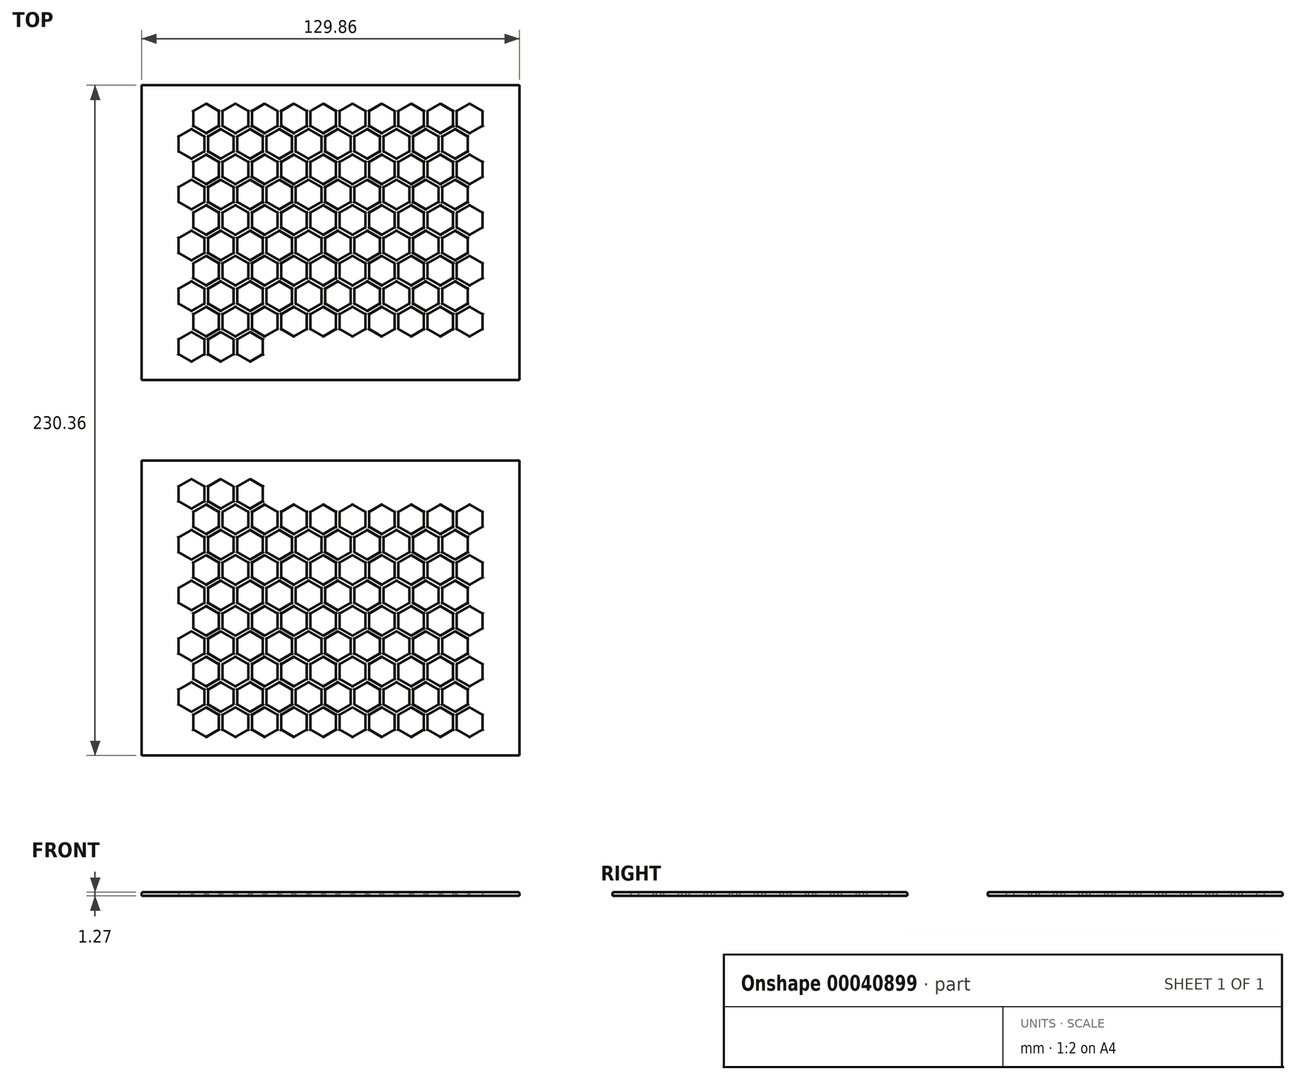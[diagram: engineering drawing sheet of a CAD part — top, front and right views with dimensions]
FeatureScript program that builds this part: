
annotation { "Feature Type Name" : "Feature", "Feature Type Description" : "" }
export const myFeature = defineFeature(function(context is Context, id is Id, definition is map)
    precondition{}
    {
        {
            var Q0;
            Q0=qCreatedBy(makeId("Top.planeOp"),FACE);
            var sketch = newSketch(context, id + "F0", { "sketchPlane" : qUnion([Q0])});
            skCircle(sketch, "E0.cCircle", {"center": v(-4.27, 25.27) * mm, "radius": 5.08 * mm, "construction": true});
            skLineSegment(sketch, "E0.0", {"start": v(-4.27, 20.19) * mm, "end": v(-8.67, 22.73) * mm});
            skLineSegment(sketch, "E0.1", {"start": v(-8.67, 22.73) * mm, "end": v(-8.67, 27.8) * mm});
            skLineSegment(sketch, "E0.2", {"start": v(-8.67, 27.8) * mm, "end": v(-4.27, 30.35) * mm});
            skLineSegment(sketch, "E0.3", {"start": v(-4.27, 30.35) * mm, "end": v(0.13, 27.8) * mm});
            skLineSegment(sketch, "E0.4", {"start": v(0.13, 27.8) * mm, "end": v(0.13, 22.73) * mm});
            skLineSegment(sketch, "E0.5", {"start": v(0.13, 22.73) * mm, "end": v(-4.27, 20.19) * mm});
            skLineSegment(sketch, "E1.1.0.0", {"start": v(5.8, 20.19) * mm, "end": v(1.4, 22.73) * mm});
            skLineSegment(sketch, "E1.1.0.1", {"start": v(1.4, 22.73) * mm, "end": v(1.4, 27.8) * mm});
            skLineSegment(sketch, "E1.1.0.2", {"start": v(1.4, 27.8) * mm, "end": v(5.8, 30.35) * mm});
            skLineSegment(sketch, "E1.1.0.3", {"start": v(5.8, 30.35) * mm, "end": v(10.2, 27.8) * mm});
            skLineSegment(sketch, "E1.1.0.4", {"start": v(10.2, 27.8) * mm, "end": v(10.2, 22.73) * mm});
            skLineSegment(sketch, "E1.1.0.5", {"start": v(10.2, 22.73) * mm, "end": v(5.8, 20.19) * mm});
            skCircle(sketch, "E1.1.0.6", {"center": v(5.8, 25.27) * mm, "radius": 5.08 * mm, "construction": true});
            skLineSegment(sketch, "E1.2.0.0", {"start": v(15.87, 20.19) * mm, "end": v(11.47, 22.73) * mm});
            skLineSegment(sketch, "E1.2.0.1", {"start": v(11.47, 22.73) * mm, "end": v(11.47, 27.8) * mm});
            skLineSegment(sketch, "E1.2.0.2", {"start": v(11.47, 27.8) * mm, "end": v(15.87, 30.35) * mm});
            skLineSegment(sketch, "E1.2.0.3", {"start": v(15.87, 30.35) * mm, "end": v(20.27, 27.8) * mm});
            skLineSegment(sketch, "E1.2.0.4", {"start": v(20.27, 27.8) * mm, "end": v(20.27, 22.73) * mm});
            skLineSegment(sketch, "E1.2.0.5", {"start": v(20.27, 22.73) * mm, "end": v(15.87, 20.19) * mm});
            skCircle(sketch, "E1.2.0.6", {"center": v(15.87, 25.27) * mm, "radius": 5.08 * mm, "construction": true});
            skLineSegment(sketch, "E1.direction1", {"start": v(-8.67, 22.73) * mm, "end": v(1.4, 22.73) * mm, "construction": true});
            skLineSegment(sketch, "E2.0.1.0", {"start": v(-3.63, 31.45) * mm, "end": v(6.44, 31.45) * mm, "construction": true});
            skLineSegment(sketch, "E2.0.1.1", {"start": v(75.65, 36.53) * mm, "end": v(75.65, 31.45) * mm});
            skLineSegment(sketch, "E2.0.1.2", {"start": v(45.44, 31.45) * mm, "end": v(41.04, 28.9) * mm});
            skLineSegment(sketch, "E2.0.1.3", {"start": v(36.64, 31.45) * mm, "end": v(36.64, 36.53) * mm});
            skCircle(sketch, "E2.0.1.4", {"center": v(61.18, 33.99) * mm, "radius": 5.08 * mm, "construction": true});
            skLineSegment(sketch, "E2.0.1.5", {"start": v(86.99, 31.45) * mm, "end": v(86.99, 36.53) * mm});
            skCircle(sketch, "E2.0.1.6", {"center": v(51.11, 33.99) * mm, "radius": 5.08 * mm, "construction": true});
            skLineSegment(sketch, "E2.0.1.7", {"start": v(5.17, 36.53) * mm, "end": v(5.17, 31.45) * mm});
            skLineSegment(sketch, "E2.0.1.8", {"start": v(46.71, 36.53) * mm, "end": v(51.11, 39.07) * mm});
            skLineSegment(sketch, "E2.0.1.9", {"start": v(61.18, 28.9) * mm, "end": v(56.78, 31.45) * mm});
            skLineSegment(sketch, "E2.0.1.10", {"start": v(26.58, 36.53) * mm, "end": v(30.98, 39.07) * mm});
            skLineSegment(sketch, "E2.0.1.11", {"start": v(55.51, 36.53) * mm, "end": v(55.51, 31.45) * mm});
            skLineSegment(sketch, "E2.0.1.12", {"start": v(81.32, 28.9) * mm, "end": v(76.92, 31.45) * mm});
            skCircle(sketch, "E2.0.1.13", {"center": v(71.25, 33.99) * mm, "radius": 5.08 * mm, "construction": true});
            skLineSegment(sketch, "E2.0.1.14", {"start": v(41.04, 28.9) * mm, "end": v(36.64, 31.45) * mm});
            skLineSegment(sketch, "E2.0.1.15", {"start": v(25.3, 31.45) * mm, "end": v(20.9, 28.9) * mm});
            skLineSegment(sketch, "E2.0.1.16", {"start": v(35.37, 36.53) * mm, "end": v(35.37, 31.45) * mm});
            skLineSegment(sketch, "E2.0.1.17", {"start": v(6.44, 36.53) * mm, "end": v(10.84, 39.07) * mm});
            skLineSegment(sketch, "E2.0.1.18", {"start": v(0.77, 28.9) * mm, "end": v(-3.63, 31.45) * mm});
            skLineSegment(sketch, "E2.0.1.19", {"start": v(41.04, 39.07) * mm, "end": v(45.44, 36.53) * mm});
            skCircle(sketch, "E2.0.1.20", {"center": v(20.9, 33.99) * mm, "radius": 5.08 * mm, "construction": true});
            skLineSegment(sketch, "E2.0.1.21", {"start": v(-3.63, 31.45) * mm, "end": v(-3.63, 36.53) * mm});
            skLineSegment(sketch, "E2.0.1.22", {"start": v(0.77, 39.07) * mm, "end": v(5.17, 36.53) * mm});
            skLineSegment(sketch, "E2.0.1.23", {"start": v(5.17, 31.45) * mm, "end": v(0.77, 28.9) * mm});
            skLineSegment(sketch, "E2.0.1.24", {"start": v(20.9, 39.07) * mm, "end": v(25.3, 36.53) * mm});
            skLineSegment(sketch, "E2.0.1.25", {"start": v(45.44, 36.53) * mm, "end": v(45.44, 31.45) * mm});
            skLineSegment(sketch, "E2.0.1.26", {"start": v(30.98, 28.9) * mm, "end": v(26.58, 31.45) * mm});
            skCircle(sketch, "E2.0.1.27", {"center": v(0.77, 33.99) * mm, "radius": 5.08 * mm, "construction": true});
            skLineSegment(sketch, "E2.0.1.28", {"start": v(71.25, 39.07) * mm, "end": v(75.65, 36.53) * mm});
            skLineSegment(sketch, "E2.0.1.29", {"start": v(65.58, 31.45) * mm, "end": v(61.18, 28.9) * mm});
            skLineSegment(sketch, "E2.0.1.30", {"start": v(56.78, 31.45) * mm, "end": v(56.78, 36.53) * mm});
            skLineSegment(sketch, "E2.0.1.31", {"start": v(36.64, 36.53) * mm, "end": v(41.04, 39.07) * mm});
            skLineSegment(sketch, "E2.0.1.32", {"start": v(66.85, 31.45) * mm, "end": v(66.85, 36.53) * mm});
            skLineSegment(sketch, "E2.0.1.33", {"start": v(-3.63, 36.53) * mm, "end": v(0.77, 39.07) * mm});
            skCircle(sketch, "E2.0.1.34", {"center": v(10.84, 33.99) * mm, "radius": 5.08 * mm, "construction": true});
            skLineSegment(sketch, "E2.0.1.35", {"start": v(16.5, 36.53) * mm, "end": v(20.9, 39.07) * mm});
            skLineSegment(sketch, "E2.0.1.36", {"start": v(85.72, 31.45) * mm, "end": v(81.32, 28.9) * mm});
            skLineSegment(sketch, "E2.0.1.37", {"start": v(10.84, 39.07) * mm, "end": v(15.24, 36.53) * mm});
            skLineSegment(sketch, "E2.0.1.38", {"start": v(65.58, 36.53) * mm, "end": v(65.58, 31.45) * mm});
            skLineSegment(sketch, "E2.0.1.39", {"start": v(81.32, 39.07) * mm, "end": v(85.72, 36.53) * mm});
            skLineSegment(sketch, "E2.0.1.40", {"start": v(10.84, 28.9) * mm, "end": v(6.44, 31.45) * mm});
            skLineSegment(sketch, "E2.0.1.41", {"start": v(26.58, 31.45) * mm, "end": v(26.58, 36.53) * mm});
            skLineSegment(sketch, "E2.0.1.42", {"start": v(51.11, 39.07) * mm, "end": v(55.51, 36.53) * mm});
            skCircle(sketch, "E2.0.1.43", {"center": v(41.04, 33.99) * mm, "radius": 5.08 * mm, "construction": true});
            skLineSegment(sketch, "E2.0.1.44", {"start": v(56.78, 36.53) * mm, "end": v(61.18, 39.07) * mm});
            skCircle(sketch, "E2.0.1.45", {"center": v(91.39, 33.99) * mm, "radius": 5.08 * mm, "construction": true});
            skLineSegment(sketch, "E2.0.1.46", {"start": v(6.44, 31.45) * mm, "end": v(6.44, 36.53) * mm});
            skLineSegment(sketch, "E2.0.1.47", {"start": v(35.37, 31.45) * mm, "end": v(30.98, 28.9) * mm});
            skLineSegment(sketch, "E2.0.1.48", {"start": v(16.5, 31.45) * mm, "end": v(16.5, 36.53) * mm});
            skLineSegment(sketch, "E2.0.1.49", {"start": v(91.39, 28.9) * mm, "end": v(86.99, 31.45) * mm});
            skCircle(sketch, "E2.0.1.50", {"center": v(30.98, 33.99) * mm, "radius": 5.08 * mm, "construction": true});
            skLineSegment(sketch, "E2.0.1.51", {"start": v(91.39, 39.07) * mm, "end": v(95.79, 36.53) * mm});
            skLineSegment(sketch, "E2.0.1.52", {"start": v(95.79, 31.45) * mm, "end": v(91.39, 28.9) * mm});
            skLineSegment(sketch, "E2.0.1.53", {"start": v(86.99, 36.53) * mm, "end": v(91.39, 39.07) * mm});
            skLineSegment(sketch, "E2.0.1.54", {"start": v(95.79, 36.53) * mm, "end": v(95.79, 31.45) * mm});
            skLineSegment(sketch, "E2.0.1.55", {"start": v(55.51, 31.45) * mm, "end": v(51.11, 28.9) * mm});
            skLineSegment(sketch, "E2.0.1.56", {"start": v(30.98, 39.07) * mm, "end": v(35.37, 36.53) * mm});
            skLineSegment(sketch, "E2.0.1.57", {"start": v(25.3, 36.53) * mm, "end": v(25.3, 31.45) * mm});
            skLineSegment(sketch, "E2.0.1.58", {"start": v(76.92, 31.45) * mm, "end": v(76.92, 36.53) * mm});
            skCircle(sketch, "E2.0.1.59", {"center": v(81.32, 33.99) * mm, "radius": 5.08 * mm, "construction": true});
            skLineSegment(sketch, "E2.0.1.60", {"start": v(85.72, 36.53) * mm, "end": v(85.72, 31.45) * mm});
            skLineSegment(sketch, "E2.0.1.61", {"start": v(71.25, 28.9) * mm, "end": v(66.85, 31.45) * mm});
            skLineSegment(sketch, "E2.0.1.62", {"start": v(61.18, 39.07) * mm, "end": v(65.58, 36.53) * mm});
            skLineSegment(sketch, "E2.0.1.63", {"start": v(66.85, 36.53) * mm, "end": v(71.25, 39.07) * mm});
            skLineSegment(sketch, "E2.0.1.64", {"start": v(15.24, 36.53) * mm, "end": v(15.24, 31.45) * mm});
            skLineSegment(sketch, "E2.0.1.65", {"start": v(15.24, 31.45) * mm, "end": v(10.84, 28.9) * mm});
            skLineSegment(sketch, "E2.0.1.66", {"start": v(51.11, 28.9) * mm, "end": v(46.71, 31.45) * mm});
            skLineSegment(sketch, "E2.0.1.67", {"start": v(46.71, 31.45) * mm, "end": v(46.71, 36.53) * mm});
            skLineSegment(sketch, "E2.0.1.68", {"start": v(76.92, 36.53) * mm, "end": v(81.32, 39.07) * mm});
            skLineSegment(sketch, "E2.0.1.69", {"start": v(20.9, 28.9) * mm, "end": v(16.5, 31.45) * mm});
            skLineSegment(sketch, "E2.0.1.70", {"start": v(75.65, 31.45) * mm, "end": v(71.25, 28.9) * mm});
            skLineSegment(sketch, "E2.direction1", {"start": v(-8.67, 22.73) * mm, "end": v(18.3, 22.73) * mm, "construction": true});
            skLineSegment(sketch, "E2.direction2", {"start": v(-8.67, 22.73) * mm, "end": v(-3.63, 31.45) * mm, "construction": true});
            skLineSegment(sketch, "E3", {"start": v(0.13, 27.8) * mm, "end": v(0.77, 28.9) * mm, "construction": true});
            skLineSegment(sketch, "E4", {"start": v(0.77, 28.9) * mm, "end": v(1.4, 27.8) * mm, "construction": true});
            skLineSegment(sketch, "E5", {"start": v(0.13, 27.8) * mm, "end": v(1.4, 27.8) * mm, "construction": true});
            skLineSegment(sketch, "E6.0.1.0", {"start": v(-3.63, 48.89) * mm, "end": v(6.44, 48.89) * mm, "construction": true});
            skCircle(sketch, "E6.0.1.1", {"center": v(20.9, 51.43) * mm, "radius": 5.08 * mm, "construction": true});
            skLineSegment(sketch, "E6.0.1.2", {"start": v(76.92, 53.97) * mm, "end": v(81.32, 56.5) * mm});
            skCircle(sketch, "E6.0.1.3", {"center": v(61.18, 51.43) * mm, "radius": 5.08 * mm, "construction": true});
            skLineSegment(sketch, "E6.0.1.4", {"start": v(80.68, 45.25) * mm, "end": v(80.68, 40.17) * mm});
            skLineSegment(sketch, "E6.0.1.5", {"start": v(-8.67, 40.17) * mm, "end": v(18.3, 40.17) * mm, "construction": true});
            skCircle(sketch, "E6.0.1.6", {"center": v(51.11, 51.43) * mm, "radius": 5.08 * mm, "construction": true});
            skCircle(sketch, "E6.0.1.7", {"center": v(0.77, 51.43) * mm, "radius": 5.08 * mm, "construction": true});
            skLineSegment(sketch, "E6.0.1.8", {"start": v(61.82, 40.17) * mm, "end": v(61.82, 45.25) * mm});
            skCircle(sketch, "E6.0.1.9", {"center": v(76.28, 42.7) * mm, "radius": 5.08 * mm, "construction": true});
            skLineSegment(sketch, "E6.0.1.10", {"start": v(56.15, 37.63) * mm, "end": v(51.75, 40.17) * mm});
            skLineSegment(sketch, "E6.0.1.11", {"start": v(15.87, 37.63) * mm, "end": v(11.47, 40.17) * mm});
            skLineSegment(sketch, "E6.0.1.12", {"start": v(71.25, 56.5) * mm, "end": v(75.65, 53.97) * mm});
            skLineSegment(sketch, "E6.0.1.13", {"start": v(20.27, 40.17) * mm, "end": v(15.87, 37.63) * mm});
            skLineSegment(sketch, "E6.0.1.14", {"start": v(56.78, 53.97) * mm, "end": v(61.18, 56.5) * mm});
            skLineSegment(sketch, "E6.0.1.15", {"start": v(95.79, 48.89) * mm, "end": v(91.39, 46.35) * mm});
            skLineSegment(sketch, "E6.0.1.16", {"start": v(30.34, 40.17) * mm, "end": v(25.94, 37.63) * mm});
            skLineSegment(sketch, "E6.0.1.17", {"start": v(60.55, 45.25) * mm, "end": v(60.55, 40.17) * mm});
            skLineSegment(sketch, "E6.0.1.18", {"start": v(91.39, 56.5) * mm, "end": v(95.79, 53.97) * mm});
            skLineSegment(sketch, "E6.0.1.19", {"start": v(-8.67, 40.17) * mm, "end": v(-3.63, 48.89) * mm, "construction": true});
            skLineSegment(sketch, "E6.0.1.20", {"start": v(41.04, 56.5) * mm, "end": v(45.44, 53.97) * mm});
            skLineSegment(sketch, "E6.0.1.21", {"start": v(36, 37.63) * mm, "end": v(31.61, 40.17) * mm});
            skLineSegment(sketch, "E6.0.1.22", {"start": v(81.32, 56.5) * mm, "end": v(85.72, 53.97) * mm});
            skLineSegment(sketch, "E6.0.1.23", {"start": v(66.22, 37.63) * mm, "end": v(61.82, 40.17) * mm});
            skLineSegment(sketch, "E6.0.1.24", {"start": v(40.4, 40.17) * mm, "end": v(36, 37.63) * mm});
            skLineSegment(sketch, "E6.0.1.25", {"start": v(10.84, 56.5) * mm, "end": v(15.24, 53.97) * mm});
            skLineSegment(sketch, "E6.0.1.26", {"start": v(55.51, 53.97) * mm, "end": v(55.51, 48.89) * mm});
            skLineSegment(sketch, "E6.0.1.27", {"start": v(61.18, 46.35) * mm, "end": v(56.78, 48.89) * mm});
            skLineSegment(sketch, "E6.0.1.28", {"start": v(60.55, 40.17) * mm, "end": v(56.15, 37.63) * mm});
            skLineSegment(sketch, "E6.0.1.29", {"start": v(10.2, 40.17) * mm, "end": v(5.8, 37.63) * mm});
            skLineSegment(sketch, "E6.0.1.30", {"start": v(0.13, 40.17) * mm, "end": v(-4.27, 37.63) * mm});
            skLineSegment(sketch, "E6.0.1.31", {"start": v(45.44, 53.97) * mm, "end": v(45.44, 48.89) * mm});
            skCircle(sketch, "E6.0.1.32", {"center": v(10.84, 51.43) * mm, "radius": 5.08 * mm, "construction": true});
            skLineSegment(sketch, "E6.0.1.33", {"start": v(65.58, 53.97) * mm, "end": v(65.58, 48.89) * mm});
            skLineSegment(sketch, "E6.0.1.34", {"start": v(-3.63, 48.89) * mm, "end": v(-3.63, 53.97) * mm});
            skCircle(sketch, "E6.0.1.35", {"center": v(71.25, 51.43) * mm, "radius": 5.08 * mm, "construction": true});
            skLineSegment(sketch, "E6.0.1.36", {"start": v(90.75, 45.25) * mm, "end": v(90.75, 40.17) * mm});
            skLineSegment(sketch, "E6.0.1.37", {"start": v(61.82, 45.25) * mm, "end": v(66.22, 47.79) * mm});
            skLineSegment(sketch, "E6.0.1.38", {"start": v(46.08, 37.63) * mm, "end": v(41.68, 40.17) * mm});
            skLineSegment(sketch, "E6.0.1.39", {"start": v(71.25, 46.35) * mm, "end": v(66.85, 48.89) * mm});
            skCircle(sketch, "E6.0.1.40", {"center": v(91.39, 51.43) * mm, "radius": 5.08 * mm, "construction": true});
            skLineSegment(sketch, "E6.0.1.41", {"start": v(65.58, 48.89) * mm, "end": v(61.18, 46.35) * mm});
            skLineSegment(sketch, "E6.0.1.42", {"start": v(20.9, 56.5) * mm, "end": v(25.3, 53.97) * mm});
            skLineSegment(sketch, "E6.0.1.43", {"start": v(56.15, 47.79) * mm, "end": v(60.55, 45.25) * mm});
            skLineSegment(sketch, "E6.0.1.44", {"start": v(-8.67, 45.25) * mm, "end": v(-4.27, 47.79) * mm});
            skCircle(sketch, "E6.0.1.45", {"center": v(25.94, 42.7) * mm, "radius": 5.08 * mm, "construction": true});
            skLineSegment(sketch, "E6.0.1.46", {"start": v(90.75, 40.17) * mm, "end": v(86.35, 37.63) * mm});
            skCircle(sketch, "E6.0.1.47", {"center": v(-4.27, 42.7) * mm, "radius": 5.08 * mm, "construction": true});
            skLineSegment(sketch, "E6.0.1.48", {"start": v(51.11, 56.5) * mm, "end": v(55.51, 53.97) * mm});
            skLineSegment(sketch, "E6.0.1.49", {"start": v(80.68, 40.17) * mm, "end": v(76.28, 37.63) * mm});
            skCircle(sketch, "E6.0.1.50", {"center": v(5.8, 42.7) * mm, "radius": 5.08 * mm, "construction": true});
            skLineSegment(sketch, "E6.0.1.51", {"start": v(0.77, 56.5) * mm, "end": v(5.17, 53.97) * mm});
            skLineSegment(sketch, "E6.0.1.52", {"start": v(66.22, 47.79) * mm, "end": v(70.62, 45.25) * mm});
            skLineSegment(sketch, "E6.0.1.53", {"start": v(61.18, 56.5) * mm, "end": v(65.58, 53.97) * mm});
            skLineSegment(sketch, "E6.0.1.54", {"start": v(56.78, 48.89) * mm, "end": v(56.78, 53.97) * mm});
            skLineSegment(sketch, "E6.0.1.55", {"start": v(81.95, 40.17) * mm, "end": v(81.95, 45.25) * mm});
            skCircle(sketch, "E6.0.1.56", {"center": v(56.15, 42.7) * mm, "radius": 5.08 * mm, "construction": true});
            skLineSegment(sketch, "E6.0.1.57", {"start": v(86.99, 53.97) * mm, "end": v(91.39, 56.5) * mm});
            skCircle(sketch, "E6.0.1.58", {"center": v(81.32, 51.43) * mm, "radius": 5.08 * mm, "construction": true});
            skLineSegment(sketch, "E6.0.1.59", {"start": v(-4.27, 37.63) * mm, "end": v(-8.67, 40.17) * mm});
            skLineSegment(sketch, "E6.0.1.60", {"start": v(25.94, 37.63) * mm, "end": v(21.54, 40.17) * mm});
            skCircle(sketch, "E6.0.1.61", {"center": v(86.35, 42.7) * mm, "radius": 5.08 * mm, "construction": true});
            skLineSegment(sketch, "E6.0.1.62", {"start": v(41.68, 45.25) * mm, "end": v(46.08, 47.79) * mm});
            skLineSegment(sketch, "E6.0.1.63", {"start": v(66.85, 53.97) * mm, "end": v(71.25, 56.5) * mm});
            skLineSegment(sketch, "E6.0.1.64", {"start": v(36.64, 53.97) * mm, "end": v(41.04, 56.5) * mm});
            skLineSegment(sketch, "E6.0.1.65", {"start": v(70.62, 40.17) * mm, "end": v(66.22, 37.63) * mm});
            skLineSegment(sketch, "E6.0.1.66", {"start": v(16.5, 48.89) * mm, "end": v(16.5, 53.97) * mm});
            skLineSegment(sketch, "E6.0.1.67", {"start": v(66.85, 48.89) * mm, "end": v(66.85, 53.97) * mm});
            skLineSegment(sketch, "E6.0.1.68", {"start": v(15.24, 53.97) * mm, "end": v(15.24, 48.89) * mm});
            skCircle(sketch, "E6.0.1.69", {"center": v(66.22, 42.7) * mm, "radius": 5.08 * mm, "construction": true});
            skLineSegment(sketch, "E6.0.1.70", {"start": v(50.48, 45.25) * mm, "end": v(50.48, 40.17) * mm});
            skLineSegment(sketch, "E6.0.1.71", {"start": v(-3.63, 53.97) * mm, "end": v(0.77, 56.5) * mm});
            skLineSegment(sketch, "E6.0.1.72", {"start": v(6.44, 53.97) * mm, "end": v(10.84, 56.5) * mm});
            skLineSegment(sketch, "E6.0.1.73", {"start": v(-8.67, 40.17) * mm, "end": v(-8.67, 45.25) * mm});
            skCircle(sketch, "E6.0.1.74", {"center": v(41.04, 51.43) * mm, "radius": 5.08 * mm, "construction": true});
            skLineSegment(sketch, "E6.0.1.75", {"start": v(46.71, 48.89) * mm, "end": v(46.71, 53.97) * mm});
            skLineSegment(sketch, "E6.0.1.76", {"start": v(16.5, 53.97) * mm, "end": v(20.9, 56.5) * mm});
            skLineSegment(sketch, "E6.0.1.77", {"start": v(5.8, 37.63) * mm, "end": v(1.4, 40.17) * mm});
            skLineSegment(sketch, "E6.0.1.78", {"start": v(30.98, 56.5) * mm, "end": v(35.37, 53.97) * mm});
            skCircle(sketch, "E6.0.1.79", {"center": v(46.08, 42.7) * mm, "radius": 5.08 * mm, "construction": true});
            skLineSegment(sketch, "E6.0.1.80", {"start": v(86.35, 37.63) * mm, "end": v(81.95, 40.17) * mm});
            skLineSegment(sketch, "E6.0.1.81", {"start": v(95.79, 53.97) * mm, "end": v(95.79, 48.89) * mm});
            skLineSegment(sketch, "E6.0.1.82", {"start": v(51.75, 40.17) * mm, "end": v(51.75, 45.25) * mm});
            skLineSegment(sketch, "E6.0.1.83", {"start": v(46.71, 53.97) * mm, "end": v(51.11, 56.5) * mm});
            skCircle(sketch, "E6.0.1.84", {"center": v(30.98, 51.43) * mm, "radius": 5.08 * mm, "construction": true});
            skLineSegment(sketch, "E6.0.1.85", {"start": v(26.58, 53.97) * mm, "end": v(30.98, 56.5) * mm});
            skLineSegment(sketch, "E6.0.1.86", {"start": v(50.48, 40.17) * mm, "end": v(46.08, 37.63) * mm});
            skLineSegment(sketch, "E6.0.1.87", {"start": v(76.28, 37.63) * mm, "end": v(71.89, 40.17) * mm});
            skLineSegment(sketch, "E6.0.1.88", {"start": v(5.17, 53.97) * mm, "end": v(5.17, 48.89) * mm});
            skLineSegment(sketch, "E6.0.1.89", {"start": v(51.11, 46.35) * mm, "end": v(46.71, 48.89) * mm});
            skLineSegment(sketch, "E6.0.1.90", {"start": v(86.35, 47.79) * mm, "end": v(90.75, 45.25) * mm});
            skLineSegment(sketch, "E6.0.1.91", {"start": v(71.89, 40.17) * mm, "end": v(71.89, 45.25) * mm});
            skLineSegment(sketch, "E6.0.1.92", {"start": v(81.32, 46.35) * mm, "end": v(76.92, 48.89) * mm});
            skCircle(sketch, "E6.0.1.93", {"center": v(36, 42.7) * mm, "radius": 5.08 * mm, "construction": true});
            skLineSegment(sketch, "E6.0.1.94", {"start": v(85.72, 53.97) * mm, "end": v(85.72, 48.89) * mm});
            skLineSegment(sketch, "E6.0.1.95", {"start": v(10.84, 46.35) * mm, "end": v(6.44, 48.89) * mm});
            skLineSegment(sketch, "E6.0.1.96", {"start": v(20.27, 45.25) * mm, "end": v(20.27, 40.17) * mm});
            skLineSegment(sketch, "E6.0.1.97", {"start": v(31.61, 40.17) * mm, "end": v(31.61, 45.25) * mm});
            skLineSegment(sketch, "E6.0.1.98", {"start": v(30.34, 45.25) * mm, "end": v(30.34, 40.17) * mm});
            skLineSegment(sketch, "E6.0.1.99", {"start": v(5.17, 48.89) * mm, "end": v(0.77, 46.35) * mm});
            skLineSegment(sketch, "E6.0.1.100", {"start": v(31.61, 45.25) * mm, "end": v(36, 47.79) * mm});
            skLineSegment(sketch, "E6.0.1.101", {"start": v(81.95, 45.25) * mm, "end": v(86.35, 47.79) * mm});
            skLineSegment(sketch, "E6.0.1.102", {"start": v(86.99, 48.89) * mm, "end": v(86.99, 53.97) * mm});
            skLineSegment(sketch, "E6.0.1.103", {"start": v(55.51, 48.89) * mm, "end": v(51.11, 46.35) * mm});
            skLineSegment(sketch, "E6.0.1.104", {"start": v(75.65, 48.89) * mm, "end": v(71.25, 46.35) * mm});
            skLineSegment(sketch, "E6.0.1.105", {"start": v(76.28, 47.79) * mm, "end": v(80.68, 45.25) * mm});
            skLineSegment(sketch, "E6.0.1.106", {"start": v(30.98, 46.35) * mm, "end": v(26.58, 48.89) * mm});
            skLineSegment(sketch, "E6.0.1.107", {"start": v(26.58, 48.89) * mm, "end": v(26.58, 53.97) * mm});
            skLineSegment(sketch, "E6.0.1.108", {"start": v(1.4, 45.25) * mm, "end": v(5.8, 47.79) * mm});
            skLineSegment(sketch, "E6.0.1.109", {"start": v(15.87, 47.79) * mm, "end": v(20.27, 45.25) * mm});
            skLineSegment(sketch, "E6.0.1.110", {"start": v(45.44, 48.89) * mm, "end": v(41.04, 46.35) * mm});
            skLineSegment(sketch, "E6.0.1.111", {"start": v(76.92, 48.89) * mm, "end": v(76.92, 53.97) * mm});
            skLineSegment(sketch, "E6.0.1.112", {"start": v(1.4, 40.17) * mm, "end": v(1.4, 45.25) * mm});
            skLineSegment(sketch, "E6.0.1.113", {"start": v(10.2, 45.25) * mm, "end": v(10.2, 40.17) * mm});
            skLineSegment(sketch, "E6.0.1.114", {"start": v(20.9, 46.35) * mm, "end": v(16.5, 48.89) * mm});
            skLineSegment(sketch, "E6.0.1.115", {"start": v(25.3, 53.97) * mm, "end": v(25.3, 48.89) * mm});
            skCircle(sketch, "E6.0.1.116", {"center": v(15.87, 42.7) * mm, "radius": 5.08 * mm, "construction": true});
            skLineSegment(sketch, "E6.0.1.117", {"start": v(0.13, 45.25) * mm, "end": v(0.13, 40.17) * mm});
            skLineSegment(sketch, "E6.0.1.118", {"start": v(36, 47.79) * mm, "end": v(40.4, 45.25) * mm});
            skLineSegment(sketch, "E6.0.1.119", {"start": v(-8.67, 40.17) * mm, "end": v(1.4, 40.17) * mm, "construction": true});
            skLineSegment(sketch, "E6.0.1.120", {"start": v(41.04, 46.35) * mm, "end": v(36.64, 48.89) * mm});
            skLineSegment(sketch, "E6.0.1.121", {"start": v(11.47, 45.25) * mm, "end": v(15.87, 47.79) * mm});
            skLineSegment(sketch, "E6.0.1.122", {"start": v(41.68, 40.17) * mm, "end": v(41.68, 45.25) * mm});
            skLineSegment(sketch, "E6.0.1.123", {"start": v(6.44, 48.89) * mm, "end": v(6.44, 53.97) * mm});
            skLineSegment(sketch, "E6.0.1.124", {"start": v(51.75, 45.25) * mm, "end": v(56.15, 47.79) * mm});
            skLineSegment(sketch, "E6.0.1.125", {"start": v(40.4, 45.25) * mm, "end": v(40.4, 40.17) * mm});
            skLineSegment(sketch, "E6.0.1.126", {"start": v(25.3, 48.89) * mm, "end": v(20.9, 46.35) * mm});
            skLineSegment(sketch, "E6.0.1.127", {"start": v(70.62, 45.25) * mm, "end": v(70.62, 40.17) * mm});
            skLineSegment(sketch, "E6.0.1.128", {"start": v(35.37, 48.89) * mm, "end": v(30.98, 46.35) * mm});
            skLineSegment(sketch, "E6.0.1.129", {"start": v(46.08, 47.79) * mm, "end": v(50.48, 45.25) * mm});
            skLineSegment(sketch, "E6.0.1.130", {"start": v(21.54, 40.17) * mm, "end": v(21.54, 45.25) * mm});
            skLineSegment(sketch, "E6.0.1.131", {"start": v(35.37, 53.97) * mm, "end": v(35.37, 48.89) * mm});
            skLineSegment(sketch, "E6.0.1.132", {"start": v(85.72, 48.89) * mm, "end": v(81.32, 46.35) * mm});
            skLineSegment(sketch, "E6.0.1.133", {"start": v(71.89, 45.25) * mm, "end": v(76.28, 47.79) * mm});
            skLineSegment(sketch, "E6.0.1.134", {"start": v(21.54, 45.25) * mm, "end": v(25.94, 47.79) * mm});
            skLineSegment(sketch, "E6.0.1.135", {"start": v(91.39, 46.35) * mm, "end": v(86.99, 48.89) * mm});
            skLineSegment(sketch, "E6.0.1.136", {"start": v(75.65, 53.97) * mm, "end": v(75.65, 48.89) * mm});
            skLineSegment(sketch, "E6.0.1.137", {"start": v(15.24, 48.89) * mm, "end": v(10.84, 46.35) * mm});
            skLineSegment(sketch, "E6.0.1.138", {"start": v(36.64, 48.89) * mm, "end": v(36.64, 53.97) * mm});
            skLineSegment(sketch, "E6.0.1.139", {"start": v(5.8, 47.79) * mm, "end": v(10.2, 45.25) * mm});
            skLineSegment(sketch, "E6.0.1.140", {"start": v(25.94, 47.79) * mm, "end": v(30.34, 45.25) * mm});
            skLineSegment(sketch, "E6.0.1.141", {"start": v(11.47, 40.17) * mm, "end": v(11.47, 45.25) * mm});
            skLineSegment(sketch, "E6.0.1.142", {"start": v(0.77, 46.35) * mm, "end": v(1.4, 45.25) * mm, "construction": true});
            skLineSegment(sketch, "E6.0.1.143", {"start": v(-4.27, 47.79) * mm, "end": v(0.13, 45.25) * mm});
            skLineSegment(sketch, "E6.0.1.144", {"start": v(0.77, 46.35) * mm, "end": v(-3.63, 48.89) * mm});
            skLineSegment(sketch, "E6.0.1.145", {"start": v(0.13, 45.25) * mm, "end": v(1.4, 45.25) * mm, "construction": true});
            skLineSegment(sketch, "E6.0.1.146", {"start": v(0.13, 45.25) * mm, "end": v(0.77, 46.35) * mm, "construction": true});
            skLineSegment(sketch, "E6.0.2.0", {"start": v(-3.63, 66.33) * mm, "end": v(6.44, 66.33) * mm, "construction": true});
            skCircle(sketch, "E6.0.2.1", {"center": v(20.9, 68.87) * mm, "radius": 5.08 * mm, "construction": true});
            skLineSegment(sketch, "E6.0.2.2", {"start": v(76.92, 71.4) * mm, "end": v(81.32, 73.95) * mm});
            skCircle(sketch, "E6.0.2.3", {"center": v(61.18, 68.87) * mm, "radius": 5.08 * mm, "construction": true});
            skLineSegment(sketch, "E6.0.2.4", {"start": v(80.68, 62.69) * mm, "end": v(80.68, 57.6) * mm});
            skLineSegment(sketch, "E6.0.2.5", {"start": v(-8.67, 57.6) * mm, "end": v(18.3, 57.6) * mm, "construction": true});
            skCircle(sketch, "E6.0.2.6", {"center": v(51.11, 68.87) * mm, "radius": 5.08 * mm, "construction": true});
            skCircle(sketch, "E6.0.2.7", {"center": v(0.77, 68.87) * mm, "radius": 5.08 * mm, "construction": true});
            skLineSegment(sketch, "E6.0.2.8", {"start": v(61.82, 57.6) * mm, "end": v(61.82, 62.69) * mm});
            skCircle(sketch, "E6.0.2.9", {"center": v(76.28, 60.15) * mm, "radius": 5.08 * mm, "construction": true});
            skLineSegment(sketch, "E6.0.2.10", {"start": v(56.15, 55.07) * mm, "end": v(51.75, 57.6) * mm});
            skLineSegment(sketch, "E6.0.2.11", {"start": v(15.87, 55.07) * mm, "end": v(11.47, 57.6) * mm});
            skLineSegment(sketch, "E6.0.2.12", {"start": v(71.25, 73.95) * mm, "end": v(75.65, 71.4) * mm});
            skLineSegment(sketch, "E6.0.2.13", {"start": v(20.27, 57.6) * mm, "end": v(15.87, 55.07) * mm});
            skLineSegment(sketch, "E6.0.2.14", {"start": v(56.78, 71.4) * mm, "end": v(61.18, 73.95) * mm});
            skLineSegment(sketch, "E6.0.2.15", {"start": v(95.79, 66.33) * mm, "end": v(91.39, 63.79) * mm});
            skLineSegment(sketch, "E6.0.2.16", {"start": v(30.34, 57.6) * mm, "end": v(25.94, 55.07) * mm});
            skLineSegment(sketch, "E6.0.2.17", {"start": v(60.55, 62.69) * mm, "end": v(60.55, 57.6) * mm});
            skLineSegment(sketch, "E6.0.2.18", {"start": v(91.39, 73.95) * mm, "end": v(95.79, 71.4) * mm});
            skLineSegment(sketch, "E6.0.2.19", {"start": v(-8.67, 57.6) * mm, "end": v(-3.63, 66.33) * mm, "construction": true});
            skLineSegment(sketch, "E6.0.2.20", {"start": v(41.04, 73.95) * mm, "end": v(45.44, 71.4) * mm});
            skLineSegment(sketch, "E6.0.2.21", {"start": v(36, 55.07) * mm, "end": v(31.61, 57.6) * mm});
            skLineSegment(sketch, "E6.0.2.22", {"start": v(81.32, 73.95) * mm, "end": v(85.72, 71.4) * mm});
            skLineSegment(sketch, "E6.0.2.23", {"start": v(66.22, 55.07) * mm, "end": v(61.82, 57.6) * mm});
            skLineSegment(sketch, "E6.0.2.24", {"start": v(40.4, 57.6) * mm, "end": v(36, 55.07) * mm});
            skLineSegment(sketch, "E6.0.2.25", {"start": v(10.84, 73.95) * mm, "end": v(15.24, 71.4) * mm});
            skLineSegment(sketch, "E6.0.2.26", {"start": v(55.51, 71.4) * mm, "end": v(55.51, 66.33) * mm});
            skLineSegment(sketch, "E6.0.2.27", {"start": v(61.18, 63.79) * mm, "end": v(56.78, 66.33) * mm});
            skLineSegment(sketch, "E6.0.2.28", {"start": v(60.55, 57.6) * mm, "end": v(56.15, 55.07) * mm});
            skLineSegment(sketch, "E6.0.2.29", {"start": v(10.2, 57.6) * mm, "end": v(5.8, 55.07) * mm});
            skLineSegment(sketch, "E6.0.2.30", {"start": v(0.13, 57.6) * mm, "end": v(-4.27, 55.07) * mm});
            skLineSegment(sketch, "E6.0.2.31", {"start": v(45.44, 71.4) * mm, "end": v(45.44, 66.33) * mm});
            skCircle(sketch, "E6.0.2.32", {"center": v(10.84, 68.87) * mm, "radius": 5.08 * mm, "construction": true});
            skLineSegment(sketch, "E6.0.2.33", {"start": v(65.58, 71.4) * mm, "end": v(65.58, 66.33) * mm});
            skLineSegment(sketch, "E6.0.2.34", {"start": v(-3.63, 66.33) * mm, "end": v(-3.63, 71.4) * mm});
            skCircle(sketch, "E6.0.2.35", {"center": v(71.25, 68.87) * mm, "radius": 5.08 * mm, "construction": true});
            skLineSegment(sketch, "E6.0.2.36", {"start": v(90.75, 62.69) * mm, "end": v(90.75, 57.6) * mm});
            skLineSegment(sketch, "E6.0.2.37", {"start": v(61.82, 62.69) * mm, "end": v(66.22, 65.23) * mm});
            skLineSegment(sketch, "E6.0.2.38", {"start": v(46.08, 55.07) * mm, "end": v(41.68, 57.6) * mm});
            skLineSegment(sketch, "E6.0.2.39", {"start": v(71.25, 63.79) * mm, "end": v(66.85, 66.33) * mm});
            skCircle(sketch, "E6.0.2.40", {"center": v(91.39, 68.87) * mm, "radius": 5.08 * mm, "construction": true});
            skLineSegment(sketch, "E6.0.2.41", {"start": v(65.58, 66.33) * mm, "end": v(61.18, 63.79) * mm});
            skLineSegment(sketch, "E6.0.2.42", {"start": v(20.9, 73.95) * mm, "end": v(25.3, 71.4) * mm});
            skLineSegment(sketch, "E6.0.2.43", {"start": v(56.15, 65.23) * mm, "end": v(60.55, 62.69) * mm});
            skLineSegment(sketch, "E6.0.2.44", {"start": v(-8.67, 62.69) * mm, "end": v(-4.27, 65.23) * mm});
            skCircle(sketch, "E6.0.2.45", {"center": v(25.94, 60.15) * mm, "radius": 5.08 * mm, "construction": true});
            skLineSegment(sketch, "E6.0.2.46", {"start": v(90.75, 57.6) * mm, "end": v(86.35, 55.07) * mm});
            skCircle(sketch, "E6.0.2.47", {"center": v(-4.27, 60.15) * mm, "radius": 5.08 * mm, "construction": true});
            skLineSegment(sketch, "E6.0.2.48", {"start": v(51.11, 73.95) * mm, "end": v(55.51, 71.4) * mm});
            skLineSegment(sketch, "E6.0.2.49", {"start": v(80.68, 57.6) * mm, "end": v(76.28, 55.07) * mm});
            skCircle(sketch, "E6.0.2.50", {"center": v(5.8, 60.15) * mm, "radius": 5.08 * mm, "construction": true});
            skLineSegment(sketch, "E6.0.2.51", {"start": v(0.77, 73.95) * mm, "end": v(5.17, 71.4) * mm});
            skLineSegment(sketch, "E6.0.2.52", {"start": v(66.22, 65.23) * mm, "end": v(70.62, 62.69) * mm});
            skLineSegment(sketch, "E6.0.2.53", {"start": v(61.18, 73.95) * mm, "end": v(65.58, 71.4) * mm});
            skLineSegment(sketch, "E6.0.2.54", {"start": v(56.78, 66.33) * mm, "end": v(56.78, 71.4) * mm});
            skLineSegment(sketch, "E6.0.2.55", {"start": v(81.95, 57.6) * mm, "end": v(81.95, 62.69) * mm});
            skCircle(sketch, "E6.0.2.56", {"center": v(56.15, 60.15) * mm, "radius": 5.08 * mm, "construction": true});
            skLineSegment(sketch, "E6.0.2.57", {"start": v(86.99, 71.4) * mm, "end": v(91.39, 73.95) * mm});
            skCircle(sketch, "E6.0.2.58", {"center": v(81.32, 68.87) * mm, "radius": 5.08 * mm, "construction": true});
            skLineSegment(sketch, "E6.0.2.59", {"start": v(-4.27, 55.07) * mm, "end": v(-8.67, 57.6) * mm});
            skLineSegment(sketch, "E6.0.2.60", {"start": v(25.94, 55.07) * mm, "end": v(21.54, 57.6) * mm});
            skCircle(sketch, "E6.0.2.61", {"center": v(86.35, 60.15) * mm, "radius": 5.08 * mm, "construction": true});
            skLineSegment(sketch, "E6.0.2.62", {"start": v(41.68, 62.69) * mm, "end": v(46.08, 65.23) * mm});
            skLineSegment(sketch, "E6.0.2.63", {"start": v(66.85, 71.4) * mm, "end": v(71.25, 73.95) * mm});
            skLineSegment(sketch, "E6.0.2.64", {"start": v(36.64, 71.4) * mm, "end": v(41.04, 73.95) * mm});
            skLineSegment(sketch, "E6.0.2.65", {"start": v(70.62, 57.6) * mm, "end": v(66.22, 55.07) * mm});
            skLineSegment(sketch, "E6.0.2.66", {"start": v(16.5, 66.33) * mm, "end": v(16.5, 71.4) * mm});
            skLineSegment(sketch, "E6.0.2.67", {"start": v(66.85, 66.33) * mm, "end": v(66.85, 71.4) * mm});
            skLineSegment(sketch, "E6.0.2.68", {"start": v(15.24, 71.4) * mm, "end": v(15.24, 66.33) * mm});
            skCircle(sketch, "E6.0.2.69", {"center": v(66.22, 60.15) * mm, "radius": 5.08 * mm, "construction": true});
            skLineSegment(sketch, "E6.0.2.70", {"start": v(50.48, 62.69) * mm, "end": v(50.48, 57.6) * mm});
            skLineSegment(sketch, "E6.0.2.71", {"start": v(-3.63, 71.4) * mm, "end": v(0.77, 73.95) * mm});
            skLineSegment(sketch, "E6.0.2.72", {"start": v(6.44, 71.4) * mm, "end": v(10.84, 73.95) * mm});
            skLineSegment(sketch, "E6.0.2.73", {"start": v(-8.67, 57.6) * mm, "end": v(-8.67, 62.69) * mm});
            skCircle(sketch, "E6.0.2.74", {"center": v(41.04, 68.87) * mm, "radius": 5.08 * mm, "construction": true});
            skLineSegment(sketch, "E6.0.2.75", {"start": v(46.71, 66.33) * mm, "end": v(46.71, 71.4) * mm});
            skLineSegment(sketch, "E6.0.2.76", {"start": v(16.5, 71.4) * mm, "end": v(20.9, 73.95) * mm});
            skLineSegment(sketch, "E6.0.2.77", {"start": v(5.8, 55.07) * mm, "end": v(1.4, 57.6) * mm});
            skLineSegment(sketch, "E6.0.2.78", {"start": v(30.98, 73.95) * mm, "end": v(35.37, 71.4) * mm});
            skCircle(sketch, "E6.0.2.79", {"center": v(46.08, 60.15) * mm, "radius": 5.08 * mm, "construction": true});
            skLineSegment(sketch, "E6.0.2.80", {"start": v(86.35, 55.07) * mm, "end": v(81.95, 57.6) * mm});
            skLineSegment(sketch, "E6.0.2.81", {"start": v(95.79, 71.4) * mm, "end": v(95.79, 66.33) * mm});
            skLineSegment(sketch, "E6.0.2.82", {"start": v(51.75, 57.6) * mm, "end": v(51.75, 62.69) * mm});
            skLineSegment(sketch, "E6.0.2.83", {"start": v(46.71, 71.4) * mm, "end": v(51.11, 73.95) * mm});
            skCircle(sketch, "E6.0.2.84", {"center": v(30.98, 68.87) * mm, "radius": 5.08 * mm, "construction": true});
            skLineSegment(sketch, "E6.0.2.85", {"start": v(26.58, 71.4) * mm, "end": v(30.98, 73.95) * mm});
            skLineSegment(sketch, "E6.0.2.86", {"start": v(50.48, 57.6) * mm, "end": v(46.08, 55.07) * mm});
            skLineSegment(sketch, "E6.0.2.87", {"start": v(76.28, 55.07) * mm, "end": v(71.89, 57.6) * mm});
            skLineSegment(sketch, "E6.0.2.88", {"start": v(5.17, 71.4) * mm, "end": v(5.17, 66.33) * mm});
            skLineSegment(sketch, "E6.0.2.89", {"start": v(51.11, 63.79) * mm, "end": v(46.71, 66.33) * mm});
            skLineSegment(sketch, "E6.0.2.90", {"start": v(86.35, 65.23) * mm, "end": v(90.75, 62.69) * mm});
            skLineSegment(sketch, "E6.0.2.91", {"start": v(71.89, 57.6) * mm, "end": v(71.89, 62.69) * mm});
            skLineSegment(sketch, "E6.0.2.92", {"start": v(81.32, 63.79) * mm, "end": v(76.92, 66.33) * mm});
            skCircle(sketch, "E6.0.2.93", {"center": v(36, 60.15) * mm, "radius": 5.08 * mm, "construction": true});
            skLineSegment(sketch, "E6.0.2.94", {"start": v(85.72, 71.4) * mm, "end": v(85.72, 66.33) * mm});
            skLineSegment(sketch, "E6.0.2.95", {"start": v(10.84, 63.79) * mm, "end": v(6.44, 66.33) * mm});
            skLineSegment(sketch, "E6.0.2.96", {"start": v(20.27, 62.69) * mm, "end": v(20.27, 57.6) * mm});
            skLineSegment(sketch, "E6.0.2.97", {"start": v(31.61, 57.6) * mm, "end": v(31.61, 62.69) * mm});
            skLineSegment(sketch, "E6.0.2.98", {"start": v(30.34, 62.69) * mm, "end": v(30.34, 57.6) * mm});
            skLineSegment(sketch, "E6.0.2.99", {"start": v(5.17, 66.33) * mm, "end": v(0.77, 63.79) * mm});
            skLineSegment(sketch, "E6.0.2.100", {"start": v(31.61, 62.69) * mm, "end": v(36, 65.23) * mm});
            skLineSegment(sketch, "E6.0.2.101", {"start": v(81.95, 62.69) * mm, "end": v(86.35, 65.23) * mm});
            skLineSegment(sketch, "E6.0.2.102", {"start": v(86.99, 66.33) * mm, "end": v(86.99, 71.4) * mm});
            skLineSegment(sketch, "E6.0.2.103", {"start": v(55.51, 66.33) * mm, "end": v(51.11, 63.79) * mm});
            skLineSegment(sketch, "E6.0.2.104", {"start": v(75.65, 66.33) * mm, "end": v(71.25, 63.79) * mm});
            skLineSegment(sketch, "E6.0.2.105", {"start": v(76.28, 65.23) * mm, "end": v(80.68, 62.69) * mm});
            skLineSegment(sketch, "E6.0.2.106", {"start": v(30.98, 63.79) * mm, "end": v(26.58, 66.33) * mm});
            skLineSegment(sketch, "E6.0.2.107", {"start": v(26.58, 66.33) * mm, "end": v(26.58, 71.4) * mm});
            skLineSegment(sketch, "E6.0.2.108", {"start": v(1.4, 62.69) * mm, "end": v(5.8, 65.23) * mm});
            skLineSegment(sketch, "E6.0.2.109", {"start": v(15.87, 65.23) * mm, "end": v(20.27, 62.69) * mm});
            skLineSegment(sketch, "E6.0.2.110", {"start": v(45.44, 66.33) * mm, "end": v(41.04, 63.79) * mm});
            skLineSegment(sketch, "E6.0.2.111", {"start": v(76.92, 66.33) * mm, "end": v(76.92, 71.4) * mm});
            skLineSegment(sketch, "E6.0.2.112", {"start": v(1.4, 57.6) * mm, "end": v(1.4, 62.69) * mm});
            skLineSegment(sketch, "E6.0.2.113", {"start": v(10.2, 62.69) * mm, "end": v(10.2, 57.6) * mm});
            skLineSegment(sketch, "E6.0.2.114", {"start": v(20.9, 63.79) * mm, "end": v(16.5, 66.33) * mm});
            skLineSegment(sketch, "E6.0.2.115", {"start": v(25.3, 71.4) * mm, "end": v(25.3, 66.33) * mm});
            skCircle(sketch, "E6.0.2.116", {"center": v(15.87, 60.15) * mm, "radius": 5.08 * mm, "construction": true});
            skLineSegment(sketch, "E6.0.2.117", {"start": v(0.13, 62.69) * mm, "end": v(0.13, 57.6) * mm});
            skLineSegment(sketch, "E6.0.2.118", {"start": v(36, 65.23) * mm, "end": v(40.4, 62.69) * mm});
            skLineSegment(sketch, "E6.0.2.119", {"start": v(-8.67, 57.6) * mm, "end": v(1.4, 57.6) * mm, "construction": true});
            skLineSegment(sketch, "E6.0.2.120", {"start": v(41.04, 63.79) * mm, "end": v(36.64, 66.33) * mm});
            skLineSegment(sketch, "E6.0.2.121", {"start": v(11.47, 62.69) * mm, "end": v(15.87, 65.23) * mm});
            skLineSegment(sketch, "E6.0.2.122", {"start": v(41.68, 57.6) * mm, "end": v(41.68, 62.69) * mm});
            skLineSegment(sketch, "E6.0.2.123", {"start": v(6.44, 66.33) * mm, "end": v(6.44, 71.4) * mm});
            skLineSegment(sketch, "E6.0.2.124", {"start": v(51.75, 62.69) * mm, "end": v(56.15, 65.23) * mm});
            skLineSegment(sketch, "E6.0.2.125", {"start": v(40.4, 62.69) * mm, "end": v(40.4, 57.6) * mm});
            skLineSegment(sketch, "E6.0.2.126", {"start": v(25.3, 66.33) * mm, "end": v(20.9, 63.79) * mm});
            skLineSegment(sketch, "E6.0.2.127", {"start": v(70.62, 62.69) * mm, "end": v(70.62, 57.6) * mm});
            skLineSegment(sketch, "E6.0.2.128", {"start": v(35.37, 66.33) * mm, "end": v(30.98, 63.79) * mm});
            skLineSegment(sketch, "E6.0.2.129", {"start": v(46.08, 65.23) * mm, "end": v(50.48, 62.69) * mm});
            skLineSegment(sketch, "E6.0.2.130", {"start": v(21.54, 57.6) * mm, "end": v(21.54, 62.69) * mm});
            skLineSegment(sketch, "E6.0.2.131", {"start": v(35.37, 71.4) * mm, "end": v(35.37, 66.33) * mm});
            skLineSegment(sketch, "E6.0.2.132", {"start": v(85.72, 66.33) * mm, "end": v(81.32, 63.79) * mm});
            skLineSegment(sketch, "E6.0.2.133", {"start": v(71.89, 62.69) * mm, "end": v(76.28, 65.23) * mm});
            skLineSegment(sketch, "E6.0.2.134", {"start": v(21.54, 62.69) * mm, "end": v(25.94, 65.23) * mm});
            skLineSegment(sketch, "E6.0.2.135", {"start": v(91.39, 63.79) * mm, "end": v(86.99, 66.33) * mm});
            skLineSegment(sketch, "E6.0.2.136", {"start": v(75.65, 71.4) * mm, "end": v(75.65, 66.33) * mm});
            skLineSegment(sketch, "E6.0.2.137", {"start": v(15.24, 66.33) * mm, "end": v(10.84, 63.79) * mm});
            skLineSegment(sketch, "E6.0.2.138", {"start": v(36.64, 66.33) * mm, "end": v(36.64, 71.4) * mm});
            skLineSegment(sketch, "E6.0.2.139", {"start": v(5.8, 65.23) * mm, "end": v(10.2, 62.69) * mm});
            skLineSegment(sketch, "E6.0.2.140", {"start": v(25.94, 65.23) * mm, "end": v(30.34, 62.69) * mm});
            skLineSegment(sketch, "E6.0.2.141", {"start": v(11.47, 57.6) * mm, "end": v(11.47, 62.69) * mm});
            skLineSegment(sketch, "E6.0.2.142", {"start": v(0.77, 63.79) * mm, "end": v(1.4, 62.69) * mm, "construction": true});
            skLineSegment(sketch, "E6.0.2.143", {"start": v(-4.27, 65.23) * mm, "end": v(0.13, 62.69) * mm});
            skLineSegment(sketch, "E6.0.2.144", {"start": v(0.77, 63.79) * mm, "end": v(-3.63, 66.33) * mm});
            skLineSegment(sketch, "E6.0.2.145", {"start": v(0.13, 62.69) * mm, "end": v(1.4, 62.69) * mm, "construction": true});
            skLineSegment(sketch, "E6.0.2.146", {"start": v(0.13, 62.69) * mm, "end": v(0.77, 63.79) * mm, "construction": true});
            skLineSegment(sketch, "E6.direction1", {"start": v(-3.63, 31.45) * mm, "end": v(21.77, 31.45) * mm, "construction": true});
            skLineSegment(sketch, "E6.direction2", {"start": v(-3.63, 31.45) * mm, "end": v(-3.63, 48.89) * mm, "construction": true});
            skLineSegment(sketch, "E7", {"start": v(5.8, 37.63) * mm, "end": v(5.17, 36.53) * mm, "construction": true});
            skLineSegment(sketch, "E8", {"start": v(5.8, 37.63) * mm, "end": v(6.44, 36.53) * mm, "construction": true});
            skLineSegment(sketch, "E9", {"start": v(5.17, 36.53) * mm, "end": v(6.44, 36.53) * mm, "construction": true});
            skLineSegment(sketch, "E10.bottom", {"start": v(-21.37, 115.18) * mm, "end": v(108.49, 115.18) * mm});
            skLineSegment(sketch, "E10.top", {"start": v(-21.37, 13.84) * mm, "end": v(108.49, 13.84) * mm});
            skLineSegment(sketch, "E10.left", {"start": v(-21.37, 115.18) * mm, "end": v(-21.37, 13.84) * mm});
            skLineSegment(sketch, "E10.right", {"start": v(108.49, 115.18) * mm, "end": v(108.49, 13.84) * mm});
            skLineSegment(sketch, "E11", {"start": v(0, 0) * mm, "end": v(59.74, 0) * mm, "construction": true});
            skLineSegment(sketch, "E12.0.0.3", {"start": v(-3.63, 83.77) * mm, "end": v(6.44, 83.77) * mm, "construction": true});
            skCircle(sketch, "E12.3.0.3", {"center": v(20.9, 86.3) * mm, "radius": 5.08 * mm, "construction": true});
            skLineSegment(sketch, "E12.5.0.3", {"start": v(76.92, 88.85) * mm, "end": v(81.32, 91.39) * mm});
            skCircle(sketch, "E12.8.0.3", {"center": v(61.18, 86.3) * mm, "radius": 5.08 * mm, "construction": true});
            skLineSegment(sketch, "E12.10.0.3", {"start": v(80.68, 80.13) * mm, "end": v(80.68, 75.05) * mm});
            skLineSegment(sketch, "E12.13.0.3", {"start": v(-8.67, 75.05) * mm, "end": v(18.3, 75.05) * mm, "construction": true});
            skCircle(sketch, "E12.16.0.3", {"center": v(51.11, 86.3) * mm, "radius": 5.08 * mm, "construction": true});
            skCircle(sketch, "E12.18.0.3", {"center": v(0.77, 86.3) * mm, "radius": 5.08 * mm, "construction": true});
            skLineSegment(sketch, "E12.20.0.3", {"start": v(61.82, 75.05) * mm, "end": v(61.82, 80.13) * mm});
            skCircle(sketch, "E12.23.0.3", {"center": v(76.28, 77.59) * mm, "radius": 5.08 * mm, "construction": true});
            skLineSegment(sketch, "E12.25.0.3", {"start": v(56.15, 72.5) * mm, "end": v(51.75, 75.05) * mm});
            skLineSegment(sketch, "E12.28.0.3", {"start": v(15.87, 72.5) * mm, "end": v(11.47, 75.05) * mm});
            skLineSegment(sketch, "E12.31.0.3", {"start": v(71.25, 91.39) * mm, "end": v(75.65, 88.85) * mm});
            skLineSegment(sketch, "E12.34.0.3", {"start": v(20.27, 75.05) * mm, "end": v(15.87, 72.5) * mm});
            skLineSegment(sketch, "E12.37.0.3", {"start": v(56.78, 88.85) * mm, "end": v(61.18, 91.39) * mm});
            skLineSegment(sketch, "E12.40.0.3", {"start": v(95.79, 83.77) * mm, "end": v(91.39, 81.23) * mm});
            skLineSegment(sketch, "E12.43.0.3", {"start": v(30.34, 75.05) * mm, "end": v(25.94, 72.5) * mm});
            skLineSegment(sketch, "E12.46.0.3", {"start": v(60.55, 80.13) * mm, "end": v(60.55, 75.05) * mm});
            skLineSegment(sketch, "E12.49.0.3", {"start": v(91.39, 91.39) * mm, "end": v(95.79, 88.85) * mm});
            skLineSegment(sketch, "E12.52.0.3", {"start": v(-8.67, 75.05) * mm, "end": v(-3.63, 83.77) * mm, "construction": true});
            skLineSegment(sketch, "E12.55.0.3", {"start": v(41.04, 91.39) * mm, "end": v(45.44, 88.85) * mm});
            skLineSegment(sketch, "E12.58.0.3", {"start": v(36, 72.5) * mm, "end": v(31.61, 75.05) * mm});
            skLineSegment(sketch, "E12.61.0.3", {"start": v(81.32, 91.39) * mm, "end": v(85.72, 88.85) * mm});
            skLineSegment(sketch, "E12.64.0.3", {"start": v(66.22, 72.5) * mm, "end": v(61.82, 75.05) * mm});
            skLineSegment(sketch, "E12.67.0.3", {"start": v(40.4, 75.05) * mm, "end": v(36, 72.5) * mm});
            skLineSegment(sketch, "E12.70.0.3", {"start": v(10.84, 91.39) * mm, "end": v(15.24, 88.85) * mm});
            skLineSegment(sketch, "E12.73.0.3", {"start": v(55.51, 88.85) * mm, "end": v(55.51, 83.77) * mm});
            skLineSegment(sketch, "E12.76.0.3", {"start": v(61.18, 81.23) * mm, "end": v(56.78, 83.77) * mm});
            skLineSegment(sketch, "E12.79.0.3", {"start": v(60.55, 75.05) * mm, "end": v(56.15, 72.5) * mm});
            skLineSegment(sketch, "E12.82.0.3", {"start": v(10.2, 75.05) * mm, "end": v(5.8, 72.5) * mm});
            skLineSegment(sketch, "E12.85.0.3", {"start": v(0.13, 75.05) * mm, "end": v(-4.27, 72.5) * mm});
            skLineSegment(sketch, "E12.88.0.3", {"start": v(45.44, 88.85) * mm, "end": v(45.44, 83.77) * mm});
            skCircle(sketch, "E12.91.0.3", {"center": v(10.84, 86.3) * mm, "radius": 5.08 * mm, "construction": true});
            skLineSegment(sketch, "E12.93.0.3", {"start": v(65.58, 88.85) * mm, "end": v(65.58, 83.77) * mm});
            skLineSegment(sketch, "E12.96.0.3", {"start": v(-3.63, 83.77) * mm, "end": v(-3.63, 88.85) * mm});
            skCircle(sketch, "E12.99.0.3", {"center": v(71.25, 86.3) * mm, "radius": 5.08 * mm, "construction": true});
            skLineSegment(sketch, "E12.101.0.3", {"start": v(90.75, 80.13) * mm, "end": v(90.75, 75.05) * mm});
            skLineSegment(sketch, "E12.104.0.3", {"start": v(61.82, 80.13) * mm, "end": v(66.22, 82.67) * mm});
            skLineSegment(sketch, "E12.107.0.3", {"start": v(46.08, 72.5) * mm, "end": v(41.68, 75.05) * mm});
            skLineSegment(sketch, "E12.110.0.3", {"start": v(71.25, 81.23) * mm, "end": v(66.85, 83.77) * mm});
            skCircle(sketch, "E12.113.0.3", {"center": v(91.39, 86.3) * mm, "radius": 5.08 * mm, "construction": true});
            skLineSegment(sketch, "E12.115.0.3", {"start": v(65.58, 83.77) * mm, "end": v(61.18, 81.23) * mm});
            skLineSegment(sketch, "E12.118.0.3", {"start": v(20.9, 91.39) * mm, "end": v(25.3, 88.85) * mm});
            skLineSegment(sketch, "E12.121.0.3", {"start": v(56.15, 82.67) * mm, "end": v(60.55, 80.13) * mm});
            skLineSegment(sketch, "E12.124.0.3", {"start": v(-8.67, 80.13) * mm, "end": v(-4.27, 82.67) * mm});
            skCircle(sketch, "E12.127.0.3", {"center": v(25.94, 77.59) * mm, "radius": 5.08 * mm, "construction": true});
            skLineSegment(sketch, "E12.129.0.3", {"start": v(90.75, 75.05) * mm, "end": v(86.35, 72.5) * mm});
            skCircle(sketch, "E12.132.0.3", {"center": v(-4.27, 77.59) * mm, "radius": 5.08 * mm, "construction": true});
            skLineSegment(sketch, "E12.134.0.3", {"start": v(51.11, 91.39) * mm, "end": v(55.51, 88.85) * mm});
            skLineSegment(sketch, "E12.137.0.3", {"start": v(80.68, 75.05) * mm, "end": v(76.28, 72.5) * mm});
            skCircle(sketch, "E12.140.0.3", {"center": v(5.8, 77.59) * mm, "radius": 5.08 * mm, "construction": true});
            skLineSegment(sketch, "E12.142.0.3", {"start": v(0.77, 91.39) * mm, "end": v(5.17, 88.85) * mm});
            skLineSegment(sketch, "E12.145.0.3", {"start": v(66.22, 82.67) * mm, "end": v(70.62, 80.13) * mm});
            skLineSegment(sketch, "E12.148.0.3", {"start": v(61.18, 91.39) * mm, "end": v(65.58, 88.85) * mm});
            skLineSegment(sketch, "E12.151.0.3", {"start": v(56.78, 83.77) * mm, "end": v(56.78, 88.85) * mm});
            skLineSegment(sketch, "E12.154.0.3", {"start": v(81.95, 75.05) * mm, "end": v(81.95, 80.13) * mm});
            skCircle(sketch, "E12.157.0.3", {"center": v(56.15, 77.59) * mm, "radius": 5.08 * mm, "construction": true});
            skLineSegment(sketch, "E12.159.0.3", {"start": v(86.99, 88.85) * mm, "end": v(91.39, 91.39) * mm});
            skCircle(sketch, "E12.162.0.3", {"center": v(81.32, 86.3) * mm, "radius": 5.08 * mm, "construction": true});
            skLineSegment(sketch, "E12.164.0.3", {"start": v(-4.27, 72.5) * mm, "end": v(-8.67, 75.05) * mm});
            skLineSegment(sketch, "E12.167.0.3", {"start": v(25.94, 72.5) * mm, "end": v(21.54, 75.05) * mm});
            skCircle(sketch, "E12.170.0.3", {"center": v(86.35, 77.59) * mm, "radius": 5.08 * mm, "construction": true});
            skLineSegment(sketch, "E12.172.0.3", {"start": v(41.68, 80.13) * mm, "end": v(46.08, 82.67) * mm});
            skLineSegment(sketch, "E12.175.0.3", {"start": v(66.85, 88.85) * mm, "end": v(71.25, 91.39) * mm});
            skLineSegment(sketch, "E12.178.0.3", {"start": v(36.64, 88.85) * mm, "end": v(41.04, 91.39) * mm});
            skLineSegment(sketch, "E12.181.0.3", {"start": v(70.62, 75.05) * mm, "end": v(66.22, 72.5) * mm});
            skLineSegment(sketch, "E12.184.0.3", {"start": v(16.5, 83.77) * mm, "end": v(16.5, 88.85) * mm});
            skLineSegment(sketch, "E12.187.0.3", {"start": v(66.85, 83.77) * mm, "end": v(66.85, 88.85) * mm});
            skLineSegment(sketch, "E12.190.0.3", {"start": v(15.24, 88.85) * mm, "end": v(15.24, 83.77) * mm});
            skCircle(sketch, "E12.193.0.3", {"center": v(66.22, 77.59) * mm, "radius": 5.08 * mm, "construction": true});
            skLineSegment(sketch, "E12.195.0.3", {"start": v(50.48, 80.13) * mm, "end": v(50.48, 75.05) * mm});
            skLineSegment(sketch, "E12.198.0.3", {"start": v(-3.63, 88.85) * mm, "end": v(0.77, 91.39) * mm});
            skLineSegment(sketch, "E12.201.0.3", {"start": v(6.44, 88.85) * mm, "end": v(10.84, 91.39) * mm});
            skLineSegment(sketch, "E12.204.0.3", {"start": v(-8.67, 75.05) * mm, "end": v(-8.67, 80.13) * mm});
            skCircle(sketch, "E12.207.0.3", {"center": v(41.04, 86.3) * mm, "radius": 5.08 * mm, "construction": true});
            skLineSegment(sketch, "E12.209.0.3", {"start": v(46.71, 83.77) * mm, "end": v(46.71, 88.85) * mm});
            skLineSegment(sketch, "E12.212.0.3", {"start": v(16.5, 88.85) * mm, "end": v(20.9, 91.39) * mm});
            skLineSegment(sketch, "E12.215.0.3", {"start": v(5.8, 72.5) * mm, "end": v(1.4, 75.05) * mm});
            skLineSegment(sketch, "E12.218.0.3", {"start": v(30.98, 91.39) * mm, "end": v(35.37, 88.85) * mm});
            skCircle(sketch, "E12.221.0.3", {"center": v(46.08, 77.59) * mm, "radius": 5.08 * mm, "construction": true});
            skLineSegment(sketch, "E12.223.0.3", {"start": v(86.35, 72.5) * mm, "end": v(81.95, 75.05) * mm});
            skLineSegment(sketch, "E12.226.0.3", {"start": v(95.79, 88.85) * mm, "end": v(95.79, 83.77) * mm});
            skLineSegment(sketch, "E12.229.0.3", {"start": v(51.75, 75.05) * mm, "end": v(51.75, 80.13) * mm});
            skLineSegment(sketch, "E12.232.0.3", {"start": v(46.71, 88.85) * mm, "end": v(51.11, 91.39) * mm});
            skCircle(sketch, "E12.235.0.3", {"center": v(30.98, 86.3) * mm, "radius": 5.08 * mm, "construction": true});
            skLineSegment(sketch, "E12.237.0.3", {"start": v(26.58, 88.85) * mm, "end": v(30.98, 91.39) * mm});
            skLineSegment(sketch, "E12.240.0.3", {"start": v(50.48, 75.05) * mm, "end": v(46.08, 72.5) * mm});
            skLineSegment(sketch, "E12.243.0.3", {"start": v(76.28, 72.5) * mm, "end": v(71.89, 75.05) * mm});
            skLineSegment(sketch, "E12.246.0.3", {"start": v(5.17, 88.85) * mm, "end": v(5.17, 83.77) * mm});
            skLineSegment(sketch, "E12.249.0.3", {"start": v(51.11, 81.23) * mm, "end": v(46.71, 83.77) * mm});
            skLineSegment(sketch, "E12.252.0.3", {"start": v(86.35, 82.67) * mm, "end": v(90.75, 80.13) * mm});
            skLineSegment(sketch, "E12.255.0.3", {"start": v(71.89, 75.05) * mm, "end": v(71.89, 80.13) * mm});
            skLineSegment(sketch, "E12.258.0.3", {"start": v(81.32, 81.23) * mm, "end": v(76.92, 83.77) * mm});
            skCircle(sketch, "E12.261.0.3", {"center": v(36, 77.59) * mm, "radius": 5.08 * mm, "construction": true});
            skLineSegment(sketch, "E12.263.0.3", {"start": v(85.72, 88.85) * mm, "end": v(85.72, 83.77) * mm});
            skLineSegment(sketch, "E12.266.0.3", {"start": v(10.84, 81.23) * mm, "end": v(6.44, 83.77) * mm});
            skLineSegment(sketch, "E12.269.0.3", {"start": v(20.27, 80.13) * mm, "end": v(20.27, 75.05) * mm});
            skLineSegment(sketch, "E12.272.0.3", {"start": v(31.61, 75.05) * mm, "end": v(31.61, 80.13) * mm});
            skLineSegment(sketch, "E12.275.0.3", {"start": v(30.34, 80.13) * mm, "end": v(30.34, 75.05) * mm});
            skLineSegment(sketch, "E12.278.0.3", {"start": v(5.17, 83.77) * mm, "end": v(0.77, 81.23) * mm});
            skLineSegment(sketch, "E12.281.0.3", {"start": v(31.61, 80.13) * mm, "end": v(36, 82.67) * mm});
            skLineSegment(sketch, "E12.284.0.3", {"start": v(81.95, 80.13) * mm, "end": v(86.35, 82.67) * mm});
            skLineSegment(sketch, "E12.287.0.3", {"start": v(86.99, 83.77) * mm, "end": v(86.99, 88.85) * mm});
            skLineSegment(sketch, "E12.290.0.3", {"start": v(55.51, 83.77) * mm, "end": v(51.11, 81.23) * mm});
            skLineSegment(sketch, "E12.293.0.3", {"start": v(75.65, 83.77) * mm, "end": v(71.25, 81.23) * mm});
            skLineSegment(sketch, "E12.296.0.3", {"start": v(76.28, 82.67) * mm, "end": v(80.68, 80.13) * mm});
            skLineSegment(sketch, "E12.299.0.3", {"start": v(30.98, 81.23) * mm, "end": v(26.58, 83.77) * mm});
            skLineSegment(sketch, "E12.302.0.3", {"start": v(26.58, 83.77) * mm, "end": v(26.58, 88.85) * mm});
            skLineSegment(sketch, "E12.305.0.3", {"start": v(1.4, 80.13) * mm, "end": v(5.8, 82.67) * mm});
            skLineSegment(sketch, "E12.308.0.3", {"start": v(15.87, 82.67) * mm, "end": v(20.27, 80.13) * mm});
            skLineSegment(sketch, "E12.311.0.3", {"start": v(45.44, 83.77) * mm, "end": v(41.04, 81.23) * mm});
            skLineSegment(sketch, "E12.314.0.3", {"start": v(76.92, 83.77) * mm, "end": v(76.92, 88.85) * mm});
            skLineSegment(sketch, "E12.317.0.3", {"start": v(1.4, 75.05) * mm, "end": v(1.4, 80.13) * mm});
            skLineSegment(sketch, "E12.320.0.3", {"start": v(10.2, 80.13) * mm, "end": v(10.2, 75.05) * mm});
            skLineSegment(sketch, "E12.323.0.3", {"start": v(20.9, 81.23) * mm, "end": v(16.5, 83.77) * mm});
            skLineSegment(sketch, "E12.326.0.3", {"start": v(25.3, 88.85) * mm, "end": v(25.3, 83.77) * mm});
            skCircle(sketch, "E12.329.0.3", {"center": v(15.87, 77.59) * mm, "radius": 5.08 * mm, "construction": true});
            skLineSegment(sketch, "E12.331.0.3", {"start": v(0.13, 80.13) * mm, "end": v(0.13, 75.05) * mm});
            skLineSegment(sketch, "E12.334.0.3", {"start": v(36, 82.67) * mm, "end": v(40.4, 80.13) * mm});
            skLineSegment(sketch, "E12.337.0.3", {"start": v(-8.67, 75.05) * mm, "end": v(1.4, 75.05) * mm, "construction": true});
            skLineSegment(sketch, "E12.340.0.3", {"start": v(41.04, 81.23) * mm, "end": v(36.64, 83.77) * mm});
            skLineSegment(sketch, "E12.343.0.3", {"start": v(11.47, 80.13) * mm, "end": v(15.87, 82.67) * mm});
            skLineSegment(sketch, "E12.346.0.3", {"start": v(41.68, 75.05) * mm, "end": v(41.68, 80.13) * mm});
            skLineSegment(sketch, "E12.349.0.3", {"start": v(6.44, 83.77) * mm, "end": v(6.44, 88.85) * mm});
            skLineSegment(sketch, "E12.352.0.3", {"start": v(51.75, 80.13) * mm, "end": v(56.15, 82.67) * mm});
            skLineSegment(sketch, "E12.355.0.3", {"start": v(40.4, 80.13) * mm, "end": v(40.4, 75.05) * mm});
            skLineSegment(sketch, "E12.358.0.3", {"start": v(25.3, 83.77) * mm, "end": v(20.9, 81.23) * mm});
            skLineSegment(sketch, "E12.361.0.3", {"start": v(70.62, 80.13) * mm, "end": v(70.62, 75.05) * mm});
            skLineSegment(sketch, "E12.364.0.3", {"start": v(35.37, 83.77) * mm, "end": v(30.98, 81.23) * mm});
            skLineSegment(sketch, "E12.367.0.3", {"start": v(46.08, 82.67) * mm, "end": v(50.48, 80.13) * mm});
            skLineSegment(sketch, "E12.370.0.3", {"start": v(21.54, 75.05) * mm, "end": v(21.54, 80.13) * mm});
            skLineSegment(sketch, "E12.373.0.3", {"start": v(35.37, 88.85) * mm, "end": v(35.37, 83.77) * mm});
            skLineSegment(sketch, "E12.376.0.3", {"start": v(85.72, 83.77) * mm, "end": v(81.32, 81.23) * mm});
            skLineSegment(sketch, "E12.379.0.3", {"start": v(71.89, 80.13) * mm, "end": v(76.28, 82.67) * mm});
            skLineSegment(sketch, "E12.382.0.3", {"start": v(21.54, 80.13) * mm, "end": v(25.94, 82.67) * mm});
            skLineSegment(sketch, "E12.385.0.3", {"start": v(91.39, 81.23) * mm, "end": v(86.99, 83.77) * mm});
            skLineSegment(sketch, "E12.388.0.3", {"start": v(75.65, 88.85) * mm, "end": v(75.65, 83.77) * mm});
            skLineSegment(sketch, "E12.391.0.3", {"start": v(15.24, 83.77) * mm, "end": v(10.84, 81.23) * mm});
            skLineSegment(sketch, "E12.394.0.3", {"start": v(36.64, 83.77) * mm, "end": v(36.64, 88.85) * mm});
            skLineSegment(sketch, "E12.397.0.3", {"start": v(5.8, 82.67) * mm, "end": v(10.2, 80.13) * mm});
            skLineSegment(sketch, "E12.400.0.3", {"start": v(25.94, 82.67) * mm, "end": v(30.34, 80.13) * mm});
            skLineSegment(sketch, "E12.403.0.3", {"start": v(11.47, 75.05) * mm, "end": v(11.47, 80.13) * mm});
            skLineSegment(sketch, "E12.406.0.3", {"start": v(0.77, 81.23) * mm, "end": v(1.4, 80.13) * mm, "construction": true});
            skLineSegment(sketch, "E12.409.0.3", {"start": v(-4.27, 82.67) * mm, "end": v(0.13, 80.13) * mm});
            skLineSegment(sketch, "E12.412.0.3", {"start": v(0.77, 81.23) * mm, "end": v(-3.63, 83.77) * mm});
            skLineSegment(sketch, "E12.415.0.3", {"start": v(0.13, 80.13) * mm, "end": v(1.4, 80.13) * mm, "construction": true});
            skLineSegment(sketch, "E12.418.0.3", {"start": v(0.13, 80.13) * mm, "end": v(0.77, 81.23) * mm, "construction": true});
            skLineSegment(sketch, "E12.0.0.4", {"start": v(-3.63, 101.2) * mm, "end": v(6.44, 101.2) * mm, "construction": true});
            skCircle(sketch, "E12.3.0.4", {"center": v(20.9, 103.75) * mm, "radius": 5.08 * mm, "construction": true});
            skLineSegment(sketch, "E12.5.0.4", {"start": v(76.92, 106.29) * mm, "end": v(81.32, 108.83) * mm});
            skCircle(sketch, "E12.8.0.4", {"center": v(61.18, 103.75) * mm, "radius": 5.08 * mm, "construction": true});
            skLineSegment(sketch, "E12.10.0.4", {"start": v(80.68, 97.57) * mm, "end": v(80.68, 92.49) * mm});
            skLineSegment(sketch, "E12.13.0.4", {"start": v(-8.67, 92.49) * mm, "end": v(18.3, 92.49) * mm, "construction": true});
            skCircle(sketch, "E12.16.0.4", {"center": v(51.11, 103.75) * mm, "radius": 5.08 * mm, "construction": true});
            skCircle(sketch, "E12.18.0.4", {"center": v(0.77, 103.75) * mm, "radius": 5.08 * mm, "construction": true});
            skLineSegment(sketch, "E12.20.0.4", {"start": v(61.82, 92.49) * mm, "end": v(61.82, 97.57) * mm});
            skCircle(sketch, "E12.23.0.4", {"center": v(76.28, 95.03) * mm, "radius": 5.08 * mm, "construction": true});
            skLineSegment(sketch, "E12.25.0.4", {"start": v(56.15, 89.95) * mm, "end": v(51.75, 92.49) * mm});
            skLineSegment(sketch, "E12.28.0.4", {"start": v(15.87, 89.95) * mm, "end": v(11.47, 92.49) * mm});
            skLineSegment(sketch, "E12.31.0.4", {"start": v(71.25, 108.83) * mm, "end": v(75.65, 106.29) * mm});
            skLineSegment(sketch, "E12.34.0.4", {"start": v(20.27, 92.49) * mm, "end": v(15.87, 89.95) * mm});
            skLineSegment(sketch, "E12.37.0.4", {"start": v(56.78, 106.29) * mm, "end": v(61.18, 108.83) * mm});
            skLineSegment(sketch, "E12.40.0.4", {"start": v(95.79, 101.2) * mm, "end": v(91.39, 98.67) * mm});
            skLineSegment(sketch, "E12.43.0.4", {"start": v(30.34, 92.49) * mm, "end": v(25.94, 89.95) * mm});
            skLineSegment(sketch, "E12.46.0.4", {"start": v(60.55, 97.57) * mm, "end": v(60.55, 92.49) * mm});
            skLineSegment(sketch, "E12.49.0.4", {"start": v(91.39, 108.83) * mm, "end": v(95.79, 106.29) * mm});
            skLineSegment(sketch, "E12.52.0.4", {"start": v(-8.67, 92.49) * mm, "end": v(-3.63, 101.2) * mm, "construction": true});
            skLineSegment(sketch, "E12.55.0.4", {"start": v(41.04, 108.83) * mm, "end": v(45.44, 106.29) * mm});
            skLineSegment(sketch, "E12.58.0.4", {"start": v(36, 89.95) * mm, "end": v(31.61, 92.49) * mm});
            skLineSegment(sketch, "E12.61.0.4", {"start": v(81.32, 108.83) * mm, "end": v(85.72, 106.29) * mm});
            skLineSegment(sketch, "E12.64.0.4", {"start": v(66.22, 89.95) * mm, "end": v(61.82, 92.49) * mm});
            skLineSegment(sketch, "E12.67.0.4", {"start": v(40.4, 92.49) * mm, "end": v(36, 89.95) * mm});
            skLineSegment(sketch, "E12.70.0.4", {"start": v(10.84, 108.83) * mm, "end": v(15.24, 106.29) * mm});
            skLineSegment(sketch, "E12.73.0.4", {"start": v(55.51, 106.29) * mm, "end": v(55.51, 101.2) * mm});
            skLineSegment(sketch, "E12.76.0.4", {"start": v(61.18, 98.67) * mm, "end": v(56.78, 101.2) * mm});
            skLineSegment(sketch, "E12.79.0.4", {"start": v(60.55, 92.49) * mm, "end": v(56.15, 89.95) * mm});
            skLineSegment(sketch, "E12.82.0.4", {"start": v(10.2, 92.49) * mm, "end": v(5.8, 89.95) * mm});
            skLineSegment(sketch, "E12.85.0.4", {"start": v(0.13, 92.49) * mm, "end": v(-4.27, 89.95) * mm});
            skLineSegment(sketch, "E12.88.0.4", {"start": v(45.44, 106.29) * mm, "end": v(45.44, 101.2) * mm});
            skCircle(sketch, "E12.91.0.4", {"center": v(10.84, 103.75) * mm, "radius": 5.08 * mm, "construction": true});
            skLineSegment(sketch, "E12.93.0.4", {"start": v(65.58, 106.29) * mm, "end": v(65.58, 101.2) * mm});
            skLineSegment(sketch, "E12.96.0.4", {"start": v(-3.63, 101.2) * mm, "end": v(-3.63, 106.29) * mm});
            skCircle(sketch, "E12.99.0.4", {"center": v(71.25, 103.75) * mm, "radius": 5.08 * mm, "construction": true});
            skLineSegment(sketch, "E12.101.0.4", {"start": v(90.75, 97.57) * mm, "end": v(90.75, 92.49) * mm});
            skLineSegment(sketch, "E12.104.0.4", {"start": v(61.82, 97.57) * mm, "end": v(66.22, 100.1) * mm});
            skLineSegment(sketch, "E12.107.0.4", {"start": v(46.08, 89.95) * mm, "end": v(41.68, 92.49) * mm});
            skLineSegment(sketch, "E12.110.0.4", {"start": v(71.25, 98.67) * mm, "end": v(66.85, 101.2) * mm});
            skCircle(sketch, "E12.113.0.4", {"center": v(91.39, 103.75) * mm, "radius": 5.08 * mm, "construction": true});
            skLineSegment(sketch, "E12.115.0.4", {"start": v(65.58, 101.2) * mm, "end": v(61.18, 98.67) * mm});
            skLineSegment(sketch, "E12.118.0.4", {"start": v(20.9, 108.83) * mm, "end": v(25.3, 106.29) * mm});
            skLineSegment(sketch, "E12.121.0.4", {"start": v(56.15, 100.1) * mm, "end": v(60.55, 97.57) * mm});
            skLineSegment(sketch, "E12.124.0.4", {"start": v(-8.67, 97.57) * mm, "end": v(-4.27, 100.1) * mm});
            skCircle(sketch, "E12.127.0.4", {"center": v(25.94, 95.03) * mm, "radius": 5.08 * mm, "construction": true});
            skLineSegment(sketch, "E12.129.0.4", {"start": v(90.75, 92.49) * mm, "end": v(86.35, 89.95) * mm});
            skCircle(sketch, "E12.132.0.4", {"center": v(-4.27, 95.03) * mm, "radius": 5.08 * mm, "construction": true});
            skLineSegment(sketch, "E12.134.0.4", {"start": v(51.11, 108.83) * mm, "end": v(55.51, 106.29) * mm});
            skLineSegment(sketch, "E12.137.0.4", {"start": v(80.68, 92.49) * mm, "end": v(76.28, 89.95) * mm});
            skCircle(sketch, "E12.140.0.4", {"center": v(5.8, 95.03) * mm, "radius": 5.08 * mm, "construction": true});
            skLineSegment(sketch, "E12.142.0.4", {"start": v(0.77, 108.83) * mm, "end": v(5.17, 106.29) * mm});
            skLineSegment(sketch, "E12.145.0.4", {"start": v(66.22, 100.1) * mm, "end": v(70.62, 97.57) * mm});
            skLineSegment(sketch, "E12.148.0.4", {"start": v(61.18, 108.83) * mm, "end": v(65.58, 106.29) * mm});
            skLineSegment(sketch, "E12.151.0.4", {"start": v(56.78, 101.2) * mm, "end": v(56.78, 106.29) * mm});
            skLineSegment(sketch, "E12.154.0.4", {"start": v(81.95, 92.49) * mm, "end": v(81.95, 97.57) * mm});
            skCircle(sketch, "E12.157.0.4", {"center": v(56.15, 95.03) * mm, "radius": 5.08 * mm, "construction": true});
            skLineSegment(sketch, "E12.159.0.4", {"start": v(86.99, 106.29) * mm, "end": v(91.39, 108.83) * mm});
            skCircle(sketch, "E12.162.0.4", {"center": v(81.32, 103.75) * mm, "radius": 5.08 * mm, "construction": true});
            skLineSegment(sketch, "E12.164.0.4", {"start": v(-4.27, 89.95) * mm, "end": v(-8.67, 92.49) * mm});
            skLineSegment(sketch, "E12.167.0.4", {"start": v(25.94, 89.95) * mm, "end": v(21.54, 92.49) * mm});
            skCircle(sketch, "E12.170.0.4", {"center": v(86.35, 95.03) * mm, "radius": 5.08 * mm, "construction": true});
            skLineSegment(sketch, "E12.172.0.4", {"start": v(41.68, 97.57) * mm, "end": v(46.08, 100.1) * mm});
            skLineSegment(sketch, "E12.175.0.4", {"start": v(66.85, 106.29) * mm, "end": v(71.25, 108.83) * mm});
            skLineSegment(sketch, "E12.178.0.4", {"start": v(36.64, 106.29) * mm, "end": v(41.04, 108.83) * mm});
            skLineSegment(sketch, "E12.181.0.4", {"start": v(70.62, 92.49) * mm, "end": v(66.22, 89.95) * mm});
            skLineSegment(sketch, "E12.184.0.4", {"start": v(16.5, 101.2) * mm, "end": v(16.5, 106.29) * mm});
            skLineSegment(sketch, "E12.187.0.4", {"start": v(66.85, 101.2) * mm, "end": v(66.85, 106.29) * mm});
            skLineSegment(sketch, "E12.190.0.4", {"start": v(15.24, 106.29) * mm, "end": v(15.24, 101.2) * mm});
            skCircle(sketch, "E12.193.0.4", {"center": v(66.22, 95.03) * mm, "radius": 5.08 * mm, "construction": true});
            skLineSegment(sketch, "E12.195.0.4", {"start": v(50.48, 97.57) * mm, "end": v(50.48, 92.49) * mm});
            skLineSegment(sketch, "E12.198.0.4", {"start": v(-3.63, 106.29) * mm, "end": v(0.77, 108.83) * mm});
            skLineSegment(sketch, "E12.201.0.4", {"start": v(6.44, 106.29) * mm, "end": v(10.84, 108.83) * mm});
            skLineSegment(sketch, "E12.204.0.4", {"start": v(-8.67, 92.49) * mm, "end": v(-8.67, 97.57) * mm});
            skCircle(sketch, "E12.207.0.4", {"center": v(41.04, 103.75) * mm, "radius": 5.08 * mm, "construction": true});
            skLineSegment(sketch, "E12.209.0.4", {"start": v(46.71, 101.2) * mm, "end": v(46.71, 106.29) * mm});
            skLineSegment(sketch, "E12.212.0.4", {"start": v(16.5, 106.29) * mm, "end": v(20.9, 108.83) * mm});
            skLineSegment(sketch, "E12.215.0.4", {"start": v(5.8, 89.95) * mm, "end": v(1.4, 92.49) * mm});
            skLineSegment(sketch, "E12.218.0.4", {"start": v(30.98, 108.83) * mm, "end": v(35.37, 106.29) * mm});
            skCircle(sketch, "E12.221.0.4", {"center": v(46.08, 95.03) * mm, "radius": 5.08 * mm, "construction": true});
            skLineSegment(sketch, "E12.223.0.4", {"start": v(86.35, 89.95) * mm, "end": v(81.95, 92.49) * mm});
            skLineSegment(sketch, "E12.226.0.4", {"start": v(95.79, 106.29) * mm, "end": v(95.79, 101.2) * mm});
            skLineSegment(sketch, "E12.229.0.4", {"start": v(51.75, 92.49) * mm, "end": v(51.75, 97.57) * mm});
            skLineSegment(sketch, "E12.232.0.4", {"start": v(46.71, 106.29) * mm, "end": v(51.11, 108.83) * mm});
            skCircle(sketch, "E12.235.0.4", {"center": v(30.98, 103.75) * mm, "radius": 5.08 * mm, "construction": true});
            skLineSegment(sketch, "E12.237.0.4", {"start": v(26.58, 106.29) * mm, "end": v(30.98, 108.83) * mm});
            skLineSegment(sketch, "E12.240.0.4", {"start": v(50.48, 92.49) * mm, "end": v(46.08, 89.95) * mm});
            skLineSegment(sketch, "E12.243.0.4", {"start": v(76.28, 89.95) * mm, "end": v(71.89, 92.49) * mm});
            skLineSegment(sketch, "E12.246.0.4", {"start": v(5.17, 106.29) * mm, "end": v(5.17, 101.2) * mm});
            skLineSegment(sketch, "E12.249.0.4", {"start": v(51.11, 98.67) * mm, "end": v(46.71, 101.2) * mm});
            skLineSegment(sketch, "E12.252.0.4", {"start": v(86.35, 100.1) * mm, "end": v(90.75, 97.57) * mm});
            skLineSegment(sketch, "E12.255.0.4", {"start": v(71.89, 92.49) * mm, "end": v(71.89, 97.57) * mm});
            skLineSegment(sketch, "E12.258.0.4", {"start": v(81.32, 98.67) * mm, "end": v(76.92, 101.2) * mm});
            skCircle(sketch, "E12.261.0.4", {"center": v(36, 95.03) * mm, "radius": 5.08 * mm, "construction": true});
            skLineSegment(sketch, "E12.263.0.4", {"start": v(85.72, 106.29) * mm, "end": v(85.72, 101.2) * mm});
            skLineSegment(sketch, "E12.266.0.4", {"start": v(10.84, 98.67) * mm, "end": v(6.44, 101.2) * mm});
            skLineSegment(sketch, "E12.269.0.4", {"start": v(20.27, 97.57) * mm, "end": v(20.27, 92.49) * mm});
            skLineSegment(sketch, "E12.272.0.4", {"start": v(31.61, 92.49) * mm, "end": v(31.61, 97.57) * mm});
            skLineSegment(sketch, "E12.275.0.4", {"start": v(30.34, 97.57) * mm, "end": v(30.34, 92.49) * mm});
            skLineSegment(sketch, "E12.278.0.4", {"start": v(5.17, 101.2) * mm, "end": v(0.77, 98.67) * mm});
            skLineSegment(sketch, "E12.281.0.4", {"start": v(31.61, 97.57) * mm, "end": v(36, 100.1) * mm});
            skLineSegment(sketch, "E12.284.0.4", {"start": v(81.95, 97.57) * mm, "end": v(86.35, 100.1) * mm});
            skLineSegment(sketch, "E12.287.0.4", {"start": v(86.99, 101.2) * mm, "end": v(86.99, 106.29) * mm});
            skLineSegment(sketch, "E12.290.0.4", {"start": v(55.51, 101.2) * mm, "end": v(51.11, 98.67) * mm});
            skLineSegment(sketch, "E12.293.0.4", {"start": v(75.65, 101.2) * mm, "end": v(71.25, 98.67) * mm});
            skLineSegment(sketch, "E12.296.0.4", {"start": v(76.28, 100.1) * mm, "end": v(80.68, 97.57) * mm});
            skLineSegment(sketch, "E12.299.0.4", {"start": v(30.98, 98.67) * mm, "end": v(26.58, 101.2) * mm});
            skLineSegment(sketch, "E12.302.0.4", {"start": v(26.58, 101.2) * mm, "end": v(26.58, 106.29) * mm});
            skLineSegment(sketch, "E12.305.0.4", {"start": v(1.4, 97.57) * mm, "end": v(5.8, 100.1) * mm});
            skLineSegment(sketch, "E12.308.0.4", {"start": v(15.87, 100.1) * mm, "end": v(20.27, 97.57) * mm});
            skLineSegment(sketch, "E12.311.0.4", {"start": v(45.44, 101.2) * mm, "end": v(41.04, 98.67) * mm});
            skLineSegment(sketch, "E12.314.0.4", {"start": v(76.92, 101.2) * mm, "end": v(76.92, 106.29) * mm});
            skLineSegment(sketch, "E12.317.0.4", {"start": v(1.4, 92.49) * mm, "end": v(1.4, 97.57) * mm});
            skLineSegment(sketch, "E12.320.0.4", {"start": v(10.2, 97.57) * mm, "end": v(10.2, 92.49) * mm});
            skLineSegment(sketch, "E12.323.0.4", {"start": v(20.9, 98.67) * mm, "end": v(16.5, 101.2) * mm});
            skLineSegment(sketch, "E12.326.0.4", {"start": v(25.3, 106.29) * mm, "end": v(25.3, 101.2) * mm});
            skCircle(sketch, "E12.329.0.4", {"center": v(15.87, 95.03) * mm, "radius": 5.08 * mm, "construction": true});
            skLineSegment(sketch, "E12.331.0.4", {"start": v(0.13, 97.57) * mm, "end": v(0.13, 92.49) * mm});
            skLineSegment(sketch, "E12.334.0.4", {"start": v(36, 100.1) * mm, "end": v(40.4, 97.57) * mm});
            skLineSegment(sketch, "E12.337.0.4", {"start": v(-8.67, 92.49) * mm, "end": v(1.4, 92.49) * mm, "construction": true});
            skLineSegment(sketch, "E12.340.0.4", {"start": v(41.04, 98.67) * mm, "end": v(36.64, 101.2) * mm});
            skLineSegment(sketch, "E12.343.0.4", {"start": v(11.47, 97.57) * mm, "end": v(15.87, 100.1) * mm});
            skLineSegment(sketch, "E12.346.0.4", {"start": v(41.68, 92.49) * mm, "end": v(41.68, 97.57) * mm});
            skLineSegment(sketch, "E12.349.0.4", {"start": v(6.44, 101.2) * mm, "end": v(6.44, 106.29) * mm});
            skLineSegment(sketch, "E12.352.0.4", {"start": v(51.75, 97.57) * mm, "end": v(56.15, 100.1) * mm});
            skLineSegment(sketch, "E12.355.0.4", {"start": v(40.4, 97.57) * mm, "end": v(40.4, 92.49) * mm});
            skLineSegment(sketch, "E12.358.0.4", {"start": v(25.3, 101.2) * mm, "end": v(20.9, 98.67) * mm});
            skLineSegment(sketch, "E12.361.0.4", {"start": v(70.62, 97.57) * mm, "end": v(70.62, 92.49) * mm});
            skLineSegment(sketch, "E12.364.0.4", {"start": v(35.37, 101.2) * mm, "end": v(30.98, 98.67) * mm});
            skLineSegment(sketch, "E12.367.0.4", {"start": v(46.08, 100.1) * mm, "end": v(50.48, 97.57) * mm});
            skLineSegment(sketch, "E12.370.0.4", {"start": v(21.54, 92.49) * mm, "end": v(21.54, 97.57) * mm});
            skLineSegment(sketch, "E12.373.0.4", {"start": v(35.37, 106.29) * mm, "end": v(35.37, 101.2) * mm});
            skLineSegment(sketch, "E12.376.0.4", {"start": v(85.72, 101.2) * mm, "end": v(81.32, 98.67) * mm});
            skLineSegment(sketch, "E12.379.0.4", {"start": v(71.89, 97.57) * mm, "end": v(76.28, 100.1) * mm});
            skLineSegment(sketch, "E12.382.0.4", {"start": v(21.54, 97.57) * mm, "end": v(25.94, 100.1) * mm});
            skLineSegment(sketch, "E12.385.0.4", {"start": v(91.39, 98.67) * mm, "end": v(86.99, 101.2) * mm});
            skLineSegment(sketch, "E12.388.0.4", {"start": v(75.65, 106.29) * mm, "end": v(75.65, 101.2) * mm});
            skLineSegment(sketch, "E12.391.0.4", {"start": v(15.24, 101.2) * mm, "end": v(10.84, 98.67) * mm});
            skLineSegment(sketch, "E12.394.0.4", {"start": v(36.64, 101.2) * mm, "end": v(36.64, 106.29) * mm});
            skLineSegment(sketch, "E12.397.0.4", {"start": v(5.8, 100.1) * mm, "end": v(10.2, 97.57) * mm});
            skLineSegment(sketch, "E12.400.0.4", {"start": v(25.94, 100.1) * mm, "end": v(30.34, 97.57) * mm});
            skLineSegment(sketch, "E12.403.0.4", {"start": v(11.47, 92.49) * mm, "end": v(11.47, 97.57) * mm});
            skLineSegment(sketch, "E12.406.0.4", {"start": v(0.77, 98.67) * mm, "end": v(1.4, 97.57) * mm, "construction": true});
            skLineSegment(sketch, "E12.409.0.4", {"start": v(-4.27, 100.1) * mm, "end": v(0.13, 97.57) * mm});
            skLineSegment(sketch, "E12.412.0.4", {"start": v(0.77, 98.67) * mm, "end": v(-3.63, 101.2) * mm});
            skLineSegment(sketch, "E12.415.0.4", {"start": v(0.13, 97.57) * mm, "end": v(1.4, 97.57) * mm, "construction": true});
            skLineSegment(sketch, "E12.418.0.4", {"start": v(0.13, 97.57) * mm, "end": v(0.77, 98.67) * mm, "construction": true});
            skSolve(sketch);
        }
        {
            var Q0;
            Q0 = qSketchRegion(id + "F0", true);
            extrude(context, id + "F1", {"entities" : qUnion([Q0]), "depth" : 1.27 * mm});
        }
        {
            var Q0;
            Q0=makeQuery(id+"F1.opExtrude","CAP_FACE",FACE,{"disambiguationData":[OSD([sQuery(id+"F0.wireOp",EDGE,"E0.0"),sQuery(id+"F0.wireOp",EDGE,"E0.1"),sQuery(id+"F0.wireOp",EDGE,"E0.2"),sQuery(id+"F0.wireOp",EDGE,"E0.3"),sQuery(id+"F0.wireOp",EDGE,"E0.4"),sQuery(id+"F0.wireOp",EDGE,"E0.5"),sQuery(id+"F0.wireOp",EDGE,"E1.1.0.0"),sQuery(id+"F0.wireOp",EDGE,"E1.1.0.1"),sQuery(id+"F0.wireOp",EDGE,"E1.1.0.2"),sQuery(id+"F0.wireOp",EDGE,"E1.1.0.3"),sQuery(id+"F0.wireOp",EDGE,"E1.1.0.4"),sQuery(id+"F0.wireOp",EDGE,"E1.1.0.5"),sQuery(id+"F0.wireOp",EDGE,"E1.2.0.0"),sQuery(id+"F0.wireOp",EDGE,"E1.2.0.1"),sQuery(id+"F0.wireOp",EDGE,"E1.2.0.2"),sQuery(id+"F0.wireOp",EDGE,"E1.2.0.3"),sQuery(id+"F0.wireOp",EDGE,"E1.2.0.4"),sQuery(id+"F0.wireOp",EDGE,"E1.2.0.5"),sQuery(id+"F0.wireOp",EDGE,"0f33f7c7-d985-4434-8b08-4c21ebd6a896.0.3.0"),sQuery(id+"F0.wireOp",EDGE,"0f33f7c7-d985-4434-8b08-4c21ebd6a896.3.3.0"),sQuery(id+"F0.wireOp",EDGE,"0f33f7c7-d985-4434-8b08-4c21ebd6a896.6.3.0"),sQuery(id+"F0.wireOp",EDGE,"0f33f7c7-d985-4434-8b08-4c21ebd6a896.9.3.0"),sQuery(id+"F0.wireOp",EDGE,"0f33f7c7-d985-4434-8b08-4c21ebd6a896.12.3.0"),sQuery(id+"F0.wireOp",EDGE,"0f33f7c7-d985-4434-8b08-4c21ebd6a896.15.3.0"),sQuery(id+"F0.wireOp",EDGE,"0f33f7c7-d985-4434-8b08-4c21ebd6a896.0.4.0"),sQuery(id+"F0.wireOp",EDGE,"0f33f7c7-d985-4434-8b08-4c21ebd6a896.3.4.0"),sQuery(id+"F0.wireOp",EDGE,"0f33f7c7-d985-4434-8b08-4c21ebd6a896.6.4.0"),sQuery(id+"F0.wireOp",EDGE,"0f33f7c7-d985-4434-8b08-4c21ebd6a896.9.4.0"),sQuery(id+"F0.wireOp",EDGE,"0f33f7c7-d985-4434-8b08-4c21ebd6a896.12.4.0"),sQuery(id+"F0.wireOp",EDGE,"0f33f7c7-d985-4434-8b08-4c21ebd6a896.15.4.0"),sQuery(id+"F0.wireOp",EDGE,"0f33f7c7-d985-4434-8b08-4c21ebd6a896.0.5.0"),sQuery(id+"F0.wireOp",EDGE,"0f33f7c7-d985-4434-8b08-4c21ebd6a896.3.5.0"),sQuery(id+"F0.wireOp",EDGE,"0f33f7c7-d985-4434-8b08-4c21ebd6a896.6.5.0"),sQuery(id+"F0.wireOp",EDGE,"0f33f7c7-d985-4434-8b08-4c21ebd6a896.9.5.0"),sQuery(id+"F0.wireOp",EDGE,"0f33f7c7-d985-4434-8b08-4c21ebd6a896.12.5.0"),sQuery(id+"F0.wireOp",EDGE,"0f33f7c7-d985-4434-8b08-4c21ebd6a896.15.5.0"),sQuery(id+"F0.wireOp",EDGE,"0f33f7c7-d985-4434-8b08-4c21ebd6a896.0.6.0"),sQuery(id+"F0.wireOp",EDGE,"0f33f7c7-d985-4434-8b08-4c21ebd6a896.3.6.0"),sQuery(id+"F0.wireOp",EDGE,"0f33f7c7-d985-4434-8b08-4c21ebd6a896.6.6.0"),sQuery(id+"F0.wireOp",EDGE,"0f33f7c7-d985-4434-8b08-4c21ebd6a896.9.6.0"),sQuery(id+"F0.wireOp",EDGE,"0f33f7c7-d985-4434-8b08-4c21ebd6a896.12.6.0"),sQuery(id+"F0.wireOp",EDGE,"0f33f7c7-d985-4434-8b08-4c21ebd6a896.15.6.0"),sQuery(id+"F0.wireOp",EDGE,"0f33f7c7-d985-4434-8b08-4c21ebd6a896.0.7.0"),sQuery(id+"F0.wireOp",EDGE,"0f33f7c7-d985-4434-8b08-4c21ebd6a896.3.7.0"),sQuery(id+"F0.wireOp",EDGE,"0f33f7c7-d985-4434-8b08-4c21ebd6a896.6.7.0"),sQuery(id+"F0.wireOp",EDGE,"0f33f7c7-d985-4434-8b08-4c21ebd6a896.9.7.0"),sQuery(id+"F0.wireOp",EDGE,"0f33f7c7-d985-4434-8b08-4c21ebd6a896.12.7.0"),sQuery(id+"F0.wireOp",EDGE,"0f33f7c7-d985-4434-8b08-4c21ebd6a896.15.7.0"),sQuery(id+"F0.wireOp",EDGE,"0f33f7c7-d985-4434-8b08-4c21ebd6a896.0.8.0"),sQuery(id+"F0.wireOp",EDGE,"0f33f7c7-d985-4434-8b08-4c21ebd6a896.3.8.0"),sQuery(id+"F0.wireOp",EDGE,"0f33f7c7-d985-4434-8b08-4c21ebd6a896.6.8.0"),sQuery(id+"F0.wireOp",EDGE,"0f33f7c7-d985-4434-8b08-4c21ebd6a896.9.8.0"),sQuery(id+"F0.wireOp",EDGE,"0f33f7c7-d985-4434-8b08-4c21ebd6a896.12.8.0"),sQuery(id+"F0.wireOp",EDGE,"0f33f7c7-d985-4434-8b08-4c21ebd6a896.15.8.0"),sQuery(id+"F0.wireOp",EDGE,"0f33f7c7-d985-4434-8b08-4c21ebd6a896.0.9.0"),sQuery(id+"F0.wireOp",EDGE,"0f33f7c7-d985-4434-8b08-4c21ebd6a896.3.9.0"),sQuery(id+"F0.wireOp",EDGE,"0f33f7c7-d985-4434-8b08-4c21ebd6a896.6.9.0"),sQuery(id+"F0.wireOp",EDGE,"0f33f7c7-d985-4434-8b08-4c21ebd6a896.9.9.0"),sQuery(id+"F0.wireOp",EDGE,"0f33f7c7-d985-4434-8b08-4c21ebd6a896.12.9.0"),sQuery(id+"F0.wireOp",EDGE,"0f33f7c7-d985-4434-8b08-4c21ebd6a896.15.9.0"),sQuery(id+"F0.wireOp",EDGE,"E2.0.1.1"),sQuery(id+"F0.wireOp",EDGE,"E2.0.1.2"),sQuery(id+"F0.wireOp",EDGE,"E2.0.1.3"),sQuery(id+"F0.wireOp",EDGE,"E2.0.1.5"),sQuery(id+"F0.wireOp",EDGE,"E2.0.1.7"),sQuery(id+"F0.wireOp",EDGE,"E2.0.1.8"),sQuery(id+"F0.wireOp",EDGE,"E2.0.1.9"),sQuery(id+"F0.wireOp",EDGE,"E2.0.1.10"),sQuery(id+"F0.wireOp",EDGE,"E2.0.1.11"),sQuery(id+"F0.wireOp",EDGE,"E2.0.1.12"),sQuery(id+"F0.wireOp",EDGE,"E2.0.1.14"),sQuery(id+"F0.wireOp",EDGE,"E2.0.1.15"),sQuery(id+"F0.wireOp",EDGE,"E2.0.1.16"),sQuery(id+"F0.wireOp",EDGE,"E2.0.1.17"),sQuery(id+"F0.wireOp",EDGE,"E2.0.1.18"),sQuery(id+"F0.wireOp",EDGE,"E2.0.1.19"),sQuery(id+"F0.wireOp",EDGE,"E2.0.1.21"),sQuery(id+"F0.wireOp",EDGE,"E2.0.1.22"),sQuery(id+"F0.wireOp",EDGE,"E2.0.1.23"),sQuery(id+"F0.wireOp",EDGE,"E2.0.1.24"),sQuery(id+"F0.wireOp",EDGE,"E2.0.1.25"),sQuery(id+"F0.wireOp",EDGE,"E2.0.1.26"),sQuery(id+"F0.wireOp",EDGE,"E2.0.1.28"),sQuery(id+"F0.wireOp",EDGE,"E2.0.1.29"),sQuery(id+"F0.wireOp",EDGE,"E2.0.1.30"),sQuery(id+"F0.wireOp",EDGE,"E2.0.1.31"),sQuery(id+"F0.wireOp",EDGE,"E2.0.1.32"),sQuery(id+"F0.wireOp",EDGE,"E2.0.1.33"),sQuery(id+"F0.wireOp",EDGE,"E2.0.1.35"),sQuery(id+"F0.wireOp",EDGE,"E2.0.1.36"),sQuery(id+"F0.wireOp",EDGE,"E2.0.1.37"),sQuery(id+"F0.wireOp",EDGE,"E2.0.1.38"),sQuery(id+"F0.wireOp",EDGE,"E2.0.1.39"),sQuery(id+"F0.wireOp",EDGE,"E2.0.1.40"),sQuery(id+"F0.wireOp",EDGE,"E2.0.1.41"),sQuery(id+"F0.wireOp",EDGE,"E2.0.1.42"),sQuery(id+"F0.wireOp",EDGE,"E2.0.1.44"),sQuery(id+"F0.wireOp",EDGE,"E2.0.1.46"),sQuery(id+"F0.wireOp",EDGE,"E2.0.1.47"),sQuery(id+"F0.wireOp",EDGE,"E2.0.1.48"),sQuery(id+"F0.wireOp",EDGE,"E2.0.1.49"),sQuery(id+"F0.wireOp",EDGE,"E2.0.1.51"),sQuery(id+"F0.wireOp",EDGE,"E2.0.1.52"),sQuery(id+"F0.wireOp",EDGE,"E2.0.1.53"),sQuery(id+"F0.wireOp",EDGE,"E2.0.1.54"),sQuery(id+"F0.wireOp",EDGE,"E2.0.1.55"),sQuery(id+"F0.wireOp",EDGE,"E2.0.1.56"),sQuery(id+"F0.wireOp",EDGE,"E2.0.1.57"),sQuery(id+"F0.wireOp",EDGE,"E2.0.1.58"),sQuery(id+"F0.wireOp",EDGE,"E2.0.1.60"),sQuery(id+"F0.wireOp",EDGE,"E2.0.1.61"),sQuery(id+"F0.wireOp",EDGE,"E2.0.1.62"),sQuery(id+"F0.wireOp",EDGE,"E2.0.1.63"),sQuery(id+"F0.wireOp",EDGE,"E2.0.1.64"),sQuery(id+"F0.wireOp",EDGE,"E2.0.1.65"),sQuery(id+"F0.wireOp",EDGE,"E2.0.1.66"),sQuery(id+"F0.wireOp",EDGE,"E2.0.1.67"),sQuery(id+"F0.wireOp",EDGE,"E2.0.1.68"),sQuery(id+"F0.wireOp",EDGE,"E2.0.1.69"),sQuery(id+"F0.wireOp",EDGE,"E2.0.1.70"),sQuery(id+"F0.wireOp",EDGE,"E6.0.1.2"),sQuery(id+"F0.wireOp",EDGE,"E6.0.1.4"),sQuery(id+"F0.wireOp",EDGE,"E6.0.1.8"),sQuery(id+"F0.wireOp",EDGE,"E6.0.1.10"),sQuery(id+"F0.wireOp",EDGE,"E6.0.1.11"),sQuery(id+"F0.wireOp",EDGE,"E6.0.1.12"),sQuery(id+"F0.wireOp",EDGE,"E6.0.1.13"),sQuery(id+"F0.wireOp",EDGE,"E6.0.1.14"),sQuery(id+"F0.wireOp",EDGE,"E6.0.1.15"),sQuery(id+"F0.wireOp",EDGE,"E6.0.1.16"),sQuery(id+"F0.wireOp",EDGE,"E6.0.1.17"),sQuery(id+"F0.wireOp",EDGE,"E6.0.1.18"),sQuery(id+"F0.wireOp",EDGE,"E6.0.1.20"),sQuery(id+"F0.wireOp",EDGE,"E6.0.1.21"),sQuery(id+"F0.wireOp",EDGE,"E6.0.1.22"),sQuery(id+"F0.wireOp",EDGE,"E6.0.1.23"),sQuery(id+"F0.wireOp",EDGE,"E6.0.1.24"),sQuery(id+"F0.wireOp",EDGE,"E6.0.1.25"),sQuery(id+"F0.wireOp",EDGE,"E6.0.1.26"),sQuery(id+"F0.wireOp",EDGE,"E6.0.1.27"),sQuery(id+"F0.wireOp",EDGE,"E6.0.1.28"),sQuery(id+"F0.wireOp",EDGE,"E6.0.1.29"),sQuery(id+"F0.wireOp",EDGE,"E6.0.1.30"),sQuery(id+"F0.wireOp",EDGE,"E6.0.1.31"),sQuery(id+"F0.wireOp",EDGE,"E6.0.1.33"),sQuery(id+"F0.wireOp",EDGE,"E6.0.1.34"),sQuery(id+"F0.wireOp",EDGE,"E6.0.1.36"),sQuery(id+"F0.wireOp",EDGE,"E6.0.1.37"),sQuery(id+"F0.wireOp",EDGE,"E6.0.1.38"),sQuery(id+"F0.wireOp",EDGE,"E6.0.1.39"),sQuery(id+"F0.wireOp",EDGE,"E6.0.1.41"),sQuery(id+"F0.wireOp",EDGE,"E6.0.1.42"),sQuery(id+"F0.wireOp",EDGE,"E6.0.1.43"),sQuery(id+"F0.wireOp",EDGE,"E6.0.1.44"),sQuery(id+"F0.wireOp",EDGE,"E6.0.1.46"),sQuery(id+"F0.wireOp",EDGE,"E6.0.1.48"),sQuery(id+"F0.wireOp",EDGE,"E6.0.1.49"),sQuery(id+"F0.wireOp",EDGE,"E6.0.1.51"),sQuery(id+"F0.wireOp",EDGE,"E6.0.1.52"),sQuery(id+"F0.wireOp",EDGE,"E6.0.1.53"),sQuery(id+"F0.wireOp",EDGE,"E6.0.1.54"),sQuery(id+"F0.wireOp",EDGE,"E6.0.1.55"),sQuery(id+"F0.wireOp",EDGE,"E6.0.1.57"),sQuery(id+"F0.wireOp",EDGE,"E6.0.1.59"),sQuery(id+"F0.wireOp",EDGE,"E6.0.1.60"),sQuery(id+"F0.wireOp",EDGE,"E6.0.1.62"),sQuery(id+"F0.wireOp",EDGE,"E6.0.1.63"),sQuery(id+"F0.wireOp",EDGE,"E6.0.1.64"),sQuery(id+"F0.wireOp",EDGE,"E6.0.1.65"),sQuery(id+"F0.wireOp",EDGE,"E6.0.1.66"),sQuery(id+"F0.wireOp",EDGE,"E6.0.1.67"),sQuery(id+"F0.wireOp",EDGE,"E6.0.1.68"),sQuery(id+"F0.wireOp",EDGE,"E6.0.1.70"),sQuery(id+"F0.wireOp",EDGE,"E6.0.1.71"),sQuery(id+"F0.wireOp",EDGE,"E6.0.1.72"),sQuery(id+"F0.wireOp",EDGE,"E6.0.1.73"),sQuery(id+"F0.wireOp",EDGE,"E6.0.1.75"),sQuery(id+"F0.wireOp",EDGE,"E6.0.1.76"),sQuery(id+"F0.wireOp",EDGE,"E6.0.1.77"),sQuery(id+"F0.wireOp",EDGE,"E6.0.1.78"),sQuery(id+"F0.wireOp",EDGE,"E6.0.1.80"),sQuery(id+"F0.wireOp",EDGE,"E6.0.1.81"),sQuery(id+"F0.wireOp",EDGE,"E6.0.1.82"),sQuery(id+"F0.wireOp",EDGE,"E6.0.1.83"),sQuery(id+"F0.wireOp",EDGE,"E6.0.1.85"),sQuery(id+"F0.wireOp",EDGE,"E6.0.1.86"),sQuery(id+"F0.wireOp",EDGE,"E6.0.1.87"),sQuery(id+"F0.wireOp",EDGE,"E6.0.1.88"),sQuery(id+"F0.wireOp",EDGE,"E6.0.1.89"),sQuery(id+"F0.wireOp",EDGE,"E6.0.1.90"),sQuery(id+"F0.wireOp",EDGE,"E6.0.1.91"),sQuery(id+"F0.wireOp",EDGE,"E6.0.1.92"),sQuery(id+"F0.wireOp",EDGE,"E6.0.1.94"),sQuery(id+"F0.wireOp",EDGE,"E6.0.1.95"),sQuery(id+"F0.wireOp",EDGE,"E6.0.1.96"),sQuery(id+"F0.wireOp",EDGE,"E6.0.1.97"),sQuery(id+"F0.wireOp",EDGE,"E6.0.1.98"),sQuery(id+"F0.wireOp",EDGE,"E6.0.1.99"),sQuery(id+"F0.wireOp",EDGE,"E6.0.1.100"),sQuery(id+"F0.wireOp",EDGE,"E6.0.1.101"),sQuery(id+"F0.wireOp",EDGE,"E6.0.1.102"),sQuery(id+"F0.wireOp",EDGE,"E6.0.1.103"),sQuery(id+"F0.wireOp",EDGE,"E6.0.1.104"),sQuery(id+"F0.wireOp",EDGE,"E6.0.1.105"),sQuery(id+"F0.wireOp",EDGE,"E6.0.1.106"),sQuery(id+"F0.wireOp",EDGE,"E6.0.1.107"),sQuery(id+"F0.wireOp",EDGE,"E6.0.1.108"),sQuery(id+"F0.wireOp",EDGE,"E6.0.1.109"),sQuery(id+"F0.wireOp",EDGE,"E6.0.1.110"),sQuery(id+"F0.wireOp",EDGE,"E6.0.1.111"),sQuery(id+"F0.wireOp",EDGE,"E6.0.1.112"),sQuery(id+"F0.wireOp",EDGE,"E6.0.1.113"),sQuery(id+"F0.wireOp",EDGE,"E6.0.1.114"),sQuery(id+"F0.wireOp",EDGE,"E6.0.1.115"),sQuery(id+"F0.wireOp",EDGE,"E6.0.1.117"),sQuery(id+"F0.wireOp",EDGE,"E6.0.1.118"),sQuery(id+"F0.wireOp",EDGE,"E6.0.1.120"),sQuery(id+"F0.wireOp",EDGE,"E6.0.1.121"),sQuery(id+"F0.wireOp",EDGE,"E6.0.1.122"),sQuery(id+"F0.wireOp",EDGE,"E6.0.1.123"),sQuery(id+"F0.wireOp",EDGE,"E6.0.1.124"),sQuery(id+"F0.wireOp",EDGE,"E6.0.1.125"),sQuery(id+"F0.wireOp",EDGE,"E6.0.1.126"),sQuery(id+"F0.wireOp",EDGE,"E6.0.1.127"),sQuery(id+"F0.wireOp",EDGE,"E6.0.1.128"),sQuery(id+"F0.wireOp",EDGE,"E6.0.1.129"),sQuery(id+"F0.wireOp",EDGE,"E6.0.1.130"),sQuery(id+"F0.wireOp",EDGE,"E6.0.1.131"),sQuery(id+"F0.wireOp",EDGE,"E6.0.1.132"),sQuery(id+"F0.wireOp",EDGE,"E6.0.1.133"),sQuery(id+"F0.wireOp",EDGE,"E6.0.1.134"),sQuery(id+"F0.wireOp",EDGE,"E6.0.1.135"),sQuery(id+"F0.wireOp",EDGE,"E6.0.1.136"),sQuery(id+"F0.wireOp",EDGE,"E6.0.1.137"),sQuery(id+"F0.wireOp",EDGE,"E6.0.1.138"),sQuery(id+"F0.wireOp",EDGE,"E6.0.1.139"),sQuery(id+"F0.wireOp",EDGE,"E6.0.1.140"),sQuery(id+"F0.wireOp",EDGE,"E6.0.1.141"),sQuery(id+"F0.wireOp",EDGE,"E6.0.1.143"),sQuery(id+"F0.wireOp",EDGE,"E6.0.1.144"),sQuery(id+"F0.wireOp",EDGE,"E6.0.2.2"),sQuery(id+"F0.wireOp",EDGE,"E6.0.2.4"),sQuery(id+"F0.wireOp",EDGE,"E6.0.2.8"),sQuery(id+"F0.wireOp",EDGE,"E6.0.2.10"),sQuery(id+"F0.wireOp",EDGE,"E6.0.2.11"),sQuery(id+"F0.wireOp",EDGE,"E6.0.2.12"),sQuery(id+"F0.wireOp",EDGE,"E6.0.2.13"),sQuery(id+"F0.wireOp",EDGE,"E6.0.2.14"),sQuery(id+"F0.wireOp",EDGE,"E6.0.2.15"),sQuery(id+"F0.wireOp",EDGE,"E6.0.2.16"),sQuery(id+"F0.wireOp",EDGE,"E6.0.2.17"),sQuery(id+"F0.wireOp",EDGE,"E6.0.2.18"),sQuery(id+"F0.wireOp",EDGE,"E6.0.2.20"),sQuery(id+"F0.wireOp",EDGE,"E6.0.2.21"),sQuery(id+"F0.wireOp",EDGE,"E6.0.2.22"),sQuery(id+"F0.wireOp",EDGE,"E6.0.2.23"),sQuery(id+"F0.wireOp",EDGE,"E6.0.2.24"),sQuery(id+"F0.wireOp",EDGE,"E6.0.2.25"),sQuery(id+"F0.wireOp",EDGE,"E6.0.2.26"),sQuery(id+"F0.wireOp",EDGE,"E6.0.2.27"),sQuery(id+"F0.wireOp",EDGE,"E6.0.2.28"),sQuery(id+"F0.wireOp",EDGE,"E6.0.2.29"),sQuery(id+"F0.wireOp",EDGE,"E6.0.2.30"),sQuery(id+"F0.wireOp",EDGE,"E6.0.2.31"),sQuery(id+"F0.wireOp",EDGE,"E6.0.2.33"),sQuery(id+"F0.wireOp",EDGE,"E6.0.2.34"),sQuery(id+"F0.wireOp",EDGE,"E6.0.2.36"),sQuery(id+"F0.wireOp",EDGE,"E6.0.2.37"),sQuery(id+"F0.wireOp",EDGE,"E6.0.2.38"),sQuery(id+"F0.wireOp",EDGE,"E6.0.2.39"),sQuery(id+"F0.wireOp",EDGE,"E6.0.2.41"),sQuery(id+"F0.wireOp",EDGE,"E6.0.2.42"),sQuery(id+"F0.wireOp",EDGE,"E6.0.2.43"),sQuery(id+"F0.wireOp",EDGE,"E6.0.2.44"),sQuery(id+"F0.wireOp",EDGE,"E6.0.2.46"),sQuery(id+"F0.wireOp",EDGE,"E6.0.2.48"),sQuery(id+"F0.wireOp",EDGE,"E6.0.2.49"),sQuery(id+"F0.wireOp",EDGE,"E6.0.2.51"),sQuery(id+"F0.wireOp",EDGE,"E6.0.2.52"),sQuery(id+"F0.wireOp",EDGE,"E6.0.2.53"),sQuery(id+"F0.wireOp",EDGE,"E6.0.2.54"),sQuery(id+"F0.wireOp",EDGE,"E6.0.2.55"),sQuery(id+"F0.wireOp",EDGE,"E6.0.2.57"),sQuery(id+"F0.wireOp",EDGE,"E6.0.2.59"),sQuery(id+"F0.wireOp",EDGE,"E6.0.2.60"),sQuery(id+"F0.wireOp",EDGE,"E6.0.2.62"),sQuery(id+"F0.wireOp",EDGE,"E6.0.2.63"),sQuery(id+"F0.wireOp",EDGE,"E6.0.2.64"),sQuery(id+"F0.wireOp",EDGE,"E6.0.2.65"),sQuery(id+"F0.wireOp",EDGE,"E6.0.2.66"),sQuery(id+"F0.wireOp",EDGE,"E6.0.2.67"),sQuery(id+"F0.wireOp",EDGE,"E6.0.2.68"),sQuery(id+"F0.wireOp",EDGE,"E6.0.2.70"),sQuery(id+"F0.wireOp",EDGE,"E6.0.2.71"),sQuery(id+"F0.wireOp",EDGE,"E6.0.2.72"),sQuery(id+"F0.wireOp",EDGE,"E6.0.2.73"),sQuery(id+"F0.wireOp",EDGE,"E6.0.2.75"),sQuery(id+"F0.wireOp",EDGE,"E6.0.2.76"),sQuery(id+"F0.wireOp",EDGE,"E6.0.2.77"),sQuery(id+"F0.wireOp",EDGE,"E6.0.2.78"),sQuery(id+"F0.wireOp",EDGE,"E6.0.2.80"),sQuery(id+"F0.wireOp",EDGE,"E6.0.2.81"),sQuery(id+"F0.wireOp",EDGE,"E6.0.2.82"),sQuery(id+"F0.wireOp",EDGE,"E6.0.2.83"),sQuery(id+"F0.wireOp",EDGE,"E6.0.2.85"),sQuery(id+"F0.wireOp",EDGE,"E6.0.2.86"),sQuery(id+"F0.wireOp",EDGE,"E6.0.2.87"),sQuery(id+"F0.wireOp",EDGE,"E6.0.2.88"),sQuery(id+"F0.wireOp",EDGE,"E6.0.2.89"),sQuery(id+"F0.wireOp",EDGE,"E6.0.2.90"),sQuery(id+"F0.wireOp",EDGE,"E6.0.2.91"),sQuery(id+"F0.wireOp",EDGE,"E6.0.2.92"),sQuery(id+"F0.wireOp",EDGE,"E6.0.2.94"),sQuery(id+"F0.wireOp",EDGE,"E6.0.2.95"),sQuery(id+"F0.wireOp",EDGE,"E6.0.2.96"),sQuery(id+"F0.wireOp",EDGE,"E6.0.2.97"),sQuery(id+"F0.wireOp",EDGE,"E6.0.2.98"),sQuery(id+"F0.wireOp",EDGE,"E6.0.2.99"),sQuery(id+"F0.wireOp",EDGE,"E6.0.2.100"),sQuery(id+"F0.wireOp",EDGE,"E6.0.2.101"),sQuery(id+"F0.wireOp",EDGE,"E6.0.2.102"),sQuery(id+"F0.wireOp",EDGE,"E6.0.2.103"),sQuery(id+"F0.wireOp",EDGE,"E6.0.2.104"),sQuery(id+"F0.wireOp",EDGE,"E6.0.2.105"),sQuery(id+"F0.wireOp",EDGE,"E6.0.2.106"),sQuery(id+"F0.wireOp",EDGE,"E6.0.2.107"),sQuery(id+"F0.wireOp",EDGE,"E6.0.2.108"),sQuery(id+"F0.wireOp",EDGE,"E6.0.2.109"),sQuery(id+"F0.wireOp",EDGE,"E6.0.2.110"),sQuery(id+"F0.wireOp",EDGE,"E6.0.2.111"),sQuery(id+"F0.wireOp",EDGE,"E6.0.2.112"),sQuery(id+"F0.wireOp",EDGE,"E6.0.2.113"),sQuery(id+"F0.wireOp",EDGE,"E6.0.2.114"),sQuery(id+"F0.wireOp",EDGE,"E6.0.2.115"),sQuery(id+"F0.wireOp",EDGE,"E6.0.2.117"),sQuery(id+"F0.wireOp",EDGE,"E6.0.2.118"),sQuery(id+"F0.wireOp",EDGE,"E6.0.2.120"),sQuery(id+"F0.wireOp",EDGE,"E6.0.2.121"),sQuery(id+"F0.wireOp",EDGE,"E6.0.2.122"),sQuery(id+"F0.wireOp",EDGE,"E6.0.2.123"),sQuery(id+"F0.wireOp",EDGE,"E6.0.2.124"),sQuery(id+"F0.wireOp",EDGE,"E6.0.2.125"),sQuery(id+"F0.wireOp",EDGE,"E6.0.2.126"),sQuery(id+"F0.wireOp",EDGE,"E6.0.2.127"),sQuery(id+"F0.wireOp",EDGE,"E6.0.2.128"),sQuery(id+"F0.wireOp",EDGE,"E6.0.2.129"),sQuery(id+"F0.wireOp",EDGE,"E6.0.2.130"),sQuery(id+"F0.wireOp",EDGE,"E6.0.2.131"),sQuery(id+"F0.wireOp",EDGE,"E6.0.2.132"),sQuery(id+"F0.wireOp",EDGE,"E6.0.2.133"),sQuery(id+"F0.wireOp",EDGE,"E6.0.2.134"),sQuery(id+"F0.wireOp",EDGE,"E6.0.2.135"),sQuery(id+"F0.wireOp",EDGE,"E6.0.2.136"),sQuery(id+"F0.wireOp",EDGE,"E6.0.2.137"),sQuery(id+"F0.wireOp",EDGE,"E6.0.2.138"),sQuery(id+"F0.wireOp",EDGE,"E6.0.2.139"),sQuery(id+"F0.wireOp",EDGE,"E6.0.2.140"),sQuery(id+"F0.wireOp",EDGE,"E6.0.2.141"),sQuery(id+"F0.wireOp",EDGE,"E6.0.2.143"),sQuery(id+"F0.wireOp",EDGE,"E6.0.2.144"),sQuery(id+"F0.wireOp",EDGE,"E6.0.3.2"),sQuery(id+"F0.wireOp",EDGE,"E6.0.3.4"),sQuery(id+"F0.wireOp",EDGE,"E6.0.3.8"),sQuery(id+"F0.wireOp",EDGE,"E6.0.3.10"),sQuery(id+"F0.wireOp",EDGE,"E6.0.3.11"),sQuery(id+"F0.wireOp",EDGE,"E6.0.3.12"),sQuery(id+"F0.wireOp",EDGE,"E6.0.3.13"),sQuery(id+"F0.wireOp",EDGE,"E6.0.3.14"),sQuery(id+"F0.wireOp",EDGE,"E6.0.3.15"),sQuery(id+"F0.wireOp",EDGE,"E6.0.3.16"),sQuery(id+"F0.wireOp",EDGE,"E6.0.3.17"),sQuery(id+"F0.wireOp",EDGE,"E6.0.3.18"),sQuery(id+"F0.wireOp",EDGE,"E6.0.3.20"),sQuery(id+"F0.wireOp",EDGE,"E6.0.3.21"),sQuery(id+"F0.wireOp",EDGE,"E6.0.3.22"),sQuery(id+"F0.wireOp",EDGE,"E6.0.3.23"),sQuery(id+"F0.wireOp",EDGE,"E6.0.3.24"),sQuery(id+"F0.wireOp",EDGE,"E6.0.3.25"),sQuery(id+"F0.wireOp",EDGE,"E6.0.3.26"),sQuery(id+"F0.wireOp",EDGE,"E6.0.3.27"),sQuery(id+"F0.wireOp",EDGE,"E6.0.3.28"),sQuery(id+"F0.wireOp",EDGE,"E6.0.3.29"),sQuery(id+"F0.wireOp",EDGE,"E6.0.3.30"),sQuery(id+"F0.wireOp",EDGE,"E6.0.3.31"),sQuery(id+"F0.wireOp",EDGE,"E6.0.3.33"),sQuery(id+"F0.wireOp",EDGE,"E6.0.3.34"),sQuery(id+"F0.wireOp",EDGE,"E6.0.3.36"),sQuery(id+"F0.wireOp",EDGE,"E6.0.3.37"),sQuery(id+"F0.wireOp",EDGE,"E6.0.3.38"),sQuery(id+"F0.wireOp",EDGE,"E6.0.3.39"),sQuery(id+"F0.wireOp",EDGE,"E6.0.3.41"),sQuery(id+"F0.wireOp",EDGE,"E6.0.3.42"),sQuery(id+"F0.wireOp",EDGE,"E6.0.3.43"),sQuery(id+"F0.wireOp",EDGE,"E6.0.3.44"),sQuery(id+"F0.wireOp",EDGE,"E6.0.3.46"),sQuery(id+"F0.wireOp",EDGE,"E6.0.3.48"),sQuery(id+"F0.wireOp",EDGE,"E6.0.3.49"),sQuery(id+"F0.wireOp",EDGE,"E6.0.3.51"),sQuery(id+"F0.wireOp",EDGE,"E6.0.3.52"),sQuery(id+"F0.wireOp",EDGE,"E6.0.3.53"),sQuery(id+"F0.wireOp",EDGE,"E6.0.3.54"),sQuery(id+"F0.wireOp",EDGE,"E6.0.3.55"),sQuery(id+"F0.wireOp",EDGE,"E6.0.3.57"),sQuery(id+"F0.wireOp",EDGE,"E6.0.3.59"),sQuery(id+"F0.wireOp",EDGE,"E6.0.3.60"),sQuery(id+"F0.wireOp",EDGE,"E6.0.3.62"),sQuery(id+"F0.wireOp",EDGE,"E6.0.3.63"),sQuery(id+"F0.wireOp",EDGE,"E6.0.3.64"),sQuery(id+"F0.wireOp",EDGE,"E6.0.3.65"),sQuery(id+"F0.wireOp",EDGE,"E6.0.3.66"),sQuery(id+"F0.wireOp",EDGE,"E6.0.3.67"),sQuery(id+"F0.wireOp",EDGE,"E6.0.3.68"),sQuery(id+"F0.wireOp",EDGE,"E6.0.3.70"),sQuery(id+"F0.wireOp",EDGE,"E6.0.3.71"),sQuery(id+"F0.wireOp",EDGE,"E6.0.3.72"),sQuery(id+"F0.wireOp",EDGE,"E6.0.3.73"),sQuery(id+"F0.wireOp",EDGE,"E6.0.3.75"),sQuery(id+"F0.wireOp",EDGE,"E6.0.3.76"),sQuery(id+"F0.wireOp",EDGE,"E6.0.3.77"),sQuery(id+"F0.wireOp",EDGE,"E6.0.3.78"),sQuery(id+"F0.wireOp",EDGE,"E6.0.3.80"),sQuery(id+"F0.wireOp",EDGE,"E6.0.3.81"),sQuery(id+"F0.wireOp",EDGE,"E6.0.3.82"),sQuery(id+"F0.wireOp",EDGE,"E6.0.3.83"),sQuery(id+"F0.wireOp",EDGE,"E6.0.3.85"),sQuery(id+"F0.wireOp",EDGE,"E6.0.3.86"),sQuery(id+"F0.wireOp",EDGE,"E6.0.3.87"),sQuery(id+"F0.wireOp",EDGE,"E6.0.3.88"),sQuery(id+"F0.wireOp",EDGE,"E6.0.3.89"),sQuery(id+"F0.wireOp",EDGE,"E6.0.3.90"),sQuery(id+"F0.wireOp",EDGE,"E6.0.3.91"),sQuery(id+"F0.wireOp",EDGE,"E6.0.3.92"),sQuery(id+"F0.wireOp",EDGE,"E6.0.3.94"),sQuery(id+"F0.wireOp",EDGE,"E6.0.3.95"),sQuery(id+"F0.wireOp",EDGE,"E6.0.3.96"),sQuery(id+"F0.wireOp",EDGE,"E6.0.3.97"),sQuery(id+"F0.wireOp",EDGE,"E6.0.3.98"),sQuery(id+"F0.wireOp",EDGE,"E6.0.3.99"),sQuery(id+"F0.wireOp",EDGE,"E6.0.3.100"),sQuery(id+"F0.wireOp",EDGE,"E6.0.3.101"),sQuery(id+"F0.wireOp",EDGE,"E6.0.3.102"),sQuery(id+"F0.wireOp",EDGE,"E6.0.3.103"),sQuery(id+"F0.wireOp",EDGE,"E6.0.3.104"),sQuery(id+"F0.wireOp",EDGE,"E6.0.3.105"),sQuery(id+"F0.wireOp",EDGE,"E6.0.3.106"),sQuery(id+"F0.wireOp",EDGE,"E6.0.3.107"),sQuery(id+"F0.wireOp",EDGE,"E6.0.3.108"),sQuery(id+"F0.wireOp",EDGE,"E6.0.3.109"),sQuery(id+"F0.wireOp",EDGE,"E6.0.3.110"),sQuery(id+"F0.wireOp",EDGE,"E6.0.3.111"),sQuery(id+"F0.wireOp",EDGE,"E6.0.3.112"),sQuery(id+"F0.wireOp",EDGE,"E6.0.3.113"),sQuery(id+"F0.wireOp",EDGE,"E6.0.3.114"),sQuery(id+"F0.wireOp",EDGE,"E6.0.3.115"),sQuery(id+"F0.wireOp",EDGE,"E6.0.3.117"),sQuery(id+"F0.wireOp",EDGE,"E6.0.3.118"),sQuery(id+"F0.wireOp",EDGE,"E6.0.3.120"),sQuery(id+"F0.wireOp",EDGE,"E6.0.3.121"),sQuery(id+"F0.wireOp",EDGE,"E6.0.3.122"),sQuery(id+"F0.wireOp",EDGE,"E6.0.3.123"),sQuery(id+"F0.wireOp",EDGE,"E6.0.3.124"),sQuery(id+"F0.wireOp",EDGE,"E6.0.3.125"),sQuery(id+"F0.wireOp",EDGE,"E6.0.3.126"),sQuery(id+"F0.wireOp",EDGE,"E6.0.3.127"),sQuery(id+"F0.wireOp",EDGE,"E6.0.3.128"),sQuery(id+"F0.wireOp",EDGE,"E6.0.3.129"),sQuery(id+"F0.wireOp",EDGE,"E6.0.3.130"),sQuery(id+"F0.wireOp",EDGE,"E6.0.3.131"),sQuery(id+"F0.wireOp",EDGE,"E6.0.3.132"),sQuery(id+"F0.wireOp",EDGE,"E6.0.3.133"),sQuery(id+"F0.wireOp",EDGE,"E6.0.3.134"),sQuery(id+"F0.wireOp",EDGE,"E6.0.3.135"),sQuery(id+"F0.wireOp",EDGE,"E6.0.3.136"),sQuery(id+"F0.wireOp",EDGE,"E6.0.3.137"),sQuery(id+"F0.wireOp",EDGE,"E6.0.3.138"),sQuery(id+"F0.wireOp",EDGE,"E6.0.3.139"),sQuery(id+"F0.wireOp",EDGE,"E6.0.3.140"),sQuery(id+"F0.wireOp",EDGE,"E6.0.3.141"),sQuery(id+"F0.wireOp",EDGE,"E6.0.3.143"),sQuery(id+"F0.wireOp",EDGE,"E6.0.3.144"),sQuery(id+"F0.wireOp",EDGE,"E6.0.4.2"),sQuery(id+"F0.wireOp",EDGE,"E6.0.4.4"),sQuery(id+"F0.wireOp",EDGE,"E6.0.4.8"),sQuery(id+"F0.wireOp",EDGE,"E6.0.4.10"),sQuery(id+"F0.wireOp",EDGE,"E6.0.4.11"),sQuery(id+"F0.wireOp",EDGE,"E6.0.4.12"),sQuery(id+"F0.wireOp",EDGE,"E6.0.4.13"),sQuery(id+"F0.wireOp",EDGE,"E6.0.4.14"),sQuery(id+"F0.wireOp",EDGE,"E6.0.4.15"),sQuery(id+"F0.wireOp",EDGE,"E6.0.4.16"),sQuery(id+"F0.wireOp",EDGE,"E6.0.4.17"),sQuery(id+"F0.wireOp",EDGE,"E6.0.4.18"),sQuery(id+"F0.wireOp",EDGE,"E6.0.4.20"),sQuery(id+"F0.wireOp",EDGE,"E6.0.4.21"),sQuery(id+"F0.wireOp",EDGE,"E6.0.4.22"),sQuery(id+"F0.wireOp",EDGE,"E6.0.4.23"),sQuery(id+"F0.wireOp",EDGE,"E6.0.4.24"),sQuery(id+"F0.wireOp",EDGE,"E6.0.4.25"),sQuery(id+"F0.wireOp",EDGE,"E6.0.4.26"),sQuery(id+"F0.wireOp",EDGE,"E6.0.4.27"),sQuery(id+"F0.wireOp",EDGE,"E6.0.4.28"),sQuery(id+"F0.wireOp",EDGE,"E6.0.4.29"),sQuery(id+"F0.wireOp",EDGE,"E6.0.4.30"),sQuery(id+"F0.wireOp",EDGE,"E6.0.4.31"),sQuery(id+"F0.wireOp",EDGE,"E6.0.4.33"),sQuery(id+"F0.wireOp",EDGE,"E6.0.4.34"),sQuery(id+"F0.wireOp",EDGE,"E6.0.4.36"),sQuery(id+"F0.wireOp",EDGE,"E6.0.4.37"),sQuery(id+"F0.wireOp",EDGE,"E6.0.4.38"),sQuery(id+"F0.wireOp",EDGE,"E6.0.4.39"),sQuery(id+"F0.wireOp",EDGE,"E6.0.4.41"),sQuery(id+"F0.wireOp",EDGE,"E6.0.4.42"),sQuery(id+"F0.wireOp",EDGE,"E6.0.4.43"),sQuery(id+"F0.wireOp",EDGE,"E6.0.4.44"),sQuery(id+"F0.wireOp",EDGE,"E6.0.4.46"),sQuery(id+"F0.wireOp",EDGE,"E6.0.4.48"),sQuery(id+"F0.wireOp",EDGE,"E6.0.4.49"),sQuery(id+"F0.wireOp",EDGE,"E6.0.4.51"),sQuery(id+"F0.wireOp",EDGE,"E6.0.4.52"),sQuery(id+"F0.wireOp",EDGE,"E6.0.4.53"),sQuery(id+"F0.wireOp",EDGE,"E6.0.4.54"),sQuery(id+"F0.wireOp",EDGE,"E6.0.4.55"),sQuery(id+"F0.wireOp",EDGE,"E6.0.4.57"),sQuery(id+"F0.wireOp",EDGE,"E6.0.4.59"),sQuery(id+"F0.wireOp",EDGE,"E6.0.4.60"),sQuery(id+"F0.wireOp",EDGE,"E6.0.4.62"),sQuery(id+"F0.wireOp",EDGE,"E6.0.4.63"),sQuery(id+"F0.wireOp",EDGE,"E6.0.4.64"),sQuery(id+"F0.wireOp",EDGE,"E6.0.4.65"),sQuery(id+"F0.wireOp",EDGE,"E6.0.4.66"),sQuery(id+"F0.wireOp",EDGE,"E6.0.4.67"),sQuery(id+"F0.wireOp",EDGE,"E6.0.4.68"),sQuery(id+"F0.wireOp",EDGE,"E6.0.4.70"),sQuery(id+"F0.wireOp",EDGE,"E6.0.4.71"),sQuery(id+"F0.wireOp",EDGE,"E6.0.4.72"),sQuery(id+"F0.wireOp",EDGE,"E6.0.4.73"),sQuery(id+"F0.wireOp",EDGE,"E6.0.4.75"),sQuery(id+"F0.wireOp",EDGE,"E6.0.4.76"),sQuery(id+"F0.wireOp",EDGE,"E6.0.4.77"),sQuery(id+"F0.wireOp",EDGE,"E6.0.4.78"),sQuery(id+"F0.wireOp",EDGE,"E6.0.4.80"),sQuery(id+"F0.wireOp",EDGE,"E6.0.4.81"),sQuery(id+"F0.wireOp",EDGE,"E6.0.4.82"),sQuery(id+"F0.wireOp",EDGE,"E6.0.4.83"),sQuery(id+"F0.wireOp",EDGE,"E6.0.4.85"),sQuery(id+"F0.wireOp",EDGE,"E6.0.4.86"),sQuery(id+"F0.wireOp",EDGE,"E6.0.4.87"),sQuery(id+"F0.wireOp",EDGE,"E6.0.4.88"),sQuery(id+"F0.wireOp",EDGE,"E6.0.4.89"),sQuery(id+"F0.wireOp",EDGE,"E6.0.4.90"),sQuery(id+"F0.wireOp",EDGE,"E6.0.4.91"),sQuery(id+"F0.wireOp",EDGE,"E6.0.4.92"),sQuery(id+"F0.wireOp",EDGE,"E6.0.4.94"),sQuery(id+"F0.wireOp",EDGE,"E6.0.4.95"),sQuery(id+"F0.wireOp",EDGE,"E6.0.4.96"),sQuery(id+"F0.wireOp",EDGE,"E6.0.4.97"),sQuery(id+"F0.wireOp",EDGE,"E6.0.4.98"),sQuery(id+"F0.wireOp",EDGE,"E6.0.4.99"),sQuery(id+"F0.wireOp",EDGE,"E6.0.4.100"),sQuery(id+"F0.wireOp",EDGE,"E6.0.4.101"),sQuery(id+"F0.wireOp",EDGE,"E6.0.4.102"),sQuery(id+"F0.wireOp",EDGE,"E6.0.4.103"),sQuery(id+"F0.wireOp",EDGE,"E6.0.4.104"),sQuery(id+"F0.wireOp",EDGE,"E6.0.4.105"),sQuery(id+"F0.wireOp",EDGE,"E6.0.4.106"),sQuery(id+"F0.wireOp",EDGE,"E6.0.4.107"),sQuery(id+"F0.wireOp",EDGE,"E6.0.4.108"),sQuery(id+"F0.wireOp",EDGE,"E6.0.4.109"),sQuery(id+"F0.wireOp",EDGE,"E6.0.4.110"),sQuery(id+"F0.wireOp",EDGE,"E6.0.4.111"),sQuery(id+"F0.wireOp",EDGE,"E6.0.4.112"),sQuery(id+"F0.wireOp",EDGE,"E6.0.4.113"),sQuery(id+"F0.wireOp",EDGE,"E6.0.4.114"),sQuery(id+"F0.wireOp",EDGE,"E6.0.4.115"),sQuery(id+"F0.wireOp",EDGE,"E6.0.4.117"),sQuery(id+"F0.wireOp",EDGE,"E6.0.4.118"),sQuery(id+"F0.wireOp",EDGE,"E6.0.4.120"),sQuery(id+"F0.wireOp",EDGE,"E6.0.4.121"),sQuery(id+"F0.wireOp",EDGE,"E6.0.4.122"),sQuery(id+"F0.wireOp",EDGE,"E6.0.4.123"),sQuery(id+"F0.wireOp",EDGE,"E6.0.4.124"),sQuery(id+"F0.wireOp",EDGE,"E6.0.4.125"),sQuery(id+"F0.wireOp",EDGE,"E6.0.4.126"),sQuery(id+"F0.wireOp",EDGE,"E6.0.4.127"),sQuery(id+"F0.wireOp",EDGE,"E6.0.4.128"),sQuery(id+"F0.wireOp",EDGE,"E6.0.4.129"),sQuery(id+"F0.wireOp",EDGE,"E6.0.4.130"),sQuery(id+"F0.wireOp",EDGE,"E6.0.4.131"),sQuery(id+"F0.wireOp",EDGE,"E6.0.4.132"),sQuery(id+"F0.wireOp",EDGE,"E6.0.4.133"),sQuery(id+"F0.wireOp",EDGE,"E6.0.4.134"),sQuery(id+"F0.wireOp",EDGE,"E6.0.4.135"),sQuery(id+"F0.wireOp",EDGE,"E6.0.4.136"),sQuery(id+"F0.wireOp",EDGE,"E6.0.4.137"),sQuery(id+"F0.wireOp",EDGE,"E6.0.4.138"),sQuery(id+"F0.wireOp",EDGE,"E6.0.4.139"),sQuery(id+"F0.wireOp",EDGE,"E6.0.4.140"),sQuery(id+"F0.wireOp",EDGE,"E6.0.4.141"),sQuery(id+"F0.wireOp",EDGE,"E6.0.4.143"),sQuery(id+"F0.wireOp",EDGE,"E6.0.4.144"),sQuery(id+"F0.wireOp",EDGE,"E10.bottom"),sQuery(id+"F0.wireOp",EDGE,"E10.top"),sQuery(id+"F0.wireOp",EDGE,"E10.left"),sQuery(id+"F0.wireOp",EDGE,"E10.right")])],"isStart":false});
            fillet(context, id + "F2", {"entities" : qUnion([Q0]), "radius" : 0.3 * mm, "tangentPropagation" : true, "allowEdgeOverflow" : false});
        }
        {
            var Q0;
            Q0=makeQuery(id+"F1.opExtrude","SWEPT_BODY",BODY,{"disambiguationData":[OSD([sQuery(id+"F0.wireOp",EDGE,"E0.0"),sQuery(id+"F0.wireOp",EDGE,"E0.1"),sQuery(id+"F0.wireOp",EDGE,"E0.2"),sQuery(id+"F0.wireOp",EDGE,"E0.3"),sQuery(id+"F0.wireOp",EDGE,"E0.4"),sQuery(id+"F0.wireOp",EDGE,"E0.5"),sQuery(id+"F0.wireOp",EDGE,"E1.1.0.0"),sQuery(id+"F0.wireOp",EDGE,"E1.1.0.1"),sQuery(id+"F0.wireOp",EDGE,"E1.1.0.2"),sQuery(id+"F0.wireOp",EDGE,"E1.1.0.3"),sQuery(id+"F0.wireOp",EDGE,"E1.1.0.4"),sQuery(id+"F0.wireOp",EDGE,"E1.1.0.5"),sQuery(id+"F0.wireOp",EDGE,"E1.2.0.0"),sQuery(id+"F0.wireOp",EDGE,"E1.2.0.1"),sQuery(id+"F0.wireOp",EDGE,"E1.2.0.2"),sQuery(id+"F0.wireOp",EDGE,"E1.2.0.3"),sQuery(id+"F0.wireOp",EDGE,"E1.2.0.4"),sQuery(id+"F0.wireOp",EDGE,"E1.2.0.5"),sQuery(id+"F0.wireOp",EDGE,"0f33f7c7-d985-4434-8b08-4c21ebd6a896.0.3.0"),sQuery(id+"F0.wireOp",EDGE,"0f33f7c7-d985-4434-8b08-4c21ebd6a896.3.3.0"),sQuery(id+"F0.wireOp",EDGE,"0f33f7c7-d985-4434-8b08-4c21ebd6a896.6.3.0"),sQuery(id+"F0.wireOp",EDGE,"0f33f7c7-d985-4434-8b08-4c21ebd6a896.9.3.0"),sQuery(id+"F0.wireOp",EDGE,"0f33f7c7-d985-4434-8b08-4c21ebd6a896.12.3.0"),sQuery(id+"F0.wireOp",EDGE,"0f33f7c7-d985-4434-8b08-4c21ebd6a896.15.3.0"),sQuery(id+"F0.wireOp",EDGE,"0f33f7c7-d985-4434-8b08-4c21ebd6a896.0.4.0"),sQuery(id+"F0.wireOp",EDGE,"0f33f7c7-d985-4434-8b08-4c21ebd6a896.3.4.0"),sQuery(id+"F0.wireOp",EDGE,"0f33f7c7-d985-4434-8b08-4c21ebd6a896.6.4.0"),sQuery(id+"F0.wireOp",EDGE,"0f33f7c7-d985-4434-8b08-4c21ebd6a896.9.4.0"),sQuery(id+"F0.wireOp",EDGE,"0f33f7c7-d985-4434-8b08-4c21ebd6a896.12.4.0"),sQuery(id+"F0.wireOp",EDGE,"0f33f7c7-d985-4434-8b08-4c21ebd6a896.15.4.0"),sQuery(id+"F0.wireOp",EDGE,"0f33f7c7-d985-4434-8b08-4c21ebd6a896.0.5.0"),sQuery(id+"F0.wireOp",EDGE,"0f33f7c7-d985-4434-8b08-4c21ebd6a896.3.5.0"),sQuery(id+"F0.wireOp",EDGE,"0f33f7c7-d985-4434-8b08-4c21ebd6a896.6.5.0"),sQuery(id+"F0.wireOp",EDGE,"0f33f7c7-d985-4434-8b08-4c21ebd6a896.9.5.0"),sQuery(id+"F0.wireOp",EDGE,"0f33f7c7-d985-4434-8b08-4c21ebd6a896.12.5.0"),sQuery(id+"F0.wireOp",EDGE,"0f33f7c7-d985-4434-8b08-4c21ebd6a896.15.5.0"),sQuery(id+"F0.wireOp",EDGE,"0f33f7c7-d985-4434-8b08-4c21ebd6a896.0.6.0"),sQuery(id+"F0.wireOp",EDGE,"0f33f7c7-d985-4434-8b08-4c21ebd6a896.3.6.0"),sQuery(id+"F0.wireOp",EDGE,"0f33f7c7-d985-4434-8b08-4c21ebd6a896.6.6.0"),sQuery(id+"F0.wireOp",EDGE,"0f33f7c7-d985-4434-8b08-4c21ebd6a896.9.6.0"),sQuery(id+"F0.wireOp",EDGE,"0f33f7c7-d985-4434-8b08-4c21ebd6a896.12.6.0"),sQuery(id+"F0.wireOp",EDGE,"0f33f7c7-d985-4434-8b08-4c21ebd6a896.15.6.0"),sQuery(id+"F0.wireOp",EDGE,"0f33f7c7-d985-4434-8b08-4c21ebd6a896.0.7.0"),sQuery(id+"F0.wireOp",EDGE,"0f33f7c7-d985-4434-8b08-4c21ebd6a896.3.7.0"),sQuery(id+"F0.wireOp",EDGE,"0f33f7c7-d985-4434-8b08-4c21ebd6a896.6.7.0"),sQuery(id+"F0.wireOp",EDGE,"0f33f7c7-d985-4434-8b08-4c21ebd6a896.9.7.0"),sQuery(id+"F0.wireOp",EDGE,"0f33f7c7-d985-4434-8b08-4c21ebd6a896.12.7.0"),sQuery(id+"F0.wireOp",EDGE,"0f33f7c7-d985-4434-8b08-4c21ebd6a896.15.7.0"),sQuery(id+"F0.wireOp",EDGE,"0f33f7c7-d985-4434-8b08-4c21ebd6a896.0.8.0"),sQuery(id+"F0.wireOp",EDGE,"0f33f7c7-d985-4434-8b08-4c21ebd6a896.3.8.0"),sQuery(id+"F0.wireOp",EDGE,"0f33f7c7-d985-4434-8b08-4c21ebd6a896.6.8.0"),sQuery(id+"F0.wireOp",EDGE,"0f33f7c7-d985-4434-8b08-4c21ebd6a896.9.8.0"),sQuery(id+"F0.wireOp",EDGE,"0f33f7c7-d985-4434-8b08-4c21ebd6a896.12.8.0"),sQuery(id+"F0.wireOp",EDGE,"0f33f7c7-d985-4434-8b08-4c21ebd6a896.15.8.0"),sQuery(id+"F0.wireOp",EDGE,"0f33f7c7-d985-4434-8b08-4c21ebd6a896.0.9.0"),sQuery(id+"F0.wireOp",EDGE,"0f33f7c7-d985-4434-8b08-4c21ebd6a896.3.9.0"),sQuery(id+"F0.wireOp",EDGE,"0f33f7c7-d985-4434-8b08-4c21ebd6a896.6.9.0"),sQuery(id+"F0.wireOp",EDGE,"0f33f7c7-d985-4434-8b08-4c21ebd6a896.9.9.0"),sQuery(id+"F0.wireOp",EDGE,"0f33f7c7-d985-4434-8b08-4c21ebd6a896.12.9.0"),sQuery(id+"F0.wireOp",EDGE,"0f33f7c7-d985-4434-8b08-4c21ebd6a896.15.9.0"),sQuery(id+"F0.wireOp",EDGE,"E2.0.1.1"),sQuery(id+"F0.wireOp",EDGE,"E2.0.1.2"),sQuery(id+"F0.wireOp",EDGE,"E2.0.1.3"),sQuery(id+"F0.wireOp",EDGE,"E2.0.1.5"),sQuery(id+"F0.wireOp",EDGE,"E2.0.1.7"),sQuery(id+"F0.wireOp",EDGE,"E2.0.1.8"),sQuery(id+"F0.wireOp",EDGE,"E2.0.1.9"),sQuery(id+"F0.wireOp",EDGE,"E2.0.1.10"),sQuery(id+"F0.wireOp",EDGE,"E2.0.1.11"),sQuery(id+"F0.wireOp",EDGE,"E2.0.1.12"),sQuery(id+"F0.wireOp",EDGE,"E2.0.1.14"),sQuery(id+"F0.wireOp",EDGE,"E2.0.1.15"),sQuery(id+"F0.wireOp",EDGE,"E2.0.1.16"),sQuery(id+"F0.wireOp",EDGE,"E2.0.1.17"),sQuery(id+"F0.wireOp",EDGE,"E2.0.1.18"),sQuery(id+"F0.wireOp",EDGE,"E2.0.1.19"),sQuery(id+"F0.wireOp",EDGE,"E2.0.1.21"),sQuery(id+"F0.wireOp",EDGE,"E2.0.1.22"),sQuery(id+"F0.wireOp",EDGE,"E2.0.1.23"),sQuery(id+"F0.wireOp",EDGE,"E2.0.1.24"),sQuery(id+"F0.wireOp",EDGE,"E2.0.1.25"),sQuery(id+"F0.wireOp",EDGE,"E2.0.1.26"),sQuery(id+"F0.wireOp",EDGE,"E2.0.1.28"),sQuery(id+"F0.wireOp",EDGE,"E2.0.1.29"),sQuery(id+"F0.wireOp",EDGE,"E2.0.1.30"),sQuery(id+"F0.wireOp",EDGE,"E2.0.1.31"),sQuery(id+"F0.wireOp",EDGE,"E2.0.1.32"),sQuery(id+"F0.wireOp",EDGE,"E2.0.1.33"),sQuery(id+"F0.wireOp",EDGE,"E2.0.1.35"),sQuery(id+"F0.wireOp",EDGE,"E2.0.1.36"),sQuery(id+"F0.wireOp",EDGE,"E2.0.1.37"),sQuery(id+"F0.wireOp",EDGE,"E2.0.1.38"),sQuery(id+"F0.wireOp",EDGE,"E2.0.1.39"),sQuery(id+"F0.wireOp",EDGE,"E2.0.1.40"),sQuery(id+"F0.wireOp",EDGE,"E2.0.1.41"),sQuery(id+"F0.wireOp",EDGE,"E2.0.1.42"),sQuery(id+"F0.wireOp",EDGE,"E2.0.1.44"),sQuery(id+"F0.wireOp",EDGE,"E2.0.1.46"),sQuery(id+"F0.wireOp",EDGE,"E2.0.1.47"),sQuery(id+"F0.wireOp",EDGE,"E2.0.1.48"),sQuery(id+"F0.wireOp",EDGE,"E2.0.1.49"),sQuery(id+"F0.wireOp",EDGE,"E2.0.1.51"),sQuery(id+"F0.wireOp",EDGE,"E2.0.1.52"),sQuery(id+"F0.wireOp",EDGE,"E2.0.1.53"),sQuery(id+"F0.wireOp",EDGE,"E2.0.1.54"),sQuery(id+"F0.wireOp",EDGE,"E2.0.1.55"),sQuery(id+"F0.wireOp",EDGE,"E2.0.1.56"),sQuery(id+"F0.wireOp",EDGE,"E2.0.1.57"),sQuery(id+"F0.wireOp",EDGE,"E2.0.1.58"),sQuery(id+"F0.wireOp",EDGE,"E2.0.1.60"),sQuery(id+"F0.wireOp",EDGE,"E2.0.1.61"),sQuery(id+"F0.wireOp",EDGE,"E2.0.1.62"),sQuery(id+"F0.wireOp",EDGE,"E2.0.1.63"),sQuery(id+"F0.wireOp",EDGE,"E2.0.1.64"),sQuery(id+"F0.wireOp",EDGE,"E2.0.1.65"),sQuery(id+"F0.wireOp",EDGE,"E2.0.1.66"),sQuery(id+"F0.wireOp",EDGE,"E2.0.1.67"),sQuery(id+"F0.wireOp",EDGE,"E2.0.1.68"),sQuery(id+"F0.wireOp",EDGE,"E2.0.1.69"),sQuery(id+"F0.wireOp",EDGE,"E2.0.1.70"),sQuery(id+"F0.wireOp",EDGE,"E6.0.1.2"),sQuery(id+"F0.wireOp",EDGE,"E6.0.1.4"),sQuery(id+"F0.wireOp",EDGE,"E6.0.1.8"),sQuery(id+"F0.wireOp",EDGE,"E6.0.1.10"),sQuery(id+"F0.wireOp",EDGE,"E6.0.1.11"),sQuery(id+"F0.wireOp",EDGE,"E6.0.1.12"),sQuery(id+"F0.wireOp",EDGE,"E6.0.1.13"),sQuery(id+"F0.wireOp",EDGE,"E6.0.1.14"),sQuery(id+"F0.wireOp",EDGE,"E6.0.1.15"),sQuery(id+"F0.wireOp",EDGE,"E6.0.1.16"),sQuery(id+"F0.wireOp",EDGE,"E6.0.1.17"),sQuery(id+"F0.wireOp",EDGE,"E6.0.1.18"),sQuery(id+"F0.wireOp",EDGE,"E6.0.1.20"),sQuery(id+"F0.wireOp",EDGE,"E6.0.1.21"),sQuery(id+"F0.wireOp",EDGE,"E6.0.1.22"),sQuery(id+"F0.wireOp",EDGE,"E6.0.1.23"),sQuery(id+"F0.wireOp",EDGE,"E6.0.1.24"),sQuery(id+"F0.wireOp",EDGE,"E6.0.1.25"),sQuery(id+"F0.wireOp",EDGE,"E6.0.1.26"),sQuery(id+"F0.wireOp",EDGE,"E6.0.1.27"),sQuery(id+"F0.wireOp",EDGE,"E6.0.1.28"),sQuery(id+"F0.wireOp",EDGE,"E6.0.1.29"),sQuery(id+"F0.wireOp",EDGE,"E6.0.1.30"),sQuery(id+"F0.wireOp",EDGE,"E6.0.1.31"),sQuery(id+"F0.wireOp",EDGE,"E6.0.1.33"),sQuery(id+"F0.wireOp",EDGE,"E6.0.1.34"),sQuery(id+"F0.wireOp",EDGE,"E6.0.1.36"),sQuery(id+"F0.wireOp",EDGE,"E6.0.1.37"),sQuery(id+"F0.wireOp",EDGE,"E6.0.1.38"),sQuery(id+"F0.wireOp",EDGE,"E6.0.1.39"),sQuery(id+"F0.wireOp",EDGE,"E6.0.1.41"),sQuery(id+"F0.wireOp",EDGE,"E6.0.1.42"),sQuery(id+"F0.wireOp",EDGE,"E6.0.1.43"),sQuery(id+"F0.wireOp",EDGE,"E6.0.1.44"),sQuery(id+"F0.wireOp",EDGE,"E6.0.1.46"),sQuery(id+"F0.wireOp",EDGE,"E6.0.1.48"),sQuery(id+"F0.wireOp",EDGE,"E6.0.1.49"),sQuery(id+"F0.wireOp",EDGE,"E6.0.1.51"),sQuery(id+"F0.wireOp",EDGE,"E6.0.1.52"),sQuery(id+"F0.wireOp",EDGE,"E6.0.1.53"),sQuery(id+"F0.wireOp",EDGE,"E6.0.1.54"),sQuery(id+"F0.wireOp",EDGE,"E6.0.1.55"),sQuery(id+"F0.wireOp",EDGE,"E6.0.1.57"),sQuery(id+"F0.wireOp",EDGE,"E6.0.1.59"),sQuery(id+"F0.wireOp",EDGE,"E6.0.1.60"),sQuery(id+"F0.wireOp",EDGE,"E6.0.1.62"),sQuery(id+"F0.wireOp",EDGE,"E6.0.1.63"),sQuery(id+"F0.wireOp",EDGE,"E6.0.1.64"),sQuery(id+"F0.wireOp",EDGE,"E6.0.1.65"),sQuery(id+"F0.wireOp",EDGE,"E6.0.1.66"),sQuery(id+"F0.wireOp",EDGE,"E6.0.1.67"),sQuery(id+"F0.wireOp",EDGE,"E6.0.1.68"),sQuery(id+"F0.wireOp",EDGE,"E6.0.1.70"),sQuery(id+"F0.wireOp",EDGE,"E6.0.1.71"),sQuery(id+"F0.wireOp",EDGE,"E6.0.1.72"),sQuery(id+"F0.wireOp",EDGE,"E6.0.1.73"),sQuery(id+"F0.wireOp",EDGE,"E6.0.1.75"),sQuery(id+"F0.wireOp",EDGE,"E6.0.1.76"),sQuery(id+"F0.wireOp",EDGE,"E6.0.1.77"),sQuery(id+"F0.wireOp",EDGE,"E6.0.1.78"),sQuery(id+"F0.wireOp",EDGE,"E6.0.1.80"),sQuery(id+"F0.wireOp",EDGE,"E6.0.1.81"),sQuery(id+"F0.wireOp",EDGE,"E6.0.1.82"),sQuery(id+"F0.wireOp",EDGE,"E6.0.1.83"),sQuery(id+"F0.wireOp",EDGE,"E6.0.1.85"),sQuery(id+"F0.wireOp",EDGE,"E6.0.1.86"),sQuery(id+"F0.wireOp",EDGE,"E6.0.1.87"),sQuery(id+"F0.wireOp",EDGE,"E6.0.1.88"),sQuery(id+"F0.wireOp",EDGE,"E6.0.1.89"),sQuery(id+"F0.wireOp",EDGE,"E6.0.1.90"),sQuery(id+"F0.wireOp",EDGE,"E6.0.1.91"),sQuery(id+"F0.wireOp",EDGE,"E6.0.1.92"),sQuery(id+"F0.wireOp",EDGE,"E6.0.1.94"),sQuery(id+"F0.wireOp",EDGE,"E6.0.1.95"),sQuery(id+"F0.wireOp",EDGE,"E6.0.1.96"),sQuery(id+"F0.wireOp",EDGE,"E6.0.1.97"),sQuery(id+"F0.wireOp",EDGE,"E6.0.1.98"),sQuery(id+"F0.wireOp",EDGE,"E6.0.1.99"),sQuery(id+"F0.wireOp",EDGE,"E6.0.1.100"),sQuery(id+"F0.wireOp",EDGE,"E6.0.1.101"),sQuery(id+"F0.wireOp",EDGE,"E6.0.1.102"),sQuery(id+"F0.wireOp",EDGE,"E6.0.1.103"),sQuery(id+"F0.wireOp",EDGE,"E6.0.1.104"),sQuery(id+"F0.wireOp",EDGE,"E6.0.1.105"),sQuery(id+"F0.wireOp",EDGE,"E6.0.1.106"),sQuery(id+"F0.wireOp",EDGE,"E6.0.1.107"),sQuery(id+"F0.wireOp",EDGE,"E6.0.1.108"),sQuery(id+"F0.wireOp",EDGE,"E6.0.1.109"),sQuery(id+"F0.wireOp",EDGE,"E6.0.1.110"),sQuery(id+"F0.wireOp",EDGE,"E6.0.1.111"),sQuery(id+"F0.wireOp",EDGE,"E6.0.1.112"),sQuery(id+"F0.wireOp",EDGE,"E6.0.1.113"),sQuery(id+"F0.wireOp",EDGE,"E6.0.1.114"),sQuery(id+"F0.wireOp",EDGE,"E6.0.1.115"),sQuery(id+"F0.wireOp",EDGE,"E6.0.1.117"),sQuery(id+"F0.wireOp",EDGE,"E6.0.1.118"),sQuery(id+"F0.wireOp",EDGE,"E6.0.1.120"),sQuery(id+"F0.wireOp",EDGE,"E6.0.1.121"),sQuery(id+"F0.wireOp",EDGE,"E6.0.1.122"),sQuery(id+"F0.wireOp",EDGE,"E6.0.1.123"),sQuery(id+"F0.wireOp",EDGE,"E6.0.1.124"),sQuery(id+"F0.wireOp",EDGE,"E6.0.1.125"),sQuery(id+"F0.wireOp",EDGE,"E6.0.1.126"),sQuery(id+"F0.wireOp",EDGE,"E6.0.1.127"),sQuery(id+"F0.wireOp",EDGE,"E6.0.1.128"),sQuery(id+"F0.wireOp",EDGE,"E6.0.1.129"),sQuery(id+"F0.wireOp",EDGE,"E6.0.1.130"),sQuery(id+"F0.wireOp",EDGE,"E6.0.1.131"),sQuery(id+"F0.wireOp",EDGE,"E6.0.1.132"),sQuery(id+"F0.wireOp",EDGE,"E6.0.1.133"),sQuery(id+"F0.wireOp",EDGE,"E6.0.1.134"),sQuery(id+"F0.wireOp",EDGE,"E6.0.1.135"),sQuery(id+"F0.wireOp",EDGE,"E6.0.1.136"),sQuery(id+"F0.wireOp",EDGE,"E6.0.1.137"),sQuery(id+"F0.wireOp",EDGE,"E6.0.1.138"),sQuery(id+"F0.wireOp",EDGE,"E6.0.1.139"),sQuery(id+"F0.wireOp",EDGE,"E6.0.1.140"),sQuery(id+"F0.wireOp",EDGE,"E6.0.1.141"),sQuery(id+"F0.wireOp",EDGE,"E6.0.1.143"),sQuery(id+"F0.wireOp",EDGE,"E6.0.1.144"),sQuery(id+"F0.wireOp",EDGE,"E6.0.2.2"),sQuery(id+"F0.wireOp",EDGE,"E6.0.2.4"),sQuery(id+"F0.wireOp",EDGE,"E6.0.2.8"),sQuery(id+"F0.wireOp",EDGE,"E6.0.2.10"),sQuery(id+"F0.wireOp",EDGE,"E6.0.2.11"),sQuery(id+"F0.wireOp",EDGE,"E6.0.2.12"),sQuery(id+"F0.wireOp",EDGE,"E6.0.2.13"),sQuery(id+"F0.wireOp",EDGE,"E6.0.2.14"),sQuery(id+"F0.wireOp",EDGE,"E6.0.2.15"),sQuery(id+"F0.wireOp",EDGE,"E6.0.2.16"),sQuery(id+"F0.wireOp",EDGE,"E6.0.2.17"),sQuery(id+"F0.wireOp",EDGE,"E6.0.2.18"),sQuery(id+"F0.wireOp",EDGE,"E6.0.2.20"),sQuery(id+"F0.wireOp",EDGE,"E6.0.2.21"),sQuery(id+"F0.wireOp",EDGE,"E6.0.2.22"),sQuery(id+"F0.wireOp",EDGE,"E6.0.2.23"),sQuery(id+"F0.wireOp",EDGE,"E6.0.2.24"),sQuery(id+"F0.wireOp",EDGE,"E6.0.2.25"),sQuery(id+"F0.wireOp",EDGE,"E6.0.2.26"),sQuery(id+"F0.wireOp",EDGE,"E6.0.2.27"),sQuery(id+"F0.wireOp",EDGE,"E6.0.2.28"),sQuery(id+"F0.wireOp",EDGE,"E6.0.2.29"),sQuery(id+"F0.wireOp",EDGE,"E6.0.2.30"),sQuery(id+"F0.wireOp",EDGE,"E6.0.2.31"),sQuery(id+"F0.wireOp",EDGE,"E6.0.2.33"),sQuery(id+"F0.wireOp",EDGE,"E6.0.2.34"),sQuery(id+"F0.wireOp",EDGE,"E6.0.2.36"),sQuery(id+"F0.wireOp",EDGE,"E6.0.2.37"),sQuery(id+"F0.wireOp",EDGE,"E6.0.2.38"),sQuery(id+"F0.wireOp",EDGE,"E6.0.2.39"),sQuery(id+"F0.wireOp",EDGE,"E6.0.2.41"),sQuery(id+"F0.wireOp",EDGE,"E6.0.2.42"),sQuery(id+"F0.wireOp",EDGE,"E6.0.2.43"),sQuery(id+"F0.wireOp",EDGE,"E6.0.2.44"),sQuery(id+"F0.wireOp",EDGE,"E6.0.2.46"),sQuery(id+"F0.wireOp",EDGE,"E6.0.2.48"),sQuery(id+"F0.wireOp",EDGE,"E6.0.2.49"),sQuery(id+"F0.wireOp",EDGE,"E6.0.2.51"),sQuery(id+"F0.wireOp",EDGE,"E6.0.2.52"),sQuery(id+"F0.wireOp",EDGE,"E6.0.2.53"),sQuery(id+"F0.wireOp",EDGE,"E6.0.2.54"),sQuery(id+"F0.wireOp",EDGE,"E6.0.2.55"),sQuery(id+"F0.wireOp",EDGE,"E6.0.2.57"),sQuery(id+"F0.wireOp",EDGE,"E6.0.2.59"),sQuery(id+"F0.wireOp",EDGE,"E6.0.2.60"),sQuery(id+"F0.wireOp",EDGE,"E6.0.2.62"),sQuery(id+"F0.wireOp",EDGE,"E6.0.2.63"),sQuery(id+"F0.wireOp",EDGE,"E6.0.2.64"),sQuery(id+"F0.wireOp",EDGE,"E6.0.2.65"),sQuery(id+"F0.wireOp",EDGE,"E6.0.2.66"),sQuery(id+"F0.wireOp",EDGE,"E6.0.2.67"),sQuery(id+"F0.wireOp",EDGE,"E6.0.2.68"),sQuery(id+"F0.wireOp",EDGE,"E6.0.2.70"),sQuery(id+"F0.wireOp",EDGE,"E6.0.2.71"),sQuery(id+"F0.wireOp",EDGE,"E6.0.2.72"),sQuery(id+"F0.wireOp",EDGE,"E6.0.2.73"),sQuery(id+"F0.wireOp",EDGE,"E6.0.2.75"),sQuery(id+"F0.wireOp",EDGE,"E6.0.2.76"),sQuery(id+"F0.wireOp",EDGE,"E6.0.2.77"),sQuery(id+"F0.wireOp",EDGE,"E6.0.2.78"),sQuery(id+"F0.wireOp",EDGE,"E6.0.2.80"),sQuery(id+"F0.wireOp",EDGE,"E6.0.2.81"),sQuery(id+"F0.wireOp",EDGE,"E6.0.2.82"),sQuery(id+"F0.wireOp",EDGE,"E6.0.2.83"),sQuery(id+"F0.wireOp",EDGE,"E6.0.2.85"),sQuery(id+"F0.wireOp",EDGE,"E6.0.2.86"),sQuery(id+"F0.wireOp",EDGE,"E6.0.2.87"),sQuery(id+"F0.wireOp",EDGE,"E6.0.2.88"),sQuery(id+"F0.wireOp",EDGE,"E6.0.2.89"),sQuery(id+"F0.wireOp",EDGE,"E6.0.2.90"),sQuery(id+"F0.wireOp",EDGE,"E6.0.2.91"),sQuery(id+"F0.wireOp",EDGE,"E6.0.2.92"),sQuery(id+"F0.wireOp",EDGE,"E6.0.2.94"),sQuery(id+"F0.wireOp",EDGE,"E6.0.2.95"),sQuery(id+"F0.wireOp",EDGE,"E6.0.2.96"),sQuery(id+"F0.wireOp",EDGE,"E6.0.2.97"),sQuery(id+"F0.wireOp",EDGE,"E6.0.2.98"),sQuery(id+"F0.wireOp",EDGE,"E6.0.2.99"),sQuery(id+"F0.wireOp",EDGE,"E6.0.2.100"),sQuery(id+"F0.wireOp",EDGE,"E6.0.2.101"),sQuery(id+"F0.wireOp",EDGE,"E6.0.2.102"),sQuery(id+"F0.wireOp",EDGE,"E6.0.2.103"),sQuery(id+"F0.wireOp",EDGE,"E6.0.2.104"),sQuery(id+"F0.wireOp",EDGE,"E6.0.2.105"),sQuery(id+"F0.wireOp",EDGE,"E6.0.2.106"),sQuery(id+"F0.wireOp",EDGE,"E6.0.2.107"),sQuery(id+"F0.wireOp",EDGE,"E6.0.2.108"),sQuery(id+"F0.wireOp",EDGE,"E6.0.2.109"),sQuery(id+"F0.wireOp",EDGE,"E6.0.2.110"),sQuery(id+"F0.wireOp",EDGE,"E6.0.2.111"),sQuery(id+"F0.wireOp",EDGE,"E6.0.2.112"),sQuery(id+"F0.wireOp",EDGE,"E6.0.2.113"),sQuery(id+"F0.wireOp",EDGE,"E6.0.2.114"),sQuery(id+"F0.wireOp",EDGE,"E6.0.2.115"),sQuery(id+"F0.wireOp",EDGE,"E6.0.2.117"),sQuery(id+"F0.wireOp",EDGE,"E6.0.2.118"),sQuery(id+"F0.wireOp",EDGE,"E6.0.2.120"),sQuery(id+"F0.wireOp",EDGE,"E6.0.2.121"),sQuery(id+"F0.wireOp",EDGE,"E6.0.2.122"),sQuery(id+"F0.wireOp",EDGE,"E6.0.2.123"),sQuery(id+"F0.wireOp",EDGE,"E6.0.2.124"),sQuery(id+"F0.wireOp",EDGE,"E6.0.2.125"),sQuery(id+"F0.wireOp",EDGE,"E6.0.2.126"),sQuery(id+"F0.wireOp",EDGE,"E6.0.2.127"),sQuery(id+"F0.wireOp",EDGE,"E6.0.2.128"),sQuery(id+"F0.wireOp",EDGE,"E6.0.2.129"),sQuery(id+"F0.wireOp",EDGE,"E6.0.2.130"),sQuery(id+"F0.wireOp",EDGE,"E6.0.2.131"),sQuery(id+"F0.wireOp",EDGE,"E6.0.2.132"),sQuery(id+"F0.wireOp",EDGE,"E6.0.2.133"),sQuery(id+"F0.wireOp",EDGE,"E6.0.2.134"),sQuery(id+"F0.wireOp",EDGE,"E6.0.2.135"),sQuery(id+"F0.wireOp",EDGE,"E6.0.2.136"),sQuery(id+"F0.wireOp",EDGE,"E6.0.2.137"),sQuery(id+"F0.wireOp",EDGE,"E6.0.2.138"),sQuery(id+"F0.wireOp",EDGE,"E6.0.2.139"),sQuery(id+"F0.wireOp",EDGE,"E6.0.2.140"),sQuery(id+"F0.wireOp",EDGE,"E6.0.2.141"),sQuery(id+"F0.wireOp",EDGE,"E6.0.2.143"),sQuery(id+"F0.wireOp",EDGE,"E6.0.2.144"),sQuery(id+"F0.wireOp",EDGE,"E6.0.3.2"),sQuery(id+"F0.wireOp",EDGE,"E6.0.3.4"),sQuery(id+"F0.wireOp",EDGE,"E6.0.3.8"),sQuery(id+"F0.wireOp",EDGE,"E6.0.3.10"),sQuery(id+"F0.wireOp",EDGE,"E6.0.3.11"),sQuery(id+"F0.wireOp",EDGE,"E6.0.3.12"),sQuery(id+"F0.wireOp",EDGE,"E6.0.3.13"),sQuery(id+"F0.wireOp",EDGE,"E6.0.3.14"),sQuery(id+"F0.wireOp",EDGE,"E6.0.3.15"),sQuery(id+"F0.wireOp",EDGE,"E6.0.3.16"),sQuery(id+"F0.wireOp",EDGE,"E6.0.3.17"),sQuery(id+"F0.wireOp",EDGE,"E6.0.3.18"),sQuery(id+"F0.wireOp",EDGE,"E6.0.3.20"),sQuery(id+"F0.wireOp",EDGE,"E6.0.3.21"),sQuery(id+"F0.wireOp",EDGE,"E6.0.3.22"),sQuery(id+"F0.wireOp",EDGE,"E6.0.3.23"),sQuery(id+"F0.wireOp",EDGE,"E6.0.3.24"),sQuery(id+"F0.wireOp",EDGE,"E6.0.3.25"),sQuery(id+"F0.wireOp",EDGE,"E6.0.3.26"),sQuery(id+"F0.wireOp",EDGE,"E6.0.3.27"),sQuery(id+"F0.wireOp",EDGE,"E6.0.3.28"),sQuery(id+"F0.wireOp",EDGE,"E6.0.3.29"),sQuery(id+"F0.wireOp",EDGE,"E6.0.3.30"),sQuery(id+"F0.wireOp",EDGE,"E6.0.3.31"),sQuery(id+"F0.wireOp",EDGE,"E6.0.3.33"),sQuery(id+"F0.wireOp",EDGE,"E6.0.3.34"),sQuery(id+"F0.wireOp",EDGE,"E6.0.3.36"),sQuery(id+"F0.wireOp",EDGE,"E6.0.3.37"),sQuery(id+"F0.wireOp",EDGE,"E6.0.3.38"),sQuery(id+"F0.wireOp",EDGE,"E6.0.3.39"),sQuery(id+"F0.wireOp",EDGE,"E6.0.3.41"),sQuery(id+"F0.wireOp",EDGE,"E6.0.3.42"),sQuery(id+"F0.wireOp",EDGE,"E6.0.3.43"),sQuery(id+"F0.wireOp",EDGE,"E6.0.3.44"),sQuery(id+"F0.wireOp",EDGE,"E6.0.3.46"),sQuery(id+"F0.wireOp",EDGE,"E6.0.3.48"),sQuery(id+"F0.wireOp",EDGE,"E6.0.3.49"),sQuery(id+"F0.wireOp",EDGE,"E6.0.3.51"),sQuery(id+"F0.wireOp",EDGE,"E6.0.3.52"),sQuery(id+"F0.wireOp",EDGE,"E6.0.3.53"),sQuery(id+"F0.wireOp",EDGE,"E6.0.3.54"),sQuery(id+"F0.wireOp",EDGE,"E6.0.3.55"),sQuery(id+"F0.wireOp",EDGE,"E6.0.3.57"),sQuery(id+"F0.wireOp",EDGE,"E6.0.3.59"),sQuery(id+"F0.wireOp",EDGE,"E6.0.3.60"),sQuery(id+"F0.wireOp",EDGE,"E6.0.3.62"),sQuery(id+"F0.wireOp",EDGE,"E6.0.3.63"),sQuery(id+"F0.wireOp",EDGE,"E6.0.3.64"),sQuery(id+"F0.wireOp",EDGE,"E6.0.3.65"),sQuery(id+"F0.wireOp",EDGE,"E6.0.3.66"),sQuery(id+"F0.wireOp",EDGE,"E6.0.3.67"),sQuery(id+"F0.wireOp",EDGE,"E6.0.3.68"),sQuery(id+"F0.wireOp",EDGE,"E6.0.3.70"),sQuery(id+"F0.wireOp",EDGE,"E6.0.3.71"),sQuery(id+"F0.wireOp",EDGE,"E6.0.3.72"),sQuery(id+"F0.wireOp",EDGE,"E6.0.3.73"),sQuery(id+"F0.wireOp",EDGE,"E6.0.3.75"),sQuery(id+"F0.wireOp",EDGE,"E6.0.3.76"),sQuery(id+"F0.wireOp",EDGE,"E6.0.3.77"),sQuery(id+"F0.wireOp",EDGE,"E6.0.3.78"),sQuery(id+"F0.wireOp",EDGE,"E6.0.3.80"),sQuery(id+"F0.wireOp",EDGE,"E6.0.3.81"),sQuery(id+"F0.wireOp",EDGE,"E6.0.3.82"),sQuery(id+"F0.wireOp",EDGE,"E6.0.3.83"),sQuery(id+"F0.wireOp",EDGE,"E6.0.3.85"),sQuery(id+"F0.wireOp",EDGE,"E6.0.3.86"),sQuery(id+"F0.wireOp",EDGE,"E6.0.3.87"),sQuery(id+"F0.wireOp",EDGE,"E6.0.3.88"),sQuery(id+"F0.wireOp",EDGE,"E6.0.3.89"),sQuery(id+"F0.wireOp",EDGE,"E6.0.3.90"),sQuery(id+"F0.wireOp",EDGE,"E6.0.3.91"),sQuery(id+"F0.wireOp",EDGE,"E6.0.3.92"),sQuery(id+"F0.wireOp",EDGE,"E6.0.3.94"),sQuery(id+"F0.wireOp",EDGE,"E6.0.3.95"),sQuery(id+"F0.wireOp",EDGE,"E6.0.3.96"),sQuery(id+"F0.wireOp",EDGE,"E6.0.3.97"),sQuery(id+"F0.wireOp",EDGE,"E6.0.3.98"),sQuery(id+"F0.wireOp",EDGE,"E6.0.3.99"),sQuery(id+"F0.wireOp",EDGE,"E6.0.3.100"),sQuery(id+"F0.wireOp",EDGE,"E6.0.3.101"),sQuery(id+"F0.wireOp",EDGE,"E6.0.3.102"),sQuery(id+"F0.wireOp",EDGE,"E6.0.3.103"),sQuery(id+"F0.wireOp",EDGE,"E6.0.3.104"),sQuery(id+"F0.wireOp",EDGE,"E6.0.3.105"),sQuery(id+"F0.wireOp",EDGE,"E6.0.3.106"),sQuery(id+"F0.wireOp",EDGE,"E6.0.3.107"),sQuery(id+"F0.wireOp",EDGE,"E6.0.3.108"),sQuery(id+"F0.wireOp",EDGE,"E6.0.3.109"),sQuery(id+"F0.wireOp",EDGE,"E6.0.3.110"),sQuery(id+"F0.wireOp",EDGE,"E6.0.3.111"),sQuery(id+"F0.wireOp",EDGE,"E6.0.3.112"),sQuery(id+"F0.wireOp",EDGE,"E6.0.3.113"),sQuery(id+"F0.wireOp",EDGE,"E6.0.3.114"),sQuery(id+"F0.wireOp",EDGE,"E6.0.3.115"),sQuery(id+"F0.wireOp",EDGE,"E6.0.3.117"),sQuery(id+"F0.wireOp",EDGE,"E6.0.3.118"),sQuery(id+"F0.wireOp",EDGE,"E6.0.3.120"),sQuery(id+"F0.wireOp",EDGE,"E6.0.3.121"),sQuery(id+"F0.wireOp",EDGE,"E6.0.3.122"),sQuery(id+"F0.wireOp",EDGE,"E6.0.3.123"),sQuery(id+"F0.wireOp",EDGE,"E6.0.3.124"),sQuery(id+"F0.wireOp",EDGE,"E6.0.3.125"),sQuery(id+"F0.wireOp",EDGE,"E6.0.3.126"),sQuery(id+"F0.wireOp",EDGE,"E6.0.3.127"),sQuery(id+"F0.wireOp",EDGE,"E6.0.3.128"),sQuery(id+"F0.wireOp",EDGE,"E6.0.3.129"),sQuery(id+"F0.wireOp",EDGE,"E6.0.3.130"),sQuery(id+"F0.wireOp",EDGE,"E6.0.3.131"),sQuery(id+"F0.wireOp",EDGE,"E6.0.3.132"),sQuery(id+"F0.wireOp",EDGE,"E6.0.3.133"),sQuery(id+"F0.wireOp",EDGE,"E6.0.3.134"),sQuery(id+"F0.wireOp",EDGE,"E6.0.3.135"),sQuery(id+"F0.wireOp",EDGE,"E6.0.3.136"),sQuery(id+"F0.wireOp",EDGE,"E6.0.3.137"),sQuery(id+"F0.wireOp",EDGE,"E6.0.3.138"),sQuery(id+"F0.wireOp",EDGE,"E6.0.3.139"),sQuery(id+"F0.wireOp",EDGE,"E6.0.3.140"),sQuery(id+"F0.wireOp",EDGE,"E6.0.3.141"),sQuery(id+"F0.wireOp",EDGE,"E6.0.3.143"),sQuery(id+"F0.wireOp",EDGE,"E6.0.3.144"),sQuery(id+"F0.wireOp",EDGE,"E6.0.4.2"),sQuery(id+"F0.wireOp",EDGE,"E6.0.4.4"),sQuery(id+"F0.wireOp",EDGE,"E6.0.4.8"),sQuery(id+"F0.wireOp",EDGE,"E6.0.4.10"),sQuery(id+"F0.wireOp",EDGE,"E6.0.4.11"),sQuery(id+"F0.wireOp",EDGE,"E6.0.4.12"),sQuery(id+"F0.wireOp",EDGE,"E6.0.4.13"),sQuery(id+"F0.wireOp",EDGE,"E6.0.4.14"),sQuery(id+"F0.wireOp",EDGE,"E6.0.4.15"),sQuery(id+"F0.wireOp",EDGE,"E6.0.4.16"),sQuery(id+"F0.wireOp",EDGE,"E6.0.4.17"),sQuery(id+"F0.wireOp",EDGE,"E6.0.4.18"),sQuery(id+"F0.wireOp",EDGE,"E6.0.4.20"),sQuery(id+"F0.wireOp",EDGE,"E6.0.4.21"),sQuery(id+"F0.wireOp",EDGE,"E6.0.4.22"),sQuery(id+"F0.wireOp",EDGE,"E6.0.4.23"),sQuery(id+"F0.wireOp",EDGE,"E6.0.4.24"),sQuery(id+"F0.wireOp",EDGE,"E6.0.4.25"),sQuery(id+"F0.wireOp",EDGE,"E6.0.4.26"),sQuery(id+"F0.wireOp",EDGE,"E6.0.4.27"),sQuery(id+"F0.wireOp",EDGE,"E6.0.4.28"),sQuery(id+"F0.wireOp",EDGE,"E6.0.4.29"),sQuery(id+"F0.wireOp",EDGE,"E6.0.4.30"),sQuery(id+"F0.wireOp",EDGE,"E6.0.4.31"),sQuery(id+"F0.wireOp",EDGE,"E6.0.4.33"),sQuery(id+"F0.wireOp",EDGE,"E6.0.4.34"),sQuery(id+"F0.wireOp",EDGE,"E6.0.4.36"),sQuery(id+"F0.wireOp",EDGE,"E6.0.4.37"),sQuery(id+"F0.wireOp",EDGE,"E6.0.4.38"),sQuery(id+"F0.wireOp",EDGE,"E6.0.4.39"),sQuery(id+"F0.wireOp",EDGE,"E6.0.4.41"),sQuery(id+"F0.wireOp",EDGE,"E6.0.4.42"),sQuery(id+"F0.wireOp",EDGE,"E6.0.4.43"),sQuery(id+"F0.wireOp",EDGE,"E6.0.4.44"),sQuery(id+"F0.wireOp",EDGE,"E6.0.4.46"),sQuery(id+"F0.wireOp",EDGE,"E6.0.4.48"),sQuery(id+"F0.wireOp",EDGE,"E6.0.4.49"),sQuery(id+"F0.wireOp",EDGE,"E6.0.4.51"),sQuery(id+"F0.wireOp",EDGE,"E6.0.4.52"),sQuery(id+"F0.wireOp",EDGE,"E6.0.4.53"),sQuery(id+"F0.wireOp",EDGE,"E6.0.4.54"),sQuery(id+"F0.wireOp",EDGE,"E6.0.4.55"),sQuery(id+"F0.wireOp",EDGE,"E6.0.4.57"),sQuery(id+"F0.wireOp",EDGE,"E6.0.4.59"),sQuery(id+"F0.wireOp",EDGE,"E6.0.4.60"),sQuery(id+"F0.wireOp",EDGE,"E6.0.4.62"),sQuery(id+"F0.wireOp",EDGE,"E6.0.4.63"),sQuery(id+"F0.wireOp",EDGE,"E6.0.4.64"),sQuery(id+"F0.wireOp",EDGE,"E6.0.4.65"),sQuery(id+"F0.wireOp",EDGE,"E6.0.4.66"),sQuery(id+"F0.wireOp",EDGE,"E6.0.4.67"),sQuery(id+"F0.wireOp",EDGE,"E6.0.4.68"),sQuery(id+"F0.wireOp",EDGE,"E6.0.4.70"),sQuery(id+"F0.wireOp",EDGE,"E6.0.4.71"),sQuery(id+"F0.wireOp",EDGE,"E6.0.4.72"),sQuery(id+"F0.wireOp",EDGE,"E6.0.4.73"),sQuery(id+"F0.wireOp",EDGE,"E6.0.4.75"),sQuery(id+"F0.wireOp",EDGE,"E6.0.4.76"),sQuery(id+"F0.wireOp",EDGE,"E6.0.4.77"),sQuery(id+"F0.wireOp",EDGE,"E6.0.4.78"),sQuery(id+"F0.wireOp",EDGE,"E6.0.4.80"),sQuery(id+"F0.wireOp",EDGE,"E6.0.4.81"),sQuery(id+"F0.wireOp",EDGE,"E6.0.4.82"),sQuery(id+"F0.wireOp",EDGE,"E6.0.4.83"),sQuery(id+"F0.wireOp",EDGE,"E6.0.4.85"),sQuery(id+"F0.wireOp",EDGE,"E6.0.4.86"),sQuery(id+"F0.wireOp",EDGE,"E6.0.4.87"),sQuery(id+"F0.wireOp",EDGE,"E6.0.4.88"),sQuery(id+"F0.wireOp",EDGE,"E6.0.4.89"),sQuery(id+"F0.wireOp",EDGE,"E6.0.4.90"),sQuery(id+"F0.wireOp",EDGE,"E6.0.4.91"),sQuery(id+"F0.wireOp",EDGE,"E6.0.4.92"),sQuery(id+"F0.wireOp",EDGE,"E6.0.4.94"),sQuery(id+"F0.wireOp",EDGE,"E6.0.4.95"),sQuery(id+"F0.wireOp",EDGE,"E6.0.4.96"),sQuery(id+"F0.wireOp",EDGE,"E6.0.4.97"),sQuery(id+"F0.wireOp",EDGE,"E6.0.4.98"),sQuery(id+"F0.wireOp",EDGE,"E6.0.4.99"),sQuery(id+"F0.wireOp",EDGE,"E6.0.4.100"),sQuery(id+"F0.wireOp",EDGE,"E6.0.4.101"),sQuery(id+"F0.wireOp",EDGE,"E6.0.4.102"),sQuery(id+"F0.wireOp",EDGE,"E6.0.4.103"),sQuery(id+"F0.wireOp",EDGE,"E6.0.4.104"),sQuery(id+"F0.wireOp",EDGE,"E6.0.4.105"),sQuery(id+"F0.wireOp",EDGE,"E6.0.4.106"),sQuery(id+"F0.wireOp",EDGE,"E6.0.4.107"),sQuery(id+"F0.wireOp",EDGE,"E6.0.4.108"),sQuery(id+"F0.wireOp",EDGE,"E6.0.4.109"),sQuery(id+"F0.wireOp",EDGE,"E6.0.4.110"),sQuery(id+"F0.wireOp",EDGE,"E6.0.4.111"),sQuery(id+"F0.wireOp",EDGE,"E6.0.4.112"),sQuery(id+"F0.wireOp",EDGE,"E6.0.4.113"),sQuery(id+"F0.wireOp",EDGE,"E6.0.4.114"),sQuery(id+"F0.wireOp",EDGE,"E6.0.4.115"),sQuery(id+"F0.wireOp",EDGE,"E6.0.4.117"),sQuery(id+"F0.wireOp",EDGE,"E6.0.4.118"),sQuery(id+"F0.wireOp",EDGE,"E6.0.4.120"),sQuery(id+"F0.wireOp",EDGE,"E6.0.4.121"),sQuery(id+"F0.wireOp",EDGE,"E6.0.4.122"),sQuery(id+"F0.wireOp",EDGE,"E6.0.4.123"),sQuery(id+"F0.wireOp",EDGE,"E6.0.4.124"),sQuery(id+"F0.wireOp",EDGE,"E6.0.4.125"),sQuery(id+"F0.wireOp",EDGE,"E6.0.4.126"),sQuery(id+"F0.wireOp",EDGE,"E6.0.4.127"),sQuery(id+"F0.wireOp",EDGE,"E6.0.4.128"),sQuery(id+"F0.wireOp",EDGE,"E6.0.4.129"),sQuery(id+"F0.wireOp",EDGE,"E6.0.4.130"),sQuery(id+"F0.wireOp",EDGE,"E6.0.4.131"),sQuery(id+"F0.wireOp",EDGE,"E6.0.4.132"),sQuery(id+"F0.wireOp",EDGE,"E6.0.4.133"),sQuery(id+"F0.wireOp",EDGE,"E6.0.4.134"),sQuery(id+"F0.wireOp",EDGE,"E6.0.4.135"),sQuery(id+"F0.wireOp",EDGE,"E6.0.4.136"),sQuery(id+"F0.wireOp",EDGE,"E6.0.4.137"),sQuery(id+"F0.wireOp",EDGE,"E6.0.4.138"),sQuery(id+"F0.wireOp",EDGE,"E6.0.4.139"),sQuery(id+"F0.wireOp",EDGE,"E6.0.4.140"),sQuery(id+"F0.wireOp",EDGE,"E6.0.4.141"),sQuery(id+"F0.wireOp",EDGE,"E6.0.4.143"),sQuery(id+"F0.wireOp",EDGE,"E6.0.4.144"),sQuery(id+"F0.wireOp",EDGE,"E10.bottom"),sQuery(id+"F0.wireOp",EDGE,"E10.top"),sQuery(id+"F0.wireOp",EDGE,"E10.left"),sQuery(id+"F0.wireOp",EDGE,"E10.right")])]});
            var Q1;
            Q1=qCreatedBy(makeId("Front.planeOp"),FACE);
            mirror(context, id + "F3", {"entities" : qUnion([Q0]), "mirrorPlane" : qUnion([Q1])});
        }
    });
